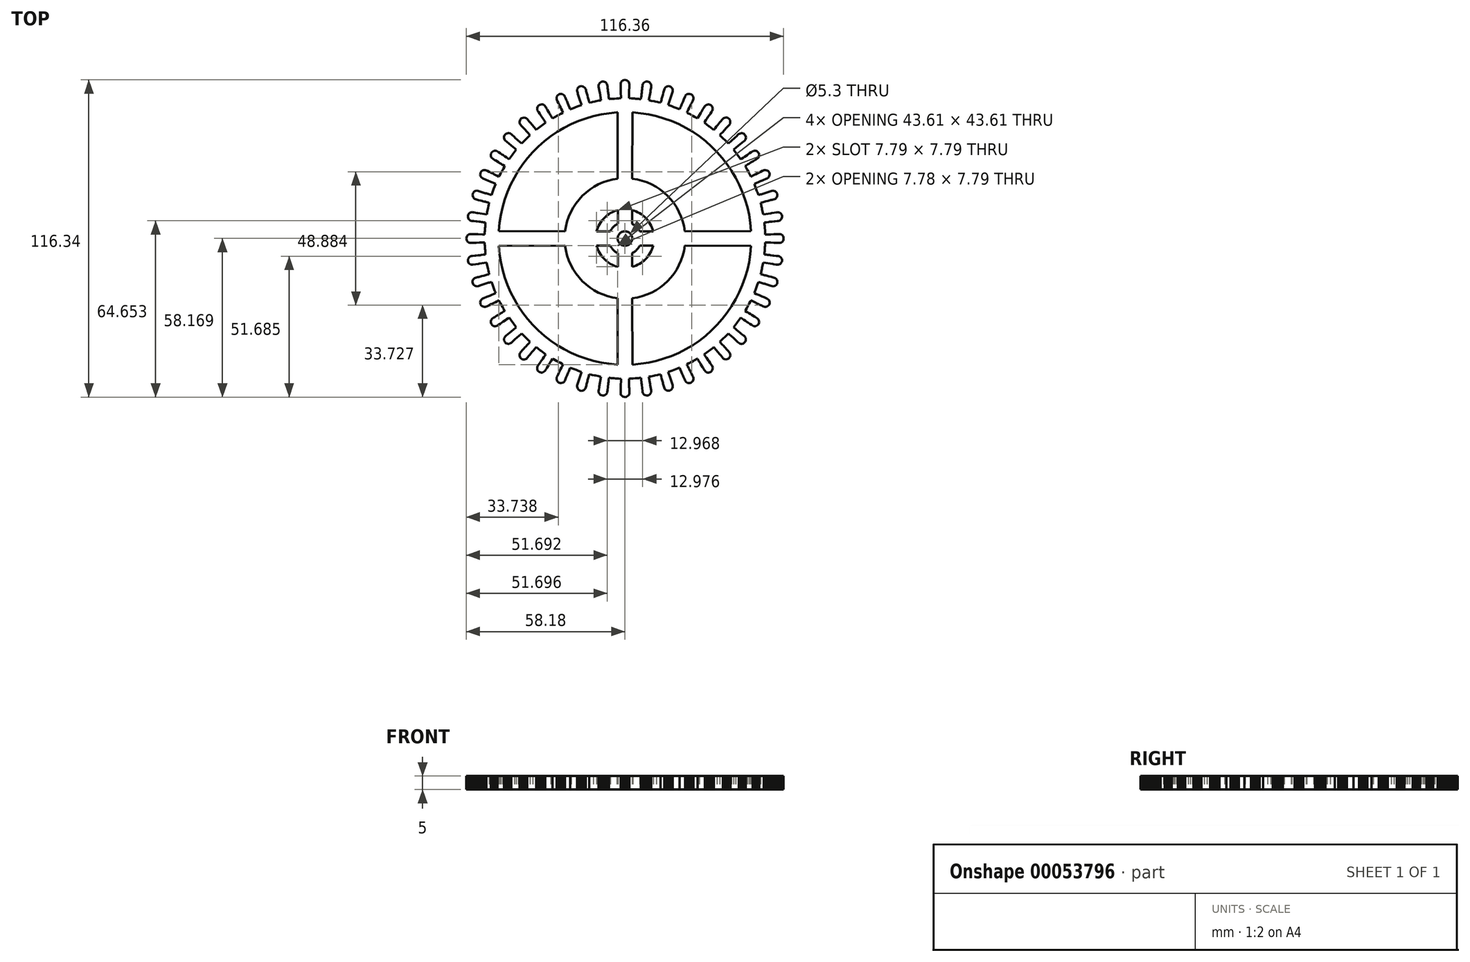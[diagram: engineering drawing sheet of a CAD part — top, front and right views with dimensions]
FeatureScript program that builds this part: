
annotation { "Feature Type Name" : "Feature", "Feature Type Description" : "" }
export const myFeature = defineFeature(function(context is Context, id is Id, definition is map)
    precondition{}
    {
        {
            var Q0;
            Q0=qCreatedBy(makeId("Top.planeOp"),FACE);
            var sketch = newSketch(context, id + "F0", { "sketchPlane" : qUnion([Q0])});
            skLineSegment(sketch, "E0", {"start": v(49.47, -1.46) * mm, "end": v(49.81, -1.47) * mm});
            skLineSegment(sketch, "E1", {"start": v(49.81, -1.47) * mm, "end": v(50.2, -1.49) * mm});
            skLineSegment(sketch, "E2", {"start": v(50.2, -1.49) * mm, "end": v(50.6, -1.5) * mm});
            skLineSegment(sketch, "E3", {"start": v(50.6, -1.5) * mm, "end": v(51, -1.5) * mm});
            skLineSegment(sketch, "E4", {"start": v(51, -1.5) * mm, "end": v(51.4, -1.52) * mm});
            skLineSegment(sketch, "E5", {"start": v(51.4, -1.52) * mm, "end": v(51.78, -1.53) * mm});
            skLineSegment(sketch, "E6", {"start": v(51.78, -1.53) * mm, "end": v(52.18, -1.54) * mm});
            skLineSegment(sketch, "E7", {"start": v(52.18, -1.54) * mm, "end": v(52.58, -1.55) * mm});
            skLineSegment(sketch, "E8", {"start": v(52.58, -1.55) * mm, "end": v(52.97, -1.56) * mm});
            skLineSegment(sketch, "E9", {"start": v(52.97, -1.56) * mm, "end": v(53.37, -1.58) * mm});
            skLineSegment(sketch, "E10", {"start": v(53.37, -1.58) * mm, "end": v(53.76, -1.59) * mm});
            skLineSegment(sketch, "E11", {"start": v(53.76, -1.59) * mm, "end": v(54.16, -1.6) * mm});
            skLineSegment(sketch, "E12", {"start": v(54.16, -1.6) * mm, "end": v(54.56, -1.6) * mm});
            skLineSegment(sketch, "E13", {"start": v(54.56, -1.6) * mm, "end": v(54.98, -1.56) * mm});
            skLineSegment(sketch, "E14", {"start": v(54.98, -1.56) * mm, "end": v(55.37, -1.4) * mm});
            skLineSegment(sketch, "E15", {"start": v(55.37, -1.4) * mm, "end": v(55.7, -1.15) * mm});
            skLineSegment(sketch, "E16", {"start": v(55.7, -1.15) * mm, "end": v(55.97, -0.81) * mm});
            skLineSegment(sketch, "E17", {"start": v(55.97, -0.81) * mm, "end": v(56.13, -0.42) * mm});
            skLineSegment(sketch, "E18", {"start": v(56.13, -0.42) * mm, "end": v(56.19, 0) * mm});
            skLineSegment(sketch, "E19", {"start": v(56.19, 0) * mm, "end": v(56.13, 0.42) * mm});
            skLineSegment(sketch, "E20", {"start": v(56.13, 0.42) * mm, "end": v(55.97, 0.8) * mm});
            skLineSegment(sketch, "E21", {"start": v(55.97, 0.8) * mm, "end": v(55.7, 1.14) * mm});
            skLineSegment(sketch, "E22", {"start": v(55.7, 1.14) * mm, "end": v(55.37, 1.4) * mm});
            skLineSegment(sketch, "E23", {"start": v(55.37, 1.4) * mm, "end": v(54.98, 1.56) * mm});
            skLineSegment(sketch, "E24", {"start": v(54.98, 1.56) * mm, "end": v(54.56, 1.6) * mm});
            skLineSegment(sketch, "E25", {"start": v(54.56, 1.6) * mm, "end": v(54.16, 1.6) * mm});
            skLineSegment(sketch, "E26", {"start": v(54.16, 1.6) * mm, "end": v(53.77, 1.58) * mm});
            skLineSegment(sketch, "E27", {"start": v(53.77, 1.58) * mm, "end": v(53.37, 1.57) * mm});
            skLineSegment(sketch, "E28", {"start": v(53.37, 1.57) * mm, "end": v(52.98, 1.56) * mm});
            skLineSegment(sketch, "E29", {"start": v(52.98, 1.56) * mm, "end": v(52.58, 1.55) * mm});
            skLineSegment(sketch, "E30", {"start": v(52.58, 1.55) * mm, "end": v(52.18, 1.54) * mm});
            skLineSegment(sketch, "E31", {"start": v(52.18, 1.54) * mm, "end": v(51.79, 1.53) * mm});
            skLineSegment(sketch, "E32", {"start": v(51.79, 1.53) * mm, "end": v(51.4, 1.52) * mm});
            skLineSegment(sketch, "E33", {"start": v(51.4, 1.52) * mm, "end": v(51, 1.5) * mm});
            skLineSegment(sketch, "E34", {"start": v(51, 1.5) * mm, "end": v(50.6, 1.5) * mm});
            skLineSegment(sketch, "E35", {"start": v(50.6, 1.5) * mm, "end": v(50.2, 1.48) * mm});
            skLineSegment(sketch, "E36", {"start": v(50.2, 1.48) * mm, "end": v(49.81, 1.47) * mm});
            skLineSegment(sketch, "E37", {"start": v(49.81, 1.47) * mm, "end": v(49.47, 1.46) * mm});
            skLineSegment(sketch, "E38", {"start": v(49.47, 1.46) * mm, "end": v(49.44, 1.85) * mm});
            skLineSegment(sketch, "E39", {"start": v(49.44, 1.85) * mm, "end": v(49.42, 2.25) * mm});
            skLineSegment(sketch, "E40", {"start": v(49.42, 2.25) * mm, "end": v(49.39, 2.64) * mm});
            skLineSegment(sketch, "E41", {"start": v(49.39, 2.64) * mm, "end": v(49.36, 3.03) * mm});
            skLineSegment(sketch, "E42", {"start": v(49.36, 3.03) * mm, "end": v(49.33, 3.43) * mm});
            skLineSegment(sketch, "E43", {"start": v(49.33, 3.43) * mm, "end": v(49.3, 3.82) * mm});
            skLineSegment(sketch, "E44", {"start": v(49.3, 3.82) * mm, "end": v(49.28, 4.21) * mm});
            skLineSegment(sketch, "E45", {"start": v(49.28, 4.21) * mm, "end": v(49.25, 4.6) * mm});
            skLineSegment(sketch, "E46", {"start": v(49.25, 4.6) * mm, "end": v(49.22, 5) * mm});
            skLineSegment(sketch, "E47", {"start": v(49.22, 5) * mm, "end": v(49.2, 5.4) * mm});
            skLineSegment(sketch, "E48", {"start": v(49.2, 5.4) * mm, "end": v(49.16, 5.78) * mm});
            skLineSegment(sketch, "E49", {"start": v(49.16, 5.78) * mm, "end": v(49.16, 5.87) * mm});
            skLineSegment(sketch, "E50", {"start": v(49.16, 5.87) * mm, "end": v(49.55, 5.92) * mm});
            skLineSegment(sketch, "E51", {"start": v(49.55, 5.92) * mm, "end": v(49.94, 5.96) * mm});
            skLineSegment(sketch, "E52", {"start": v(49.94, 5.96) * mm, "end": v(50.34, 6) * mm});
            skLineSegment(sketch, "E53", {"start": v(50.34, 6) * mm, "end": v(50.73, 6.05) * mm});
            skLineSegment(sketch, "E54", {"start": v(50.73, 6.05) * mm, "end": v(51.12, 6.1) * mm});
            skLineSegment(sketch, "E55", {"start": v(51.12, 6.1) * mm, "end": v(51.51, 6.15) * mm});
            skLineSegment(sketch, "E56", {"start": v(51.51, 6.15) * mm, "end": v(51.9, 6.2) * mm});
            skLineSegment(sketch, "E57", {"start": v(51.9, 6.2) * mm, "end": v(52.3, 6.24) * mm});
            skLineSegment(sketch, "E58", {"start": v(52.3, 6.24) * mm, "end": v(52.7, 6.28) * mm});
            skLineSegment(sketch, "E59", {"start": v(52.7, 6.28) * mm, "end": v(53.08, 6.33) * mm});
            skLineSegment(sketch, "E60", {"start": v(53.08, 6.33) * mm, "end": v(53.48, 6.37) * mm});
            skLineSegment(sketch, "E61", {"start": v(53.48, 6.37) * mm, "end": v(53.87, 6.42) * mm});
            skLineSegment(sketch, "E62", {"start": v(53.87, 6.42) * mm, "end": v(54.3, 6.47) * mm});
            skLineSegment(sketch, "E63", {"start": v(54.3, 6.47) * mm, "end": v(54.7, 6.6) * mm});
            skLineSegment(sketch, "E64", {"start": v(54.7, 6.6) * mm, "end": v(55.05, 6.83) * mm});
            skLineSegment(sketch, "E65", {"start": v(55.05, 6.83) * mm, "end": v(55.33, 7.15) * mm});
            skLineSegment(sketch, "E66", {"start": v(55.33, 7.15) * mm, "end": v(55.52, 7.52) * mm});
            skLineSegment(sketch, "E67", {"start": v(55.52, 7.52) * mm, "end": v(55.6, 7.94) * mm});
            skLineSegment(sketch, "E68", {"start": v(55.6, 7.94) * mm, "end": v(55.6, 8.28) * mm});
            skLineSegment(sketch, "E69", {"start": v(55.6, 8.28) * mm, "end": v(55.48, 8.69) * mm});
            skLineSegment(sketch, "E70", {"start": v(55.48, 8.69) * mm, "end": v(55.26, 9.05) * mm});
            skLineSegment(sketch, "E71", {"start": v(55.26, 9.05) * mm, "end": v(54.96, 9.34) * mm});
            skLineSegment(sketch, "E72", {"start": v(54.96, 9.34) * mm, "end": v(54.59, 9.55) * mm});
            skLineSegment(sketch, "E73", {"start": v(54.59, 9.55) * mm, "end": v(54.17, 9.65) * mm});
            skLineSegment(sketch, "E74", {"start": v(54.17, 9.65) * mm, "end": v(54, 9.66) * mm});
            skLineSegment(sketch, "E75", {"start": v(54, 9.66) * mm, "end": v(53.75, 9.64) * mm});
            skLineSegment(sketch, "E76", {"start": v(53.75, 9.64) * mm, "end": v(53.36, 9.57) * mm});
            skLineSegment(sketch, "E77", {"start": v(53.36, 9.57) * mm, "end": v(52.98, 9.5) * mm});
            skLineSegment(sketch, "E78", {"start": v(52.98, 9.5) * mm, "end": v(52.58, 9.44) * mm});
            skLineSegment(sketch, "E79", {"start": v(52.58, 9.44) * mm, "end": v(52.2, 9.37) * mm});
            skLineSegment(sketch, "E80", {"start": v(52.2, 9.37) * mm, "end": v(51.8, 9.3) * mm});
            skLineSegment(sketch, "E81", {"start": v(51.8, 9.3) * mm, "end": v(51.41, 9.23) * mm});
            skLineSegment(sketch, "E82", {"start": v(51.41, 9.23) * mm, "end": v(51.02, 9.17) * mm});
            skLineSegment(sketch, "E83", {"start": v(51.02, 9.17) * mm, "end": v(50.64, 9.1) * mm});
            skLineSegment(sketch, "E84", {"start": v(50.64, 9.1) * mm, "end": v(50.24, 9.03) * mm});
            skLineSegment(sketch, "E85", {"start": v(50.24, 9.03) * mm, "end": v(49.86, 8.96) * mm});
            skLineSegment(sketch, "E86", {"start": v(49.86, 8.96) * mm, "end": v(49.47, 8.9) * mm});
            skLineSegment(sketch, "E87", {"start": v(49.47, 8.9) * mm, "end": v(49.07, 8.83) * mm});
            skLineSegment(sketch, "E88", {"start": v(49.07, 8.83) * mm, "end": v(48.74, 8.77) * mm});
            skLineSegment(sketch, "E89", {"start": v(48.74, 8.77) * mm, "end": v(48.66, 9.16) * mm});
            skLineSegment(sketch, "E90", {"start": v(48.66, 9.16) * mm, "end": v(48.57, 9.54) * mm});
            skLineSegment(sketch, "E91", {"start": v(48.57, 9.54) * mm, "end": v(48.49, 9.93) * mm});
            skLineSegment(sketch, "E92", {"start": v(48.49, 9.93) * mm, "end": v(48.4, 10.31) * mm});
            skLineSegment(sketch, "E93", {"start": v(48.4, 10.31) * mm, "end": v(48.32, 10.7) * mm});
            skLineSegment(sketch, "E94", {"start": v(48.32, 10.7) * mm, "end": v(48.24, 11.08) * mm});
            skLineSegment(sketch, "E95", {"start": v(48.24, 11.08) * mm, "end": v(48.15, 11.46) * mm});
            skLineSegment(sketch, "E96", {"start": v(48.15, 11.46) * mm, "end": v(48.07, 11.85) * mm});
            skLineSegment(sketch, "E97", {"start": v(48.07, 11.85) * mm, "end": v(47.99, 12.23) * mm});
            skLineSegment(sketch, "E98", {"start": v(47.99, 12.23) * mm, "end": v(47.9, 12.62) * mm});
            skLineSegment(sketch, "E99", {"start": v(47.9, 12.62) * mm, "end": v(47.82, 13) * mm});
            skLineSegment(sketch, "E100", {"start": v(47.82, 13) * mm, "end": v(47.8, 13.1) * mm});
            skLineSegment(sketch, "E101", {"start": v(47.8, 13.1) * mm, "end": v(48.18, 13.2) * mm});
            skLineSegment(sketch, "E102", {"start": v(48.18, 13.2) * mm, "end": v(48.56, 13.3) * mm});
            skLineSegment(sketch, "E103", {"start": v(48.56, 13.3) * mm, "end": v(48.95, 13.4) * mm});
            skLineSegment(sketch, "E104", {"start": v(48.95, 13.4) * mm, "end": v(49.33, 13.5) * mm});
            skLineSegment(sketch, "E105", {"start": v(49.33, 13.5) * mm, "end": v(49.7, 13.6) * mm});
            skLineSegment(sketch, "E106", {"start": v(49.7, 13.6) * mm, "end": v(50.1, 13.7) * mm});
            skLineSegment(sketch, "E107", {"start": v(50.1, 13.7) * mm, "end": v(50.48, 13.8) * mm});
            skLineSegment(sketch, "E108", {"start": v(50.48, 13.8) * mm, "end": v(50.86, 13.9) * mm});
            skLineSegment(sketch, "E109", {"start": v(50.86, 13.9) * mm, "end": v(51.24, 14) * mm});
            skLineSegment(sketch, "E110", {"start": v(51.24, 14) * mm, "end": v(51.62, 14.1) * mm});
            skLineSegment(sketch, "E111", {"start": v(51.62, 14.1) * mm, "end": v(52, 14.2) * mm});
            skLineSegment(sketch, "E112", {"start": v(52, 14.2) * mm, "end": v(52.4, 14.3) * mm});
            skLineSegment(sketch, "E113", {"start": v(52.4, 14.3) * mm, "end": v(52.8, 14.41) * mm});
            skLineSegment(sketch, "E114", {"start": v(52.8, 14.41) * mm, "end": v(53.18, 14.6) * mm});
            skLineSegment(sketch, "E115", {"start": v(53.18, 14.6) * mm, "end": v(53.5, 14.88) * mm});
            skLineSegment(sketch, "E116", {"start": v(53.5, 14.88) * mm, "end": v(53.73, 15.23) * mm});
            skLineSegment(sketch, "E117", {"start": v(53.73, 15.23) * mm, "end": v(53.87, 15.63) * mm});
            skLineSegment(sketch, "E118", {"start": v(53.87, 15.63) * mm, "end": v(53.89, 16.06) * mm});
            skLineSegment(sketch, "E119", {"start": v(53.89, 16.06) * mm, "end": v(53.83, 16.39) * mm});
            skLineSegment(sketch, "E120", {"start": v(53.83, 16.39) * mm, "end": v(53.66, 16.78) * mm});
            skLineSegment(sketch, "E121", {"start": v(53.66, 16.78) * mm, "end": v(53.4, 17.1) * mm});
            skLineSegment(sketch, "E122", {"start": v(53.4, 17.1) * mm, "end": v(53.05, 17.35) * mm});
            skLineSegment(sketch, "E123", {"start": v(53.05, 17.35) * mm, "end": v(52.65, 17.5) * mm});
            skLineSegment(sketch, "E124", {"start": v(52.65, 17.5) * mm, "end": v(52.31, 17.54) * mm});
            skLineSegment(sketch, "E125", {"start": v(52.31, 17.54) * mm, "end": v(51.9, 17.5) * mm});
            skLineSegment(sketch, "E126", {"start": v(51.9, 17.5) * mm, "end": v(51.81, 17.47) * mm});
            skLineSegment(sketch, "E127", {"start": v(51.81, 17.47) * mm, "end": v(51.44, 17.35) * mm});
            skLineSegment(sketch, "E128", {"start": v(51.44, 17.35) * mm, "end": v(51.06, 17.23) * mm});
            skLineSegment(sketch, "E129", {"start": v(51.06, 17.23) * mm, "end": v(50.68, 17.1) * mm});
            skLineSegment(sketch, "E130", {"start": v(50.68, 17.1) * mm, "end": v(50.3, 16.98) * mm});
            skLineSegment(sketch, "E131", {"start": v(50.3, 16.98) * mm, "end": v(49.93, 16.86) * mm});
            skLineSegment(sketch, "E132", {"start": v(49.93, 16.86) * mm, "end": v(49.55, 16.74) * mm});
            skLineSegment(sketch, "E133", {"start": v(49.55, 16.74) * mm, "end": v(49.18, 16.62) * mm});
            skLineSegment(sketch, "E134", {"start": v(49.18, 16.62) * mm, "end": v(48.8, 16.5) * mm});
            skLineSegment(sketch, "E135", {"start": v(48.8, 16.5) * mm, "end": v(48.43, 16.37) * mm});
            skLineSegment(sketch, "E136", {"start": v(48.43, 16.37) * mm, "end": v(48.05, 16.25) * mm});
            skLineSegment(sketch, "E137", {"start": v(48.05, 16.25) * mm, "end": v(47.68, 16.13) * mm});
            skLineSegment(sketch, "E138", {"start": v(47.68, 16.13) * mm, "end": v(47.3, 16) * mm});
            skLineSegment(sketch, "E139", {"start": v(47.3, 16) * mm, "end": v(46.98, 15.9) * mm});
            skLineSegment(sketch, "E140", {"start": v(46.98, 15.9) * mm, "end": v(46.84, 16.27) * mm});
            skLineSegment(sketch, "E141", {"start": v(46.84, 16.27) * mm, "end": v(46.7, 16.64) * mm});
            skLineSegment(sketch, "E142", {"start": v(46.7, 16.64) * mm, "end": v(46.56, 17) * mm});
            skLineSegment(sketch, "E143", {"start": v(46.56, 17) * mm, "end": v(46.42, 17.38) * mm});
            skLineSegment(sketch, "E144", {"start": v(46.42, 17.38) * mm, "end": v(46.29, 17.75) * mm});
            skLineSegment(sketch, "E145", {"start": v(46.29, 17.75) * mm, "end": v(46.15, 18.12) * mm});
            skLineSegment(sketch, "E146", {"start": v(46.15, 18.12) * mm, "end": v(46.01, 18.48) * mm});
            skLineSegment(sketch, "E147", {"start": v(46.01, 18.48) * mm, "end": v(45.87, 18.85) * mm});
            skLineSegment(sketch, "E148", {"start": v(45.87, 18.85) * mm, "end": v(45.74, 19.22) * mm});
            skLineSegment(sketch, "E149", {"start": v(45.74, 19.22) * mm, "end": v(45.6, 19.6) * mm});
            skLineSegment(sketch, "E150", {"start": v(45.6, 19.6) * mm, "end": v(45.46, 19.96) * mm});
            skLineSegment(sketch, "E151", {"start": v(45.46, 19.96) * mm, "end": v(45.43, 20.05) * mm});
            skLineSegment(sketch, "E152", {"start": v(45.43, 20.05) * mm, "end": v(45.8, 20.2) * mm});
            skLineSegment(sketch, "E153", {"start": v(45.8, 20.2) * mm, "end": v(46.15, 20.35) * mm});
            skLineSegment(sketch, "E154", {"start": v(46.15, 20.35) * mm, "end": v(46.52, 20.5) * mm});
            skLineSegment(sketch, "E155", {"start": v(46.52, 20.5) * mm, "end": v(46.88, 20.66) * mm});
            skLineSegment(sketch, "E156", {"start": v(46.88, 20.66) * mm, "end": v(47.25, 20.81) * mm});
            skLineSegment(sketch, "E157", {"start": v(47.25, 20.81) * mm, "end": v(47.62, 20.97) * mm});
            skLineSegment(sketch, "E158", {"start": v(47.62, 20.97) * mm, "end": v(47.98, 21.12) * mm});
            skLineSegment(sketch, "E159", {"start": v(47.98, 21.12) * mm, "end": v(48.34, 21.28) * mm});
            skLineSegment(sketch, "E160", {"start": v(48.34, 21.28) * mm, "end": v(48.7, 21.43) * mm});
            skLineSegment(sketch, "E161", {"start": v(48.7, 21.43) * mm, "end": v(49.07, 21.59) * mm});
            skLineSegment(sketch, "E162", {"start": v(49.07, 21.59) * mm, "end": v(49.43, 21.74) * mm});
            skLineSegment(sketch, "E163", {"start": v(49.43, 21.74) * mm, "end": v(49.8, 21.9) * mm});
            skLineSegment(sketch, "E164", {"start": v(49.8, 21.9) * mm, "end": v(50.2, 22.06) * mm});
            skLineSegment(sketch, "E165", {"start": v(50.2, 22.06) * mm, "end": v(50.54, 22.3) * mm});
            skLineSegment(sketch, "E166", {"start": v(50.54, 22.3) * mm, "end": v(50.82, 22.62) * mm});
            skLineSegment(sketch, "E167", {"start": v(50.82, 22.62) * mm, "end": v(51, 23) * mm});
            skLineSegment(sketch, "E168", {"start": v(51, 23) * mm, "end": v(51.07, 23.42) * mm});
            skLineSegment(sketch, "E169", {"start": v(51.07, 23.42) * mm, "end": v(51.04, 23.84) * mm});
            skLineSegment(sketch, "E170", {"start": v(51.04, 23.84) * mm, "end": v(50.93, 24.17) * mm});
            skLineSegment(sketch, "E171", {"start": v(50.93, 24.17) * mm, "end": v(50.7, 24.52) * mm});
            skLineSegment(sketch, "E172", {"start": v(50.7, 24.52) * mm, "end": v(50.4, 24.81) * mm});
            skLineSegment(sketch, "E173", {"start": v(50.4, 24.81) * mm, "end": v(50.02, 25) * mm});
            skLineSegment(sketch, "E174", {"start": v(50.02, 25) * mm, "end": v(49.6, 25.1) * mm});
            skLineSegment(sketch, "E175", {"start": v(49.6, 25.1) * mm, "end": v(49.43, 25.1) * mm});
            skLineSegment(sketch, "E176", {"start": v(49.43, 25.1) * mm, "end": v(49.02, 25.04) * mm});
            skLineSegment(sketch, "E177", {"start": v(49.02, 25.04) * mm, "end": v(48.78, 24.95) * mm});
            skLineSegment(sketch, "E178", {"start": v(48.78, 24.95) * mm, "end": v(48.42, 24.78) * mm});
            skLineSegment(sketch, "E179", {"start": v(48.42, 24.78) * mm, "end": v(48.07, 24.6) * mm});
            skLineSegment(sketch, "E180", {"start": v(48.07, 24.6) * mm, "end": v(47.71, 24.43) * mm});
            skLineSegment(sketch, "E181", {"start": v(47.71, 24.43) * mm, "end": v(47.36, 24.25) * mm});
            skLineSegment(sketch, "E182", {"start": v(47.36, 24.25) * mm, "end": v(47, 24.08) * mm});
            skLineSegment(sketch, "E183", {"start": v(47, 24.08) * mm, "end": v(46.65, 23.9) * mm});
            skLineSegment(sketch, "E184", {"start": v(46.65, 23.9) * mm, "end": v(46.3, 23.73) * mm});
            skLineSegment(sketch, "E185", {"start": v(46.3, 23.73) * mm, "end": v(45.94, 23.56) * mm});
            skLineSegment(sketch, "E186", {"start": v(45.94, 23.56) * mm, "end": v(45.58, 23.38) * mm});
            skLineSegment(sketch, "E187", {"start": v(45.58, 23.38) * mm, "end": v(45.23, 23.2) * mm});
            skLineSegment(sketch, "E188", {"start": v(45.23, 23.2) * mm, "end": v(44.88, 23.03) * mm});
            skLineSegment(sketch, "E189", {"start": v(44.88, 23.03) * mm, "end": v(44.52, 22.86) * mm});
            skLineSegment(sketch, "E190", {"start": v(44.52, 22.86) * mm, "end": v(44.21, 22.7) * mm});
            skLineSegment(sketch, "E191", {"start": v(44.21, 22.7) * mm, "end": v(44.02, 23.05) * mm});
            skLineSegment(sketch, "E192", {"start": v(44.02, 23.05) * mm, "end": v(43.84, 23.4) * mm});
            skLineSegment(sketch, "E193", {"start": v(43.84, 23.4) * mm, "end": v(43.65, 23.74) * mm});
            skLineSegment(sketch, "E194", {"start": v(43.65, 23.74) * mm, "end": v(43.46, 24.1) * mm});
            skLineSegment(sketch, "E195", {"start": v(43.46, 24.1) * mm, "end": v(43.27, 24.44) * mm});
            skLineSegment(sketch, "E196", {"start": v(43.27, 24.44) * mm, "end": v(43.08, 24.78) * mm});
            skLineSegment(sketch, "E197", {"start": v(43.08, 24.78) * mm, "end": v(42.9, 25.13) * mm});
            skLineSegment(sketch, "E198", {"start": v(42.9, 25.13) * mm, "end": v(42.7, 25.47) * mm});
            skLineSegment(sketch, "E199", {"start": v(42.7, 25.47) * mm, "end": v(42.52, 25.82) * mm});
            skLineSegment(sketch, "E200", {"start": v(42.52, 25.82) * mm, "end": v(42.33, 26.16) * mm});
            skLineSegment(sketch, "E201", {"start": v(42.33, 26.16) * mm, "end": v(42.14, 26.5) * mm});
            skLineSegment(sketch, "E202", {"start": v(42.14, 26.5) * mm, "end": v(42.1, 26.6) * mm});
            skLineSegment(sketch, "E203", {"start": v(42.1, 26.6) * mm, "end": v(42.43, 26.8) * mm});
            skLineSegment(sketch, "E204", {"start": v(42.43, 26.8) * mm, "end": v(42.77, 27) * mm});
            skLineSegment(sketch, "E205", {"start": v(42.77, 27) * mm, "end": v(43.1, 27.2) * mm});
            skLineSegment(sketch, "E206", {"start": v(43.1, 27.2) * mm, "end": v(43.45, 27.4) * mm});
            skLineSegment(sketch, "E207", {"start": v(43.45, 27.4) * mm, "end": v(43.78, 27.61) * mm});
            skLineSegment(sketch, "E208", {"start": v(43.78, 27.61) * mm, "end": v(44.13, 27.82) * mm});
            skLineSegment(sketch, "E209", {"start": v(44.13, 27.82) * mm, "end": v(44.46, 28.02) * mm});
            skLineSegment(sketch, "E210", {"start": v(44.46, 28.02) * mm, "end": v(44.8, 28.22) * mm});
            skLineSegment(sketch, "E211", {"start": v(44.8, 28.22) * mm, "end": v(45.14, 28.43) * mm});
            skLineSegment(sketch, "E212", {"start": v(45.14, 28.43) * mm, "end": v(45.48, 28.63) * mm});
            skLineSegment(sketch, "E213", {"start": v(45.48, 28.63) * mm, "end": v(45.82, 28.84) * mm});
            skLineSegment(sketch, "E214", {"start": v(45.82, 28.84) * mm, "end": v(46.16, 29.04) * mm});
            skLineSegment(sketch, "E215", {"start": v(46.16, 29.04) * mm, "end": v(46.52, 29.26) * mm});
            skLineSegment(sketch, "E216", {"start": v(46.52, 29.26) * mm, "end": v(46.83, 29.55) * mm});
            skLineSegment(sketch, "E217", {"start": v(46.83, 29.55) * mm, "end": v(47.06, 29.9) * mm});
            skLineSegment(sketch, "E218", {"start": v(47.06, 29.9) * mm, "end": v(47.18, 30.31) * mm});
            skLineSegment(sketch, "E219", {"start": v(47.18, 30.31) * mm, "end": v(47.2, 30.74) * mm});
            skLineSegment(sketch, "E220", {"start": v(47.2, 30.74) * mm, "end": v(47.1, 31.15) * mm});
            skLineSegment(sketch, "E221", {"start": v(47.1, 31.15) * mm, "end": v(46.95, 31.45) * mm});
            skLineSegment(sketch, "E222", {"start": v(46.95, 31.45) * mm, "end": v(46.68, 31.77) * mm});
            skLineSegment(sketch, "E223", {"start": v(46.68, 31.77) * mm, "end": v(46.33, 32.01) * mm});
            skLineSegment(sketch, "E224", {"start": v(46.33, 32.01) * mm, "end": v(45.93, 32.16) * mm});
            skLineSegment(sketch, "E225", {"start": v(45.93, 32.16) * mm, "end": v(45.6, 32.19) * mm});
            skLineSegment(sketch, "E226", {"start": v(45.6, 32.19) * mm, "end": v(45.17, 32.13) * mm});
            skLineSegment(sketch, "E227", {"start": v(45.17, 32.13) * mm, "end": v(44.78, 31.97) * mm});
            skLineSegment(sketch, "E228", {"start": v(44.78, 31.97) * mm, "end": v(44.7, 31.92) * mm});
            skLineSegment(sketch, "E229", {"start": v(44.7, 31.92) * mm, "end": v(44.38, 31.7) * mm});
            skLineSegment(sketch, "E230", {"start": v(44.38, 31.7) * mm, "end": v(44.06, 31.48) * mm});
            skLineSegment(sketch, "E231", {"start": v(44.06, 31.48) * mm, "end": v(43.73, 31.25) * mm});
            skLineSegment(sketch, "E232", {"start": v(43.73, 31.25) * mm, "end": v(43.4, 31.03) * mm});
            skLineSegment(sketch, "E233", {"start": v(43.4, 31.03) * mm, "end": v(43.08, 30.8) * mm});
            skLineSegment(sketch, "E234", {"start": v(43.08, 30.8) * mm, "end": v(42.75, 30.58) * mm});
            skLineSegment(sketch, "E235", {"start": v(42.75, 30.58) * mm, "end": v(42.43, 30.36) * mm});
            skLineSegment(sketch, "E236", {"start": v(42.43, 30.36) * mm, "end": v(42.1, 30.14) * mm});
            skLineSegment(sketch, "E237", {"start": v(42.1, 30.14) * mm, "end": v(41.77, 29.91) * mm});
            skLineSegment(sketch, "E238", {"start": v(41.77, 29.91) * mm, "end": v(41.45, 29.7) * mm});
            skLineSegment(sketch, "E239", {"start": v(41.45, 29.7) * mm, "end": v(41.12, 29.47) * mm});
            skLineSegment(sketch, "E240", {"start": v(41.12, 29.47) * mm, "end": v(40.8, 29.24) * mm});
            skLineSegment(sketch, "E241", {"start": v(40.8, 29.24) * mm, "end": v(40.51, 29.05) * mm});
            skLineSegment(sketch, "E242", {"start": v(40.51, 29.05) * mm, "end": v(40.28, 29.37) * mm});
            skLineSegment(sketch, "E243", {"start": v(40.28, 29.37) * mm, "end": v(40.04, 29.68) * mm});
            skLineSegment(sketch, "E244", {"start": v(40.04, 29.68) * mm, "end": v(39.8, 30) * mm});
            skLineSegment(sketch, "E245", {"start": v(39.8, 30) * mm, "end": v(39.57, 30.31) * mm});
            skLineSegment(sketch, "E246", {"start": v(39.57, 30.31) * mm, "end": v(39.33, 30.63) * mm});
            skLineSegment(sketch, "E247", {"start": v(39.33, 30.63) * mm, "end": v(39.1, 30.94) * mm});
            skLineSegment(sketch, "E248", {"start": v(39.1, 30.94) * mm, "end": v(38.86, 31.26) * mm});
            skLineSegment(sketch, "E249", {"start": v(38.86, 31.26) * mm, "end": v(38.62, 31.57) * mm});
            skLineSegment(sketch, "E250", {"start": v(38.62, 31.57) * mm, "end": v(38.39, 31.89) * mm});
            skLineSegment(sketch, "E251", {"start": v(38.39, 31.89) * mm, "end": v(38.15, 32.2) * mm});
            skLineSegment(sketch, "E252", {"start": v(38.15, 32.2) * mm, "end": v(37.92, 32.52) * mm});
            skLineSegment(sketch, "E253", {"start": v(37.92, 32.52) * mm, "end": v(37.86, 32.6) * mm});
            skLineSegment(sketch, "E254", {"start": v(37.86, 32.6) * mm, "end": v(38.17, 32.84) * mm});
            skLineSegment(sketch, "E255", {"start": v(38.17, 32.84) * mm, "end": v(38.47, 33.1) * mm});
            skLineSegment(sketch, "E256", {"start": v(38.47, 33.1) * mm, "end": v(38.78, 33.35) * mm});
            skLineSegment(sketch, "E257", {"start": v(38.78, 33.35) * mm, "end": v(39.08, 33.6) * mm});
            skLineSegment(sketch, "E258", {"start": v(39.08, 33.6) * mm, "end": v(39.39, 33.84) * mm});
            skLineSegment(sketch, "E259", {"start": v(39.39, 33.84) * mm, "end": v(39.7, 34.1) * mm});
            skLineSegment(sketch, "E260", {"start": v(39.7, 34.1) * mm, "end": v(40, 34.35) * mm});
            skLineSegment(sketch, "E261", {"start": v(40, 34.35) * mm, "end": v(40.3, 34.6) * mm});
            skLineSegment(sketch, "E262", {"start": v(40.3, 34.6) * mm, "end": v(40.62, 34.85) * mm});
            skLineSegment(sketch, "E263", {"start": v(40.62, 34.85) * mm, "end": v(40.92, 35.1) * mm});
            skLineSegment(sketch, "E264", {"start": v(40.92, 35.1) * mm, "end": v(41.23, 35.35) * mm});
            skLineSegment(sketch, "E265", {"start": v(41.23, 35.35) * mm, "end": v(41.53, 35.6) * mm});
            skLineSegment(sketch, "E266", {"start": v(41.53, 35.6) * mm, "end": v(41.86, 35.87) * mm});
            skLineSegment(sketch, "E267", {"start": v(41.86, 35.87) * mm, "end": v(42.13, 36.2) * mm});
            skLineSegment(sketch, "E268", {"start": v(42.13, 36.2) * mm, "end": v(42.3, 36.58) * mm});
            skLineSegment(sketch, "E269", {"start": v(42.3, 36.58) * mm, "end": v(42.37, 37) * mm});
            skLineSegment(sketch, "E270", {"start": v(42.37, 37) * mm, "end": v(42.32, 37.42) * mm});
            skLineSegment(sketch, "E271", {"start": v(42.32, 37.42) * mm, "end": v(42.17, 37.82) * mm});
            skLineSegment(sketch, "E272", {"start": v(42.17, 37.82) * mm, "end": v(41.98, 38.1) * mm});
            skLineSegment(sketch, "E273", {"start": v(41.98, 38.1) * mm, "end": v(41.66, 38.38) * mm});
            skLineSegment(sketch, "E274", {"start": v(41.66, 38.38) * mm, "end": v(41.28, 38.56) * mm});
            skLineSegment(sketch, "E275", {"start": v(41.28, 38.56) * mm, "end": v(40.86, 38.65) * mm});
            skLineSegment(sketch, "E276", {"start": v(40.86, 38.65) * mm, "end": v(40.78, 38.65) * mm});
            skLineSegment(sketch, "E277", {"start": v(40.78, 38.65) * mm, "end": v(40.36, 38.6) * mm});
            skLineSegment(sketch, "E278", {"start": v(40.36, 38.6) * mm, "end": v(39.97, 38.44) * mm});
            skLineSegment(sketch, "E279", {"start": v(39.97, 38.44) * mm, "end": v(39.7, 38.24) * mm});
            skLineSegment(sketch, "E280", {"start": v(39.7, 38.24) * mm, "end": v(39.4, 37.98) * mm});
            skLineSegment(sketch, "E281", {"start": v(39.4, 37.98) * mm, "end": v(39.11, 37.71) * mm});
            skLineSegment(sketch, "E282", {"start": v(39.11, 37.71) * mm, "end": v(38.82, 37.44) * mm});
            skLineSegment(sketch, "E283", {"start": v(38.82, 37.44) * mm, "end": v(38.53, 37.17) * mm});
            skLineSegment(sketch, "E284", {"start": v(38.53, 37.17) * mm, "end": v(38.24, 36.9) * mm});
            skLineSegment(sketch, "E285", {"start": v(38.24, 36.9) * mm, "end": v(37.94, 36.64) * mm});
            skLineSegment(sketch, "E286", {"start": v(37.94, 36.64) * mm, "end": v(37.65, 36.37) * mm});
            skLineSegment(sketch, "E287", {"start": v(37.65, 36.37) * mm, "end": v(37.36, 36.1) * mm});
            skLineSegment(sketch, "E288", {"start": v(37.36, 36.1) * mm, "end": v(37.07, 35.84) * mm});
            skLineSegment(sketch, "E289", {"start": v(37.07, 35.84) * mm, "end": v(36.78, 35.57) * mm});
            skLineSegment(sketch, "E290", {"start": v(36.78, 35.57) * mm, "end": v(36.49, 35.3) * mm});
            skLineSegment(sketch, "E291", {"start": v(36.49, 35.3) * mm, "end": v(36.2, 35.03) * mm});
            skLineSegment(sketch, "E292", {"start": v(36.2, 35.03) * mm, "end": v(35.94, 34.8) * mm});
            skLineSegment(sketch, "E293", {"start": v(35.94, 34.8) * mm, "end": v(35.67, 35.08) * mm});
            skLineSegment(sketch, "E294", {"start": v(35.67, 35.08) * mm, "end": v(35.39, 35.36) * mm});
            skLineSegment(sketch, "E295", {"start": v(35.39, 35.36) * mm, "end": v(35.1, 35.64) * mm});
            skLineSegment(sketch, "E296", {"start": v(35.1, 35.64) * mm, "end": v(34.83, 35.92) * mm});
            skLineSegment(sketch, "E297", {"start": v(34.83, 35.92) * mm, "end": v(34.55, 36.2) * mm});
            skLineSegment(sketch, "E298", {"start": v(34.55, 36.2) * mm, "end": v(34.27, 36.48) * mm});
            skLineSegment(sketch, "E299", {"start": v(34.27, 36.48) * mm, "end": v(34, 36.75) * mm});
            skLineSegment(sketch, "E300", {"start": v(34, 36.75) * mm, "end": v(33.72, 37.03) * mm});
            skLineSegment(sketch, "E301", {"start": v(33.72, 37.03) * mm, "end": v(33.44, 37.31) * mm});
            skLineSegment(sketch, "E302", {"start": v(33.44, 37.31) * mm, "end": v(33.16, 37.59) * mm});
            skLineSegment(sketch, "E303", {"start": v(33.16, 37.59) * mm, "end": v(32.88, 37.87) * mm});
            skLineSegment(sketch, "E304", {"start": v(32.88, 37.87) * mm, "end": v(32.82, 37.93) * mm});
            skLineSegment(sketch, "E305", {"start": v(32.82, 37.93) * mm, "end": v(33.08, 38.22) * mm});
            skLineSegment(sketch, "E306", {"start": v(33.08, 38.22) * mm, "end": v(33.35, 38.51) * mm});
            skLineSegment(sketch, "E307", {"start": v(33.35, 38.51) * mm, "end": v(33.62, 38.8) * mm});
            skLineSegment(sketch, "E308", {"start": v(33.62, 38.8) * mm, "end": v(33.88, 39.1) * mm});
            skLineSegment(sketch, "E309", {"start": v(33.88, 39.1) * mm, "end": v(34.15, 39.39) * mm});
            skLineSegment(sketch, "E310", {"start": v(34.15, 39.39) * mm, "end": v(34.42, 39.68) * mm});
            skLineSegment(sketch, "E311", {"start": v(34.42, 39.68) * mm, "end": v(34.69, 39.97) * mm});
            skLineSegment(sketch, "E312", {"start": v(34.69, 39.97) * mm, "end": v(34.95, 40.26) * mm});
            skLineSegment(sketch, "E313", {"start": v(34.95, 40.26) * mm, "end": v(35.22, 40.56) * mm});
            skLineSegment(sketch, "E314", {"start": v(35.22, 40.56) * mm, "end": v(35.49, 40.85) * mm});
            skLineSegment(sketch, "E315", {"start": v(35.49, 40.85) * mm, "end": v(35.76, 41.14) * mm});
            skLineSegment(sketch, "E316", {"start": v(35.76, 41.14) * mm, "end": v(36.03, 41.43) * mm});
            skLineSegment(sketch, "E317", {"start": v(36.03, 41.43) * mm, "end": v(36.3, 41.75) * mm});
            skLineSegment(sketch, "E318", {"start": v(36.3, 41.75) * mm, "end": v(36.53, 42.1) * mm});
            skLineSegment(sketch, "E319", {"start": v(36.53, 42.1) * mm, "end": v(36.64, 42.51) * mm});
            skLineSegment(sketch, "E320", {"start": v(36.64, 42.51) * mm, "end": v(36.65, 42.94) * mm});
            skLineSegment(sketch, "E321", {"start": v(36.65, 42.94) * mm, "end": v(36.55, 43.35) * mm});
            skLineSegment(sketch, "E322", {"start": v(36.55, 43.35) * mm, "end": v(36.34, 43.72) * mm});
            skLineSegment(sketch, "E323", {"start": v(36.34, 43.72) * mm, "end": v(36.1, 43.97) * mm});
            skLineSegment(sketch, "E324", {"start": v(36.1, 43.97) * mm, "end": v(35.75, 44.2) * mm});
            skLineSegment(sketch, "E325", {"start": v(35.75, 44.2) * mm, "end": v(35.35, 44.33) * mm});
            skLineSegment(sketch, "E326", {"start": v(35.35, 44.33) * mm, "end": v(35.01, 44.36) * mm});
            skLineSegment(sketch, "E327", {"start": v(35.01, 44.36) * mm, "end": v(34.6, 44.3) * mm});
            skLineSegment(sketch, "E328", {"start": v(34.6, 44.3) * mm, "end": v(34.2, 44.12) * mm});
            skLineSegment(sketch, "E329", {"start": v(34.2, 44.12) * mm, "end": v(33.88, 43.85) * mm});
            skLineSegment(sketch, "E330", {"start": v(33.88, 43.85) * mm, "end": v(33.82, 43.79) * mm});
            skLineSegment(sketch, "E331", {"start": v(33.82, 43.79) * mm, "end": v(33.58, 43.48) * mm});
            skLineSegment(sketch, "E332", {"start": v(33.58, 43.48) * mm, "end": v(33.33, 43.18) * mm});
            skLineSegment(sketch, "E333", {"start": v(33.33, 43.18) * mm, "end": v(33.07, 42.87) * mm});
            skLineSegment(sketch, "E334", {"start": v(33.07, 42.87) * mm, "end": v(32.82, 42.56) * mm});
            skLineSegment(sketch, "E335", {"start": v(32.82, 42.56) * mm, "end": v(32.57, 42.26) * mm});
            skLineSegment(sketch, "E336", {"start": v(32.57, 42.26) * mm, "end": v(32.32, 41.95) * mm});
            skLineSegment(sketch, "E337", {"start": v(32.32, 41.95) * mm, "end": v(32.07, 41.64) * mm});
            skLineSegment(sketch, "E338", {"start": v(32.07, 41.64) * mm, "end": v(31.82, 41.34) * mm});
            skLineSegment(sketch, "E339", {"start": v(31.82, 41.34) * mm, "end": v(31.57, 41.03) * mm});
            skLineSegment(sketch, "E340", {"start": v(31.57, 41.03) * mm, "end": v(31.32, 40.73) * mm});
            skLineSegment(sketch, "E341", {"start": v(31.32, 40.73) * mm, "end": v(31.07, 40.42) * mm});
            skLineSegment(sketch, "E342", {"start": v(31.07, 40.42) * mm, "end": v(30.82, 40.11) * mm});
            skLineSegment(sketch, "E343", {"start": v(30.82, 40.11) * mm, "end": v(30.6, 39.85) * mm});
            skLineSegment(sketch, "E344", {"start": v(30.6, 39.85) * mm, "end": v(30.29, 40.09) * mm});
            skLineSegment(sketch, "E345", {"start": v(30.29, 40.09) * mm, "end": v(29.97, 40.32) * mm});
            skLineSegment(sketch, "E346", {"start": v(29.97, 40.32) * mm, "end": v(29.66, 40.56) * mm});
            skLineSegment(sketch, "E347", {"start": v(29.66, 40.56) * mm, "end": v(29.34, 40.8) * mm});
            skLineSegment(sketch, "E348", {"start": v(29.34, 40.8) * mm, "end": v(29.03, 41.03) * mm});
            skLineSegment(sketch, "E349", {"start": v(29.03, 41.03) * mm, "end": v(28.71, 41.27) * mm});
            skLineSegment(sketch, "E350", {"start": v(28.71, 41.27) * mm, "end": v(28.4, 41.5) * mm});
            skLineSegment(sketch, "E351", {"start": v(28.4, 41.5) * mm, "end": v(28.08, 41.74) * mm});
            skLineSegment(sketch, "E352", {"start": v(28.08, 41.74) * mm, "end": v(27.77, 41.97) * mm});
            skLineSegment(sketch, "E353", {"start": v(27.77, 41.97) * mm, "end": v(27.45, 42.2) * mm});
            skLineSegment(sketch, "E354", {"start": v(27.45, 42.2) * mm, "end": v(27.14, 42.45) * mm});
            skLineSegment(sketch, "E355", {"start": v(27.14, 42.45) * mm, "end": v(27.06, 42.5) * mm});
            skLineSegment(sketch, "E356", {"start": v(27.06, 42.5) * mm, "end": v(27.29, 42.83) * mm});
            skLineSegment(sketch, "E357", {"start": v(27.29, 42.83) * mm, "end": v(27.5, 43.15) * mm});
            skLineSegment(sketch, "E358", {"start": v(27.5, 43.15) * mm, "end": v(27.73, 43.48) * mm});
            skLineSegment(sketch, "E359", {"start": v(27.73, 43.48) * mm, "end": v(27.96, 43.8) * mm});
            skLineSegment(sketch, "E360", {"start": v(27.96, 43.8) * mm, "end": v(28.18, 44.13) * mm});
            skLineSegment(sketch, "E361", {"start": v(28.18, 44.13) * mm, "end": v(28.4, 44.46) * mm});
            skLineSegment(sketch, "E362", {"start": v(28.4, 44.46) * mm, "end": v(28.62, 44.78) * mm});
            skLineSegment(sketch, "E363", {"start": v(28.62, 44.78) * mm, "end": v(28.85, 45.11) * mm});
            skLineSegment(sketch, "E364", {"start": v(28.85, 45.11) * mm, "end": v(29.07, 45.44) * mm});
            skLineSegment(sketch, "E365", {"start": v(29.07, 45.44) * mm, "end": v(29.3, 45.76) * mm});
            skLineSegment(sketch, "E366", {"start": v(29.3, 45.76) * mm, "end": v(29.52, 46.09) * mm});
            skLineSegment(sketch, "E367", {"start": v(29.52, 46.09) * mm, "end": v(29.74, 46.42) * mm});
            skLineSegment(sketch, "E368", {"start": v(29.74, 46.42) * mm, "end": v(29.98, 46.77) * mm});
            skLineSegment(sketch, "E369", {"start": v(29.98, 46.77) * mm, "end": v(30.14, 47.16) * mm});
            skLineSegment(sketch, "E370", {"start": v(30.14, 47.16) * mm, "end": v(30.2, 47.58) * mm});
            skLineSegment(sketch, "E371", {"start": v(30.2, 47.58) * mm, "end": v(30.15, 48) * mm});
            skLineSegment(sketch, "E372", {"start": v(30.15, 48) * mm, "end": v(29.98, 48.4) * mm});
            skLineSegment(sketch, "E373", {"start": v(29.98, 48.4) * mm, "end": v(29.73, 48.73) * mm});
            skLineSegment(sketch, "E374", {"start": v(29.73, 48.73) * mm, "end": v(29.46, 48.94) * mm});
            skLineSegment(sketch, "E375", {"start": v(29.46, 48.94) * mm, "end": v(29.08, 49.12) * mm});
            skLineSegment(sketch, "E376", {"start": v(29.08, 49.12) * mm, "end": v(28.66, 49.2) * mm});
            skLineSegment(sketch, "E377", {"start": v(28.66, 49.2) * mm, "end": v(28.58, 49.2) * mm});
            skLineSegment(sketch, "E378", {"start": v(28.58, 49.2) * mm, "end": v(28.16, 49.13) * mm});
            skLineSegment(sketch, "E379", {"start": v(28.16, 49.13) * mm, "end": v(27.77, 48.97) * mm});
            skLineSegment(sketch, "E380", {"start": v(27.77, 48.97) * mm, "end": v(27.44, 48.7) * mm});
            skLineSegment(sketch, "E381", {"start": v(27.44, 48.7) * mm, "end": v(27.23, 48.44) * mm});
            skLineSegment(sketch, "E382", {"start": v(27.23, 48.44) * mm, "end": v(27.02, 48.1) * mm});
            skLineSegment(sketch, "E383", {"start": v(27.02, 48.1) * mm, "end": v(26.82, 47.76) * mm});
            skLineSegment(sketch, "E384", {"start": v(26.82, 47.76) * mm, "end": v(26.62, 47.42) * mm});
            skLineSegment(sketch, "E385", {"start": v(26.62, 47.42) * mm, "end": v(26.41, 47.08) * mm});
            skLineSegment(sketch, "E386", {"start": v(26.41, 47.08) * mm, "end": v(26.2, 46.75) * mm});
            skLineSegment(sketch, "E387", {"start": v(26.2, 46.75) * mm, "end": v(26, 46.4) * mm});
            skLineSegment(sketch, "E388", {"start": v(26, 46.4) * mm, "end": v(25.8, 46.07) * mm});
            skLineSegment(sketch, "E389", {"start": v(25.8, 46.07) * mm, "end": v(25.6, 45.73) * mm});
            skLineSegment(sketch, "E390", {"start": v(25.6, 45.73) * mm, "end": v(25.39, 45.39) * mm});
            skLineSegment(sketch, "E391", {"start": v(25.39, 45.39) * mm, "end": v(25.19, 45.05) * mm});
            skLineSegment(sketch, "E392", {"start": v(25.19, 45.05) * mm, "end": v(24.98, 44.71) * mm});
            skLineSegment(sketch, "E393", {"start": v(24.98, 44.71) * mm, "end": v(24.78, 44.37) * mm});
            skLineSegment(sketch, "E394", {"start": v(24.78, 44.37) * mm, "end": v(24.6, 44.08) * mm});
            skLineSegment(sketch, "E395", {"start": v(24.6, 44.08) * mm, "end": v(24.26, 44.27) * mm});
            skLineSegment(sketch, "E396", {"start": v(24.26, 44.27) * mm, "end": v(23.91, 44.46) * mm});
            skLineSegment(sketch, "E397", {"start": v(23.91, 44.46) * mm, "end": v(23.56, 44.65) * mm});
            skLineSegment(sketch, "E398", {"start": v(23.56, 44.65) * mm, "end": v(23.22, 44.84) * mm});
            skLineSegment(sketch, "E399", {"start": v(23.22, 44.84) * mm, "end": v(22.87, 45.03) * mm});
            skLineSegment(sketch, "E400", {"start": v(22.87, 45.03) * mm, "end": v(22.53, 45.22) * mm});
            skLineSegment(sketch, "E401", {"start": v(22.53, 45.22) * mm, "end": v(22.18, 45.4) * mm});
            skLineSegment(sketch, "E402", {"start": v(22.18, 45.4) * mm, "end": v(21.84, 45.6) * mm});
            skLineSegment(sketch, "E403", {"start": v(21.84, 45.6) * mm, "end": v(21.5, 45.78) * mm});
            skLineSegment(sketch, "E404", {"start": v(21.5, 45.78) * mm, "end": v(21.15, 45.97) * mm});
            skLineSegment(sketch, "E405", {"start": v(21.15, 45.97) * mm, "end": v(20.8, 46.16) * mm});
            skLineSegment(sketch, "E406", {"start": v(20.8, 46.16) * mm, "end": v(20.72, 46.2) * mm});
            skLineSegment(sketch, "E407", {"start": v(20.72, 46.2) * mm, "end": v(20.9, 46.56) * mm});
            skLineSegment(sketch, "E408", {"start": v(20.9, 46.56) * mm, "end": v(21.07, 46.9) * mm});
            skLineSegment(sketch, "E409", {"start": v(21.07, 46.9) * mm, "end": v(21.24, 47.27) * mm});
            skLineSegment(sketch, "E410", {"start": v(21.24, 47.27) * mm, "end": v(21.42, 47.62) * mm});
            skLineSegment(sketch, "E411", {"start": v(21.42, 47.62) * mm, "end": v(21.59, 47.97) * mm});
            skLineSegment(sketch, "E412", {"start": v(21.59, 47.97) * mm, "end": v(21.77, 48.33) * mm});
            skLineSegment(sketch, "E413", {"start": v(21.77, 48.33) * mm, "end": v(21.94, 48.69) * mm});
            skLineSegment(sketch, "E414", {"start": v(21.94, 48.69) * mm, "end": v(22.11, 49.04) * mm});
            skLineSegment(sketch, "E415", {"start": v(22.11, 49.04) * mm, "end": v(22.29, 49.4) * mm});
            skLineSegment(sketch, "E416", {"start": v(22.29, 49.4) * mm, "end": v(22.46, 49.75) * mm});
            skLineSegment(sketch, "E417", {"start": v(22.46, 49.75) * mm, "end": v(22.64, 50.1) * mm});
            skLineSegment(sketch, "E418", {"start": v(22.64, 50.1) * mm, "end": v(22.81, 50.46) * mm});
            skLineSegment(sketch, "E419", {"start": v(22.81, 50.46) * mm, "end": v(23, 50.84) * mm});
            skLineSegment(sketch, "E420", {"start": v(23, 50.84) * mm, "end": v(23.1, 51.25) * mm});
            skLineSegment(sketch, "E421", {"start": v(23.1, 51.25) * mm, "end": v(23.1, 51.68) * mm});
            skLineSegment(sketch, "E422", {"start": v(23.1, 51.68) * mm, "end": v(22.99, 52.09) * mm});
            skLineSegment(sketch, "E423", {"start": v(22.99, 52.09) * mm, "end": v(22.77, 52.45) * mm});
            skLineSegment(sketch, "E424", {"start": v(22.77, 52.45) * mm, "end": v(22.47, 52.74) * mm});
            skLineSegment(sketch, "E425", {"start": v(22.47, 52.74) * mm, "end": v(22.18, 52.92) * mm});
            skLineSegment(sketch, "E426", {"start": v(22.18, 52.92) * mm, "end": v(21.77, 53.04) * mm});
            skLineSegment(sketch, "E427", {"start": v(21.77, 53.04) * mm, "end": v(21.52, 53.06) * mm});
            skLineSegment(sketch, "E428", {"start": v(21.52, 53.06) * mm, "end": v(21.1, 53) * mm});
            skLineSegment(sketch, "E429", {"start": v(21.1, 53) * mm, "end": v(20.7, 52.85) * mm});
            skLineSegment(sketch, "E430", {"start": v(20.7, 52.85) * mm, "end": v(20.37, 52.6) * mm});
            skLineSegment(sketch, "E431", {"start": v(20.37, 52.6) * mm, "end": v(20.11, 52.25) * mm});
            skLineSegment(sketch, "E432", {"start": v(20.11, 52.25) * mm, "end": v(20.04, 52.1) * mm});
            skLineSegment(sketch, "E433", {"start": v(20.04, 52.1) * mm, "end": v(19.88, 51.74) * mm});
            skLineSegment(sketch, "E434", {"start": v(19.88, 51.74) * mm, "end": v(19.73, 51.38) * mm});
            skLineSegment(sketch, "E435", {"start": v(19.73, 51.38) * mm, "end": v(19.58, 51) * mm});
            skLineSegment(sketch, "E436", {"start": v(19.58, 51) * mm, "end": v(19.42, 50.65) * mm});
            skLineSegment(sketch, "E437", {"start": v(19.42, 50.65) * mm, "end": v(19.27, 50.28) * mm});
            skLineSegment(sketch, "E438", {"start": v(19.27, 50.28) * mm, "end": v(19.11, 49.92) * mm});
            skLineSegment(sketch, "E439", {"start": v(19.11, 49.92) * mm, "end": v(18.96, 49.55) * mm});
            skLineSegment(sketch, "E440", {"start": v(18.96, 49.55) * mm, "end": v(18.8, 49.2) * mm});
            skLineSegment(sketch, "E441", {"start": v(18.8, 49.2) * mm, "end": v(18.65, 48.82) * mm});
            skLineSegment(sketch, "E442", {"start": v(18.65, 48.82) * mm, "end": v(18.5, 48.46) * mm});
            skLineSegment(sketch, "E443", {"start": v(18.5, 48.46) * mm, "end": v(18.34, 48.1) * mm});
            skLineSegment(sketch, "E444", {"start": v(18.34, 48.1) * mm, "end": v(18.19, 47.73) * mm});
            skLineSegment(sketch, "E445", {"start": v(18.19, 47.73) * mm, "end": v(18.06, 47.42) * mm});
            skLineSegment(sketch, "E446", {"start": v(18.06, 47.42) * mm, "end": v(17.69, 47.56) * mm});
            skLineSegment(sketch, "E447", {"start": v(17.69, 47.56) * mm, "end": v(17.32, 47.7) * mm});
            skLineSegment(sketch, "E448", {"start": v(17.32, 47.7) * mm, "end": v(16.95, 47.83) * mm});
            skLineSegment(sketch, "E449", {"start": v(16.95, 47.83) * mm, "end": v(16.58, 47.97) * mm});
            skLineSegment(sketch, "E450", {"start": v(16.58, 47.97) * mm, "end": v(16.21, 48.1) * mm});
            skLineSegment(sketch, "E451", {"start": v(16.21, 48.1) * mm, "end": v(15.84, 48.24) * mm});
            skLineSegment(sketch, "E452", {"start": v(15.84, 48.24) * mm, "end": v(15.47, 48.38) * mm});
            skLineSegment(sketch, "E453", {"start": v(15.47, 48.38) * mm, "end": v(15.1, 48.52) * mm});
            skLineSegment(sketch, "E454", {"start": v(15.1, 48.52) * mm, "end": v(14.74, 48.66) * mm});
            skLineSegment(sketch, "E455", {"start": v(14.74, 48.66) * mm, "end": v(14.37, 48.8) * mm});
            skLineSegment(sketch, "E456", {"start": v(14.37, 48.8) * mm, "end": v(14, 48.93) * mm});
            skLineSegment(sketch, "E457", {"start": v(14, 48.93) * mm, "end": v(13.91, 48.96) * mm});
            skLineSegment(sketch, "E458", {"start": v(13.91, 48.96) * mm, "end": v(14.03, 49.34) * mm});
            skLineSegment(sketch, "E459", {"start": v(14.03, 49.34) * mm, "end": v(14.16, 49.71) * mm});
            skLineSegment(sketch, "E460", {"start": v(14.16, 49.71) * mm, "end": v(14.28, 50.1) * mm});
            skLineSegment(sketch, "E461", {"start": v(14.28, 50.1) * mm, "end": v(14.4, 50.47) * mm});
            skLineSegment(sketch, "E462", {"start": v(14.4, 50.47) * mm, "end": v(14.52, 50.84) * mm});
            skLineSegment(sketch, "E463", {"start": v(14.52, 50.84) * mm, "end": v(14.65, 51.22) * mm});
            skLineSegment(sketch, "E464", {"start": v(14.65, 51.22) * mm, "end": v(14.77, 51.6) * mm});
            skLineSegment(sketch, "E465", {"start": v(14.77, 51.6) * mm, "end": v(14.89, 51.97) * mm});
            skLineSegment(sketch, "E466", {"start": v(14.89, 51.97) * mm, "end": v(15.01, 52.35) * mm});
            skLineSegment(sketch, "E467", {"start": v(15.01, 52.35) * mm, "end": v(15.13, 52.72) * mm});
            skLineSegment(sketch, "E468", {"start": v(15.13, 52.72) * mm, "end": v(15.26, 53.1) * mm});
            skLineSegment(sketch, "E469", {"start": v(15.26, 53.1) * mm, "end": v(15.38, 53.48) * mm});
            skLineSegment(sketch, "E470", {"start": v(15.38, 53.48) * mm, "end": v(15.5, 53.88) * mm});
            skLineSegment(sketch, "E471", {"start": v(15.5, 53.88) * mm, "end": v(15.55, 54.3) * mm});
            skLineSegment(sketch, "E472", {"start": v(15.55, 54.3) * mm, "end": v(15.5, 54.72) * mm});
            skLineSegment(sketch, "E473", {"start": v(15.5, 54.72) * mm, "end": v(15.32, 55.1) * mm});
            skLineSegment(sketch, "E474", {"start": v(15.32, 55.1) * mm, "end": v(15.06, 55.44) * mm});
            skLineSegment(sketch, "E475", {"start": v(15.06, 55.44) * mm, "end": v(14.71, 55.69) * mm});
            skLineSegment(sketch, "E476", {"start": v(14.71, 55.69) * mm, "end": v(14.4, 55.82) * mm});
            skLineSegment(sketch, "E477", {"start": v(14.4, 55.82) * mm, "end": v(13.98, 55.88) * mm});
            skLineSegment(sketch, "E478", {"start": v(13.98, 55.88) * mm, "end": v(13.56, 55.84) * mm});
            skLineSegment(sketch, "E479", {"start": v(13.56, 55.84) * mm, "end": v(13.17, 55.68) * mm});
            skLineSegment(sketch, "E480", {"start": v(13.17, 55.68) * mm, "end": v(12.83, 55.43) * mm});
            skLineSegment(sketch, "E481", {"start": v(12.83, 55.43) * mm, "end": v(12.56, 55.1) * mm});
            skLineSegment(sketch, "E482", {"start": v(12.56, 55.1) * mm, "end": v(12.4, 54.7) * mm});
            skLineSegment(sketch, "E483", {"start": v(12.4, 54.7) * mm, "end": v(12.3, 54.33) * mm});
            skLineSegment(sketch, "E484", {"start": v(12.3, 54.33) * mm, "end": v(12.2, 53.95) * mm});
            skLineSegment(sketch, "E485", {"start": v(12.2, 53.95) * mm, "end": v(12.1, 53.56) * mm});
            skLineSegment(sketch, "E486", {"start": v(12.1, 53.56) * mm, "end": v(12, 53.18) * mm});
            skLineSegment(sketch, "E487", {"start": v(12, 53.18) * mm, "end": v(11.9, 52.8) * mm});
            skLineSegment(sketch, "E488", {"start": v(11.9, 52.8) * mm, "end": v(11.8, 52.41) * mm});
            skLineSegment(sketch, "E489", {"start": v(11.8, 52.41) * mm, "end": v(11.7, 52.03) * mm});
            skLineSegment(sketch, "E490", {"start": v(11.7, 52.03) * mm, "end": v(11.6, 51.65) * mm});
            skLineSegment(sketch, "E491", {"start": v(11.6, 51.65) * mm, "end": v(11.5, 51.26) * mm});
            skLineSegment(sketch, "E492", {"start": v(11.5, 51.26) * mm, "end": v(11.4, 50.88) * mm});
            skLineSegment(sketch, "E493", {"start": v(11.4, 50.88) * mm, "end": v(11.3, 50.5) * mm});
            skLineSegment(sketch, "E494", {"start": v(11.3, 50.5) * mm, "end": v(11.2, 50.12) * mm});
            skLineSegment(sketch, "E495", {"start": v(11.2, 50.12) * mm, "end": v(11.1, 49.79) * mm});
            skLineSegment(sketch, "E496", {"start": v(11.1, 49.79) * mm, "end": v(10.72, 49.87) * mm});
            skLineSegment(sketch, "E497", {"start": v(10.72, 49.87) * mm, "end": v(10.33, 49.96) * mm});
            skLineSegment(sketch, "E498", {"start": v(10.33, 49.96) * mm, "end": v(9.95, 50.04) * mm});
            skLineSegment(sketch, "E499", {"start": v(9.95, 50.04) * mm, "end": v(9.57, 50.12) * mm});
            skLineSegment(sketch, "E500", {"start": v(9.57, 50.12) * mm, "end": v(9.18, 50.2) * mm});
            skLineSegment(sketch, "E501", {"start": v(9.18, 50.2) * mm, "end": v(8.8, 50.3) * mm});
            skLineSegment(sketch, "E502", {"start": v(8.8, 50.3) * mm, "end": v(8.41, 50.37) * mm});
            skLineSegment(sketch, "E503", {"start": v(8.41, 50.37) * mm, "end": v(8.03, 50.46) * mm});
            skLineSegment(sketch, "E504", {"start": v(8.03, 50.46) * mm, "end": v(7.64, 50.54) * mm});
            skLineSegment(sketch, "E505", {"start": v(7.64, 50.54) * mm, "end": v(7.26, 50.63) * mm});
            skLineSegment(sketch, "E506", {"start": v(7.26, 50.63) * mm, "end": v(6.87, 50.7) * mm});
            skLineSegment(sketch, "E507", {"start": v(6.87, 50.7) * mm, "end": v(6.78, 50.73) * mm});
            skLineSegment(sketch, "E508", {"start": v(6.78, 50.73) * mm, "end": v(6.85, 51.12) * mm});
            skLineSegment(sketch, "E509", {"start": v(6.85, 51.12) * mm, "end": v(6.92, 51.5) * mm});
            skLineSegment(sketch, "E510", {"start": v(6.92, 51.5) * mm, "end": v(6.98, 51.9) * mm});
            skLineSegment(sketch, "E511", {"start": v(6.98, 51.9) * mm, "end": v(7.05, 52.29) * mm});
            skLineSegment(sketch, "E512", {"start": v(7.05, 52.29) * mm, "end": v(7.12, 52.67) * mm});
            skLineSegment(sketch, "E513", {"start": v(7.12, 52.67) * mm, "end": v(7.19, 53.07) * mm});
            skLineSegment(sketch, "E514", {"start": v(7.19, 53.07) * mm, "end": v(7.25, 53.46) * mm});
            skLineSegment(sketch, "E515", {"start": v(7.25, 53.46) * mm, "end": v(7.32, 53.84) * mm});
            skLineSegment(sketch, "E516", {"start": v(7.32, 53.84) * mm, "end": v(7.39, 54.24) * mm});
            skLineSegment(sketch, "E517", {"start": v(7.39, 54.24) * mm, "end": v(7.46, 54.62) * mm});
            skLineSegment(sketch, "E518", {"start": v(7.46, 54.62) * mm, "end": v(7.52, 55.01) * mm});
            skLineSegment(sketch, "E519", {"start": v(7.52, 55.01) * mm, "end": v(7.6, 55.4) * mm});
            skLineSegment(sketch, "E520", {"start": v(7.6, 55.4) * mm, "end": v(7.66, 55.82) * mm});
            skLineSegment(sketch, "E521", {"start": v(7.66, 55.82) * mm, "end": v(7.65, 56.25) * mm});
            skLineSegment(sketch, "E522", {"start": v(7.65, 56.25) * mm, "end": v(7.53, 56.65) * mm});
            skLineSegment(sketch, "E523", {"start": v(7.53, 56.65) * mm, "end": v(7.3, 57.01) * mm});
            skLineSegment(sketch, "E524", {"start": v(7.3, 57.01) * mm, "end": v(7, 57.3) * mm});
            skLineSegment(sketch, "E525", {"start": v(7, 57.3) * mm, "end": v(6.62, 57.5) * mm});
            skLineSegment(sketch, "E526", {"start": v(6.62, 57.5) * mm, "end": v(6.29, 57.58) * mm});
            skLineSegment(sketch, "E527", {"start": v(6.29, 57.58) * mm, "end": v(6.04, 57.6) * mm});
            skLineSegment(sketch, "E528", {"start": v(6.04, 57.6) * mm, "end": v(5.62, 57.54) * mm});
            skLineSegment(sketch, "E529", {"start": v(5.62, 57.54) * mm, "end": v(5.23, 57.37) * mm});
            skLineSegment(sketch, "E530", {"start": v(5.23, 57.37) * mm, "end": v(4.9, 57.1) * mm});
            skLineSegment(sketch, "E531", {"start": v(4.9, 57.1) * mm, "end": v(4.65, 56.76) * mm});
            skLineSegment(sketch, "E532", {"start": v(4.65, 56.76) * mm, "end": v(4.5, 56.36) * mm});
            skLineSegment(sketch, "E533", {"start": v(4.5, 56.36) * mm, "end": v(4.47, 56.2) * mm});
            skLineSegment(sketch, "E534", {"start": v(4.47, 56.2) * mm, "end": v(4.42, 55.8) * mm});
            skLineSegment(sketch, "E535", {"start": v(4.42, 55.8) * mm, "end": v(4.38, 55.42) * mm});
            skLineSegment(sketch, "E536", {"start": v(4.38, 55.42) * mm, "end": v(4.33, 55.02) * mm});
            skLineSegment(sketch, "E537", {"start": v(4.33, 55.02) * mm, "end": v(4.29, 54.63) * mm});
            skLineSegment(sketch, "E538", {"start": v(4.29, 54.63) * mm, "end": v(4.24, 54.24) * mm});
            skLineSegment(sketch, "E539", {"start": v(4.24, 54.24) * mm, "end": v(4.2, 53.84) * mm});
            skLineSegment(sketch, "E540", {"start": v(4.2, 53.84) * mm, "end": v(4.15, 53.45) * mm});
            skLineSegment(sketch, "E541", {"start": v(4.15, 53.45) * mm, "end": v(4.1, 53.06) * mm});
            skLineSegment(sketch, "E542", {"start": v(4.1, 53.06) * mm, "end": v(4.06, 52.66) * mm});
            skLineSegment(sketch, "E543", {"start": v(4.06, 52.66) * mm, "end": v(4.01, 52.27) * mm});
            skLineSegment(sketch, "E544", {"start": v(4.01, 52.27) * mm, "end": v(3.97, 51.88) * mm});
            skLineSegment(sketch, "E545", {"start": v(3.97, 51.88) * mm, "end": v(3.92, 51.48) * mm});
            skLineSegment(sketch, "E546", {"start": v(3.92, 51.48) * mm, "end": v(3.89, 51.15) * mm});
            skLineSegment(sketch, "E547", {"start": v(3.89, 51.15) * mm, "end": v(3.5, 51.17) * mm});
            skLineSegment(sketch, "E548", {"start": v(3.5, 51.17) * mm, "end": v(3.1, 51.2) * mm});
            skLineSegment(sketch, "E549", {"start": v(3.1, 51.2) * mm, "end": v(2.7, 51.23) * mm});
            skLineSegment(sketch, "E550", {"start": v(2.7, 51.23) * mm, "end": v(2.31, 51.26) * mm});
            skLineSegment(sketch, "E551", {"start": v(2.31, 51.26) * mm, "end": v(1.92, 51.29) * mm});
            skLineSegment(sketch, "E552", {"start": v(1.92, 51.29) * mm, "end": v(1.53, 51.31) * mm});
            skLineSegment(sketch, "E553", {"start": v(1.53, 51.31) * mm, "end": v(1.14, 51.34) * mm});
            skLineSegment(sketch, "E554", {"start": v(1.14, 51.34) * mm, "end": v(0.74, 51.37) * mm});
            skLineSegment(sketch, "E555", {"start": v(0.74, 51.37) * mm, "end": v(0.35, 51.4) * mm});
            skLineSegment(sketch, "E556", {"start": v(0.35, 51.4) * mm, "end": v(-0.04, 51.43) * mm});
            skLineSegment(sketch, "E557", {"start": v(-0.04, 51.43) * mm, "end": v(-0.44, 51.45) * mm});
            skLineSegment(sketch, "E558", {"start": v(-0.44, 51.45) * mm, "end": v(-0.53, 51.46) * mm});
            skLineSegment(sketch, "E559", {"start": v(-0.53, 51.46) * mm, "end": v(-0.52, 51.85) * mm});
            skLineSegment(sketch, "E560", {"start": v(-0.52, 51.85) * mm, "end": v(-0.5, 52.25) * mm});
            skLineSegment(sketch, "E561", {"start": v(-0.5, 52.25) * mm, "end": v(-0.5, 52.65) * mm});
            skLineSegment(sketch, "E562", {"start": v(-0.5, 52.65) * mm, "end": v(-0.48, 53.04) * mm});
            skLineSegment(sketch, "E563", {"start": v(-0.48, 53.04) * mm, "end": v(-0.47, 53.43) * mm});
            skLineSegment(sketch, "E564", {"start": v(-0.47, 53.43) * mm, "end": v(-0.46, 53.83) * mm});
            skLineSegment(sketch, "E565", {"start": v(-0.46, 53.83) * mm, "end": v(-0.45, 54.23) * mm});
            skLineSegment(sketch, "E566", {"start": v(-0.45, 54.23) * mm, "end": v(-0.44, 54.62) * mm});
            skLineSegment(sketch, "E567", {"start": v(-0.44, 54.62) * mm, "end": v(-0.43, 55.02) * mm});
            skLineSegment(sketch, "E568", {"start": v(-0.43, 55.02) * mm, "end": v(-0.41, 55.41) * mm});
            skLineSegment(sketch, "E569", {"start": v(-0.41, 55.41) * mm, "end": v(-0.4, 55.8) * mm});
            skLineSegment(sketch, "E570", {"start": v(-0.4, 55.8) * mm, "end": v(-0.4, 56.2) * mm});
            skLineSegment(sketch, "E571", {"start": v(-0.4, 56.2) * mm, "end": v(-0.38, 56.63) * mm});
            skLineSegment(sketch, "E572", {"start": v(-0.38, 56.63) * mm, "end": v(-0.46, 57.05) * mm});
            skLineSegment(sketch, "E573", {"start": v(-0.46, 57.05) * mm, "end": v(-0.63, 57.43) * mm});
            skLineSegment(sketch, "E574", {"start": v(-0.63, 57.43) * mm, "end": v(-0.9, 57.75) * mm});
            skLineSegment(sketch, "E575", {"start": v(-0.9, 57.75) * mm, "end": v(-1.25, 58) * mm});
            skLineSegment(sketch, "E576", {"start": v(-1.25, 58) * mm, "end": v(-1.65, 58.14) * mm});
            skLineSegment(sketch, "E577", {"start": v(-1.65, 58.14) * mm, "end": v(-2, 58.17) * mm});
            skLineSegment(sketch, "E578", {"start": v(-2, 58.17) * mm, "end": v(-2.4, 58.12) * mm});
            skLineSegment(sketch, "E579", {"start": v(-2.4, 58.12) * mm, "end": v(-2.8, 57.96) * mm});
            skLineSegment(sketch, "E580", {"start": v(-2.8, 57.96) * mm, "end": v(-3.14, 57.7) * mm});
            skLineSegment(sketch, "E581", {"start": v(-3.14, 57.7) * mm, "end": v(-3.4, 57.36) * mm});
            skLineSegment(sketch, "E582", {"start": v(-3.4, 57.36) * mm, "end": v(-3.55, 56.97) * mm});
            skLineSegment(sketch, "E583", {"start": v(-3.55, 56.97) * mm, "end": v(-3.6, 56.54) * mm});
            skLineSegment(sketch, "E584", {"start": v(-3.6, 56.54) * mm, "end": v(-3.59, 56.15) * mm});
            skLineSegment(sketch, "E585", {"start": v(-3.59, 56.15) * mm, "end": v(-3.58, 55.76) * mm});
            skLineSegment(sketch, "E586", {"start": v(-3.58, 55.76) * mm, "end": v(-3.56, 55.36) * mm});
            skLineSegment(sketch, "E587", {"start": v(-3.56, 55.36) * mm, "end": v(-3.55, 54.96) * mm});
            skLineSegment(sketch, "E588", {"start": v(-3.55, 54.96) * mm, "end": v(-3.54, 54.57) * mm});
            skLineSegment(sketch, "E589", {"start": v(-3.54, 54.57) * mm, "end": v(-3.53, 54.17) * mm});
            skLineSegment(sketch, "E590", {"start": v(-3.53, 54.17) * mm, "end": v(-3.52, 53.78) * mm});
            skLineSegment(sketch, "E591", {"start": v(-3.52, 53.78) * mm, "end": v(-3.5, 53.39) * mm});
            skLineSegment(sketch, "E592", {"start": v(-3.5, 53.39) * mm, "end": v(-3.5, 52.99) * mm});
            skLineSegment(sketch, "E593", {"start": v(-3.5, 52.99) * mm, "end": v(-3.49, 52.6) * mm});
            skLineSegment(sketch, "E594", {"start": v(-3.49, 52.6) * mm, "end": v(-3.47, 52.2) * mm});
            skLineSegment(sketch, "E595", {"start": v(-3.47, 52.2) * mm, "end": v(-3.46, 51.8) * mm});
            skLineSegment(sketch, "E596", {"start": v(-3.46, 51.8) * mm, "end": v(-3.45, 51.46) * mm});
            skLineSegment(sketch, "E597", {"start": v(-3.45, 51.46) * mm, "end": v(-3.85, 51.43) * mm});
            skLineSegment(sketch, "E598", {"start": v(-3.85, 51.43) * mm, "end": v(-4.24, 51.4) * mm});
            skLineSegment(sketch, "E599", {"start": v(-4.24, 51.4) * mm, "end": v(-4.63, 51.38) * mm});
            skLineSegment(sketch, "E600", {"start": v(-4.63, 51.38) * mm, "end": v(-5.02, 51.35) * mm});
            skLineSegment(sketch, "E601", {"start": v(-5.02, 51.35) * mm, "end": v(-5.42, 51.32) * mm});
            skLineSegment(sketch, "E602", {"start": v(-5.42, 51.32) * mm, "end": v(-5.81, 51.3) * mm});
            skLineSegment(sketch, "E603", {"start": v(-5.81, 51.3) * mm, "end": v(-6.2, 51.26) * mm});
            skLineSegment(sketch, "E604", {"start": v(-6.2, 51.26) * mm, "end": v(-6.6, 51.24) * mm});
            skLineSegment(sketch, "E605", {"start": v(-6.6, 51.24) * mm, "end": v(-6.99, 51.2) * mm});
            skLineSegment(sketch, "E606", {"start": v(-6.99, 51.2) * mm, "end": v(-7.38, 51.18) * mm});
            skLineSegment(sketch, "E607", {"start": v(-7.38, 51.18) * mm, "end": v(-7.77, 51.15) * mm});
            skLineSegment(sketch, "E608", {"start": v(-7.77, 51.15) * mm, "end": v(-7.87, 51.15) * mm});
            skLineSegment(sketch, "E609", {"start": v(-7.87, 51.15) * mm, "end": v(-7.91, 51.54) * mm});
            skLineSegment(sketch, "E610", {"start": v(-7.91, 51.54) * mm, "end": v(-7.96, 51.93) * mm});
            skLineSegment(sketch, "E611", {"start": v(-7.96, 51.93) * mm, "end": v(-8, 52.32) * mm});
            skLineSegment(sketch, "E612", {"start": v(-8, 52.32) * mm, "end": v(-8.05, 52.72) * mm});
            skLineSegment(sketch, "E613", {"start": v(-8.05, 52.72) * mm, "end": v(-8.1, 53.1) * mm});
            skLineSegment(sketch, "E614", {"start": v(-8.1, 53.1) * mm, "end": v(-8.14, 53.5) * mm});
            skLineSegment(sketch, "E615", {"start": v(-8.14, 53.5) * mm, "end": v(-8.18, 53.9) * mm});
            skLineSegment(sketch, "E616", {"start": v(-8.18, 53.9) * mm, "end": v(-8.23, 54.29) * mm});
            skLineSegment(sketch, "E617", {"start": v(-8.23, 54.29) * mm, "end": v(-8.27, 54.68) * mm});
            skLineSegment(sketch, "E618", {"start": v(-8.27, 54.68) * mm, "end": v(-8.32, 55.07) * mm});
            skLineSegment(sketch, "E619", {"start": v(-8.32, 55.07) * mm, "end": v(-8.36, 55.46) * mm});
            skLineSegment(sketch, "E620", {"start": v(-8.36, 55.46) * mm, "end": v(-8.4, 55.86) * mm});
            skLineSegment(sketch, "E621", {"start": v(-8.4, 55.86) * mm, "end": v(-8.46, 56.28) * mm});
            skLineSegment(sketch, "E622", {"start": v(-8.46, 56.28) * mm, "end": v(-8.59, 56.68) * mm});
            skLineSegment(sketch, "E623", {"start": v(-8.59, 56.68) * mm, "end": v(-8.82, 57.04) * mm});
            skLineSegment(sketch, "E624", {"start": v(-8.82, 57.04) * mm, "end": v(-9.14, 57.32) * mm});
            skLineSegment(sketch, "E625", {"start": v(-9.14, 57.32) * mm, "end": v(-9.52, 57.51) * mm});
            skLineSegment(sketch, "E626", {"start": v(-9.52, 57.51) * mm, "end": v(-9.93, 57.6) * mm});
            skLineSegment(sketch, "E627", {"start": v(-9.93, 57.6) * mm, "end": v(-10.02, 57.6) * mm});
            skLineSegment(sketch, "E628", {"start": v(-10.02, 57.6) * mm, "end": v(-10.27, 57.58) * mm});
            skLineSegment(sketch, "E629", {"start": v(-10.27, 57.58) * mm, "end": v(-10.68, 57.47) * mm});
            skLineSegment(sketch, "E630", {"start": v(-10.68, 57.47) * mm, "end": v(-11.04, 57.25) * mm});
            skLineSegment(sketch, "E631", {"start": v(-11.04, 57.25) * mm, "end": v(-11.33, 56.95) * mm});
            skLineSegment(sketch, "E632", {"start": v(-11.33, 56.95) * mm, "end": v(-11.54, 56.57) * mm});
            skLineSegment(sketch, "E633", {"start": v(-11.54, 56.57) * mm, "end": v(-11.64, 56.16) * mm});
            skLineSegment(sketch, "E634", {"start": v(-11.64, 56.16) * mm, "end": v(-11.63, 55.74) * mm});
            skLineSegment(sketch, "E635", {"start": v(-11.63, 55.74) * mm, "end": v(-11.56, 55.35) * mm});
            skLineSegment(sketch, "E636", {"start": v(-11.56, 55.35) * mm, "end": v(-11.5, 54.96) * mm});
            skLineSegment(sketch, "E637", {"start": v(-11.5, 54.96) * mm, "end": v(-11.43, 54.57) * mm});
            skLineSegment(sketch, "E638", {"start": v(-11.43, 54.57) * mm, "end": v(-11.36, 54.18) * mm});
            skLineSegment(sketch, "E639", {"start": v(-11.36, 54.18) * mm, "end": v(-11.3, 53.8) * mm});
            skLineSegment(sketch, "E640", {"start": v(-11.3, 53.8) * mm, "end": v(-11.22, 53.4) * mm});
            skLineSegment(sketch, "E641", {"start": v(-11.22, 53.4) * mm, "end": v(-11.16, 53.01) * mm});
            skLineSegment(sketch, "E642", {"start": v(-11.16, 53.01) * mm, "end": v(-11.1, 52.63) * mm});
            skLineSegment(sketch, "E643", {"start": v(-11.1, 52.63) * mm, "end": v(-11.02, 52.23) * mm});
            skLineSegment(sketch, "E644", {"start": v(-11.02, 52.23) * mm, "end": v(-10.96, 51.84) * mm});
            skLineSegment(sketch, "E645", {"start": v(-10.96, 51.84) * mm, "end": v(-10.89, 51.46) * mm});
            skLineSegment(sketch, "E646", {"start": v(-10.89, 51.46) * mm, "end": v(-10.82, 51.06) * mm});
            skLineSegment(sketch, "E647", {"start": v(-10.82, 51.06) * mm, "end": v(-10.76, 50.73) * mm});
            skLineSegment(sketch, "E648", {"start": v(-10.76, 50.73) * mm, "end": v(-11.15, 50.65) * mm});
            skLineSegment(sketch, "E649", {"start": v(-11.15, 50.65) * mm, "end": v(-11.53, 50.56) * mm});
            skLineSegment(sketch, "E650", {"start": v(-11.53, 50.56) * mm, "end": v(-11.92, 50.48) * mm});
            skLineSegment(sketch, "E651", {"start": v(-11.92, 50.48) * mm, "end": v(-12.3, 50.4) * mm});
            skLineSegment(sketch, "E652", {"start": v(-12.3, 50.4) * mm, "end": v(-12.69, 50.31) * mm});
            skLineSegment(sketch, "E653", {"start": v(-12.69, 50.31) * mm, "end": v(-13.07, 50.23) * mm});
            skLineSegment(sketch, "E654", {"start": v(-13.07, 50.23) * mm, "end": v(-13.46, 50.14) * mm});
            skLineSegment(sketch, "E655", {"start": v(-13.46, 50.14) * mm, "end": v(-13.84, 50.06) * mm});
            skLineSegment(sketch, "E656", {"start": v(-13.84, 50.06) * mm, "end": v(-14.23, 49.98) * mm});
            skLineSegment(sketch, "E657", {"start": v(-14.23, 49.98) * mm, "end": v(-14.61, 49.9) * mm});
            skLineSegment(sketch, "E658", {"start": v(-14.61, 49.9) * mm, "end": v(-15, 49.8) * mm});
            skLineSegment(sketch, "E659", {"start": v(-15, 49.8) * mm, "end": v(-15.08, 49.79) * mm});
            skLineSegment(sketch, "E660", {"start": v(-15.08, 49.79) * mm, "end": v(-15.19, 50.17) * mm});
            skLineSegment(sketch, "E661", {"start": v(-15.19, 50.17) * mm, "end": v(-15.29, 50.55) * mm});
            skLineSegment(sketch, "E662", {"start": v(-15.29, 50.55) * mm, "end": v(-15.39, 50.94) * mm});
            skLineSegment(sketch, "E663", {"start": v(-15.39, 50.94) * mm, "end": v(-15.49, 51.32) * mm});
            skLineSegment(sketch, "E664", {"start": v(-15.49, 51.32) * mm, "end": v(-15.59, 51.7) * mm});
            skLineSegment(sketch, "E665", {"start": v(-15.59, 51.7) * mm, "end": v(-15.69, 52.08) * mm});
            skLineSegment(sketch, "E666", {"start": v(-15.69, 52.08) * mm, "end": v(-15.79, 52.46) * mm});
            skLineSegment(sketch, "E667", {"start": v(-15.79, 52.46) * mm, "end": v(-15.89, 52.85) * mm});
            skLineSegment(sketch, "E668", {"start": v(-15.89, 52.85) * mm, "end": v(-16, 53.23) * mm});
            skLineSegment(sketch, "E669", {"start": v(-16, 53.23) * mm, "end": v(-16.1, 53.61) * mm});
            skLineSegment(sketch, "E670", {"start": v(-16.1, 53.61) * mm, "end": v(-16.2, 54) * mm});
            skLineSegment(sketch, "E671", {"start": v(-16.2, 54) * mm, "end": v(-16.3, 54.38) * mm});
            skLineSegment(sketch, "E672", {"start": v(-16.3, 54.38) * mm, "end": v(-16.4, 54.79) * mm});
            skLineSegment(sketch, "E673", {"start": v(-16.4, 54.79) * mm, "end": v(-16.59, 55.17) * mm});
            skLineSegment(sketch, "E674", {"start": v(-16.59, 55.17) * mm, "end": v(-16.87, 55.49) * mm});
            skLineSegment(sketch, "E675", {"start": v(-16.87, 55.49) * mm, "end": v(-17.22, 55.72) * mm});
            skLineSegment(sketch, "E676", {"start": v(-17.22, 55.72) * mm, "end": v(-17.62, 55.85) * mm});
            skLineSegment(sketch, "E677", {"start": v(-17.62, 55.85) * mm, "end": v(-17.96, 55.88) * mm});
            skLineSegment(sketch, "E678", {"start": v(-17.96, 55.88) * mm, "end": v(-18.38, 55.82) * mm});
            skLineSegment(sketch, "E679", {"start": v(-18.38, 55.82) * mm, "end": v(-18.77, 55.65) * mm});
            skLineSegment(sketch, "E680", {"start": v(-18.77, 55.65) * mm, "end": v(-19.1, 55.38) * mm});
            skLineSegment(sketch, "E681", {"start": v(-19.1, 55.38) * mm, "end": v(-19.34, 55.04) * mm});
            skLineSegment(sketch, "E682", {"start": v(-19.34, 55.04) * mm, "end": v(-19.5, 54.64) * mm});
            skLineSegment(sketch, "E683", {"start": v(-19.5, 54.64) * mm, "end": v(-19.53, 54.22) * mm});
            skLineSegment(sketch, "E684", {"start": v(-19.53, 54.22) * mm, "end": v(-19.46, 53.8) * mm});
            skLineSegment(sketch, "E685", {"start": v(-19.46, 53.8) * mm, "end": v(-19.34, 53.43) * mm});
            skLineSegment(sketch, "E686", {"start": v(-19.34, 53.43) * mm, "end": v(-19.22, 53.05) * mm});
            skLineSegment(sketch, "E687", {"start": v(-19.22, 53.05) * mm, "end": v(-19.1, 52.67) * mm});
            skLineSegment(sketch, "E688", {"start": v(-19.1, 52.67) * mm, "end": v(-18.98, 52.3) * mm});
            skLineSegment(sketch, "E689", {"start": v(-18.98, 52.3) * mm, "end": v(-18.85, 51.92) * mm});
            skLineSegment(sketch, "E690", {"start": v(-18.85, 51.92) * mm, "end": v(-18.73, 51.54) * mm});
            skLineSegment(sketch, "E691", {"start": v(-18.73, 51.54) * mm, "end": v(-18.6, 51.17) * mm});
            skLineSegment(sketch, "E692", {"start": v(-18.6, 51.17) * mm, "end": v(-18.49, 50.8) * mm});
            skLineSegment(sketch, "E693", {"start": v(-18.49, 50.8) * mm, "end": v(-18.36, 50.42) * mm});
            skLineSegment(sketch, "E694", {"start": v(-18.36, 50.42) * mm, "end": v(-18.24, 50.04) * mm});
            skLineSegment(sketch, "E695", {"start": v(-18.24, 50.04) * mm, "end": v(-18.12, 49.67) * mm});
            skLineSegment(sketch, "E696", {"start": v(-18.12, 49.67) * mm, "end": v(-18, 49.29) * mm});
            skLineSegment(sketch, "E697", {"start": v(-18, 49.29) * mm, "end": v(-17.9, 48.96) * mm});
            skLineSegment(sketch, "E698", {"start": v(-17.9, 48.96) * mm, "end": v(-18.26, 48.83) * mm});
            skLineSegment(sketch, "E699", {"start": v(-18.26, 48.83) * mm, "end": v(-18.63, 48.69) * mm});
            skLineSegment(sketch, "E700", {"start": v(-18.63, 48.69) * mm, "end": v(-19, 48.55) * mm});
            skLineSegment(sketch, "E701", {"start": v(-19, 48.55) * mm, "end": v(-19.37, 48.41) * mm});
            skLineSegment(sketch, "E702", {"start": v(-19.37, 48.41) * mm, "end": v(-19.74, 48.28) * mm});
            skLineSegment(sketch, "E703", {"start": v(-19.74, 48.28) * mm, "end": v(-20.1, 48.14) * mm});
            skLineSegment(sketch, "E704", {"start": v(-20.1, 48.14) * mm, "end": v(-20.48, 48) * mm});
            skLineSegment(sketch, "E705", {"start": v(-20.48, 48) * mm, "end": v(-20.84, 47.86) * mm});
            skLineSegment(sketch, "E706", {"start": v(-20.84, 47.86) * mm, "end": v(-21.21, 47.73) * mm});
            skLineSegment(sketch, "E707", {"start": v(-21.21, 47.73) * mm, "end": v(-21.58, 47.59) * mm});
            skLineSegment(sketch, "E708", {"start": v(-21.58, 47.59) * mm, "end": v(-21.95, 47.45) * mm});
            skLineSegment(sketch, "E709", {"start": v(-21.95, 47.45) * mm, "end": v(-22.04, 47.42) * mm});
            skLineSegment(sketch, "E710", {"start": v(-22.04, 47.42) * mm, "end": v(-22.2, 47.78) * mm});
            skLineSegment(sketch, "E711", {"start": v(-22.2, 47.78) * mm, "end": v(-22.34, 48.14) * mm});
            skLineSegment(sketch, "E712", {"start": v(-22.34, 48.14) * mm, "end": v(-22.5, 48.51) * mm});
            skLineSegment(sketch, "E713", {"start": v(-22.5, 48.51) * mm, "end": v(-22.65, 48.87) * mm});
            skLineSegment(sketch, "E714", {"start": v(-22.65, 48.87) * mm, "end": v(-22.8, 49.24) * mm});
            skLineSegment(sketch, "E715", {"start": v(-22.8, 49.24) * mm, "end": v(-22.96, 49.6) * mm});
            skLineSegment(sketch, "E716", {"start": v(-22.96, 49.6) * mm, "end": v(-23.11, 49.97) * mm});
            skLineSegment(sketch, "E717", {"start": v(-23.11, 49.97) * mm, "end": v(-23.27, 50.33) * mm});
            skLineSegment(sketch, "E718", {"start": v(-23.27, 50.33) * mm, "end": v(-23.42, 50.7) * mm});
            skLineSegment(sketch, "E719", {"start": v(-23.42, 50.7) * mm, "end": v(-23.58, 51.06) * mm});
            skLineSegment(sketch, "E720", {"start": v(-23.58, 51.06) * mm, "end": v(-23.73, 51.42) * mm});
            skLineSegment(sketch, "E721", {"start": v(-23.73, 51.42) * mm, "end": v(-23.89, 51.8) * mm});
            skLineSegment(sketch, "E722", {"start": v(-23.89, 51.8) * mm, "end": v(-24.05, 52.18) * mm});
            skLineSegment(sketch, "E723", {"start": v(-24.05, 52.18) * mm, "end": v(-24.3, 52.53) * mm});
            skLineSegment(sketch, "E724", {"start": v(-24.3, 52.53) * mm, "end": v(-24.61, 52.8) * mm});
            skLineSegment(sketch, "E725", {"start": v(-24.61, 52.8) * mm, "end": v(-25, 52.99) * mm});
            skLineSegment(sketch, "E726", {"start": v(-25, 52.99) * mm, "end": v(-25.41, 53.06) * mm});
            skLineSegment(sketch, "E727", {"start": v(-25.41, 53.06) * mm, "end": v(-25.5, 53.06) * mm});
            skLineSegment(sketch, "E728", {"start": v(-25.5, 53.06) * mm, "end": v(-25.92, 53) * mm});
            skLineSegment(sketch, "E729", {"start": v(-25.92, 53) * mm, "end": v(-26.16, 52.92) * mm});
            skLineSegment(sketch, "E730", {"start": v(-26.16, 52.92) * mm, "end": v(-26.52, 52.7) * mm});
            skLineSegment(sketch, "E731", {"start": v(-26.52, 52.7) * mm, "end": v(-26.8, 52.38) * mm});
            skLineSegment(sketch, "E732", {"start": v(-26.8, 52.38) * mm, "end": v(-27, 52) * mm});
            skLineSegment(sketch, "E733", {"start": v(-27, 52) * mm, "end": v(-27.1, 51.6) * mm});
            skLineSegment(sketch, "E734", {"start": v(-27.1, 51.6) * mm, "end": v(-27.07, 51.17) * mm});
            skLineSegment(sketch, "E735", {"start": v(-27.07, 51.17) * mm, "end": v(-26.94, 50.77) * mm});
            skLineSegment(sketch, "E736", {"start": v(-26.94, 50.77) * mm, "end": v(-26.77, 50.41) * mm});
            skLineSegment(sketch, "E737", {"start": v(-26.77, 50.41) * mm, "end": v(-26.6, 50.06) * mm});
            skLineSegment(sketch, "E738", {"start": v(-26.6, 50.06) * mm, "end": v(-26.42, 49.7) * mm});
            skLineSegment(sketch, "E739", {"start": v(-26.42, 49.7) * mm, "end": v(-26.25, 49.35) * mm});
            skLineSegment(sketch, "E740", {"start": v(-26.25, 49.35) * mm, "end": v(-26.07, 49) * mm});
            skLineSegment(sketch, "E741", {"start": v(-26.07, 49) * mm, "end": v(-25.9, 48.64) * mm});
            skLineSegment(sketch, "E742", {"start": v(-25.9, 48.64) * mm, "end": v(-25.72, 48.28) * mm});
            skLineSegment(sketch, "E743", {"start": v(-25.72, 48.28) * mm, "end": v(-25.55, 47.93) * mm});
            skLineSegment(sketch, "E744", {"start": v(-25.55, 47.93) * mm, "end": v(-25.37, 47.57) * mm});
            skLineSegment(sketch, "E745", {"start": v(-25.37, 47.57) * mm, "end": v(-25.2, 47.22) * mm});
            skLineSegment(sketch, "E746", {"start": v(-25.2, 47.22) * mm, "end": v(-25.02, 46.87) * mm});
            skLineSegment(sketch, "E747", {"start": v(-25.02, 46.87) * mm, "end": v(-24.85, 46.5) * mm});
            skLineSegment(sketch, "E748", {"start": v(-24.85, 46.5) * mm, "end": v(-24.7, 46.2) * mm});
            skLineSegment(sketch, "E749", {"start": v(-24.7, 46.2) * mm, "end": v(-25.04, 46.01) * mm});
            skLineSegment(sketch, "E750", {"start": v(-25.04, 46.01) * mm, "end": v(-25.4, 45.83) * mm});
            skLineSegment(sketch, "E751", {"start": v(-25.4, 45.83) * mm, "end": v(-25.74, 45.64) * mm});
            skLineSegment(sketch, "E752", {"start": v(-25.74, 45.64) * mm, "end": v(-26.08, 45.45) * mm});
            skLineSegment(sketch, "E753", {"start": v(-26.08, 45.45) * mm, "end": v(-26.43, 45.26) * mm});
            skLineSegment(sketch, "E754", {"start": v(-26.43, 45.26) * mm, "end": v(-26.77, 45.07) * mm});
            skLineSegment(sketch, "E755", {"start": v(-26.77, 45.07) * mm, "end": v(-27.12, 44.88) * mm});
            skLineSegment(sketch, "E756", {"start": v(-27.12, 44.88) * mm, "end": v(-27.46, 44.7) * mm});
            skLineSegment(sketch, "E757", {"start": v(-27.46, 44.7) * mm, "end": v(-27.81, 44.5) * mm});
            skLineSegment(sketch, "E758", {"start": v(-27.81, 44.5) * mm, "end": v(-28.16, 44.32) * mm});
            skLineSegment(sketch, "E759", {"start": v(-28.16, 44.32) * mm, "end": v(-28.5, 44.13) * mm});
            skLineSegment(sketch, "E760", {"start": v(-28.5, 44.13) * mm, "end": v(-28.58, 44.08) * mm});
            skLineSegment(sketch, "E761", {"start": v(-28.58, 44.08) * mm, "end": v(-28.79, 44.42) * mm});
            skLineSegment(sketch, "E762", {"start": v(-28.79, 44.42) * mm, "end": v(-28.99, 44.76) * mm});
            skLineSegment(sketch, "E763", {"start": v(-28.99, 44.76) * mm, "end": v(-29.2, 45.1) * mm});
            skLineSegment(sketch, "E764", {"start": v(-29.2, 45.1) * mm, "end": v(-29.4, 45.44) * mm});
            skLineSegment(sketch, "E765", {"start": v(-29.4, 45.44) * mm, "end": v(-29.6, 45.77) * mm});
            skLineSegment(sketch, "E766", {"start": v(-29.6, 45.77) * mm, "end": v(-29.8, 46.11) * mm});
            skLineSegment(sketch, "E767", {"start": v(-29.8, 46.11) * mm, "end": v(-30.01, 46.45) * mm});
            skLineSegment(sketch, "E768", {"start": v(-30.01, 46.45) * mm, "end": v(-30.21, 46.79) * mm});
            skLineSegment(sketch, "E769", {"start": v(-30.21, 46.79) * mm, "end": v(-30.42, 47.13) * mm});
            skLineSegment(sketch, "E770", {"start": v(-30.42, 47.13) * mm, "end": v(-30.62, 47.47) * mm});
            skLineSegment(sketch, "E771", {"start": v(-30.62, 47.47) * mm, "end": v(-30.83, 47.8) * mm});
            skLineSegment(sketch, "E772", {"start": v(-30.83, 47.8) * mm, "end": v(-31.03, 48.15) * mm});
            skLineSegment(sketch, "E773", {"start": v(-31.03, 48.15) * mm, "end": v(-31.26, 48.5) * mm});
            skLineSegment(sketch, "E774", {"start": v(-31.26, 48.5) * mm, "end": v(-31.54, 48.82) * mm});
            skLineSegment(sketch, "E775", {"start": v(-31.54, 48.82) * mm, "end": v(-31.9, 49.05) * mm});
            skLineSegment(sketch, "E776", {"start": v(-31.9, 49.05) * mm, "end": v(-32.3, 49.17) * mm});
            skLineSegment(sketch, "E777", {"start": v(-32.3, 49.17) * mm, "end": v(-32.56, 49.2) * mm});
            skLineSegment(sketch, "E778", {"start": v(-32.56, 49.2) * mm, "end": v(-32.98, 49.14) * mm});
            skLineSegment(sketch, "E779", {"start": v(-32.98, 49.14) * mm, "end": v(-33.37, 48.98) * mm});
            skLineSegment(sketch, "E780", {"start": v(-33.37, 48.98) * mm, "end": v(-33.44, 48.94) * mm});
            skLineSegment(sketch, "E781", {"start": v(-33.44, 48.94) * mm, "end": v(-33.77, 48.67) * mm});
            skLineSegment(sketch, "E782", {"start": v(-33.77, 48.67) * mm, "end": v(-34, 48.32) * mm});
            skLineSegment(sketch, "E783", {"start": v(-34, 48.32) * mm, "end": v(-34.15, 47.92) * mm});
            skLineSegment(sketch, "E784", {"start": v(-34.15, 47.92) * mm, "end": v(-34.18, 47.5) * mm});
            skLineSegment(sketch, "E785", {"start": v(-34.18, 47.5) * mm, "end": v(-34.1, 47.08) * mm});
            skLineSegment(sketch, "E786", {"start": v(-34.1, 47.08) * mm, "end": v(-33.91, 46.7) * mm});
            skLineSegment(sketch, "E787", {"start": v(-33.91, 46.7) * mm, "end": v(-33.7, 46.37) * mm});
            skLineSegment(sketch, "E788", {"start": v(-33.7, 46.37) * mm, "end": v(-33.47, 46.05) * mm});
            skLineSegment(sketch, "E789", {"start": v(-33.47, 46.05) * mm, "end": v(-33.24, 45.72) * mm});
            skLineSegment(sketch, "E790", {"start": v(-33.24, 45.72) * mm, "end": v(-33.02, 45.4) * mm});
            skLineSegment(sketch, "E791", {"start": v(-33.02, 45.4) * mm, "end": v(-32.8, 45.07) * mm});
            skLineSegment(sketch, "E792", {"start": v(-32.8, 45.07) * mm, "end": v(-32.57, 44.74) * mm});
            skLineSegment(sketch, "E793", {"start": v(-32.57, 44.74) * mm, "end": v(-32.35, 44.41) * mm});
            skLineSegment(sketch, "E794", {"start": v(-32.35, 44.41) * mm, "end": v(-32.13, 44.09) * mm});
            skLineSegment(sketch, "E795", {"start": v(-32.13, 44.09) * mm, "end": v(-31.9, 43.76) * mm});
            skLineSegment(sketch, "E796", {"start": v(-31.9, 43.76) * mm, "end": v(-31.68, 43.44) * mm});
            skLineSegment(sketch, "E797", {"start": v(-31.68, 43.44) * mm, "end": v(-31.46, 43.1) * mm});
            skLineSegment(sketch, "E798", {"start": v(-31.46, 43.1) * mm, "end": v(-31.23, 42.78) * mm});
            skLineSegment(sketch, "E799", {"start": v(-31.23, 42.78) * mm, "end": v(-31.04, 42.5) * mm});
            skLineSegment(sketch, "E800", {"start": v(-31.04, 42.5) * mm, "end": v(-31.36, 42.26) * mm});
            skLineSegment(sketch, "E801", {"start": v(-31.36, 42.26) * mm, "end": v(-31.67, 42.03) * mm});
            skLineSegment(sketch, "E802", {"start": v(-31.67, 42.03) * mm, "end": v(-31.99, 41.8) * mm});
            skLineSegment(sketch, "E803", {"start": v(-31.99, 41.8) * mm, "end": v(-32.3, 41.56) * mm});
            skLineSegment(sketch, "E804", {"start": v(-32.3, 41.56) * mm, "end": v(-32.62, 41.32) * mm});
            skLineSegment(sketch, "E805", {"start": v(-32.62, 41.32) * mm, "end": v(-32.94, 41.08) * mm});
            skLineSegment(sketch, "E806", {"start": v(-32.94, 41.08) * mm, "end": v(-33.25, 40.85) * mm});
            skLineSegment(sketch, "E807", {"start": v(-33.25, 40.85) * mm, "end": v(-33.57, 40.61) * mm});
            skLineSegment(sketch, "E808", {"start": v(-33.57, 40.61) * mm, "end": v(-33.88, 40.38) * mm});
            skLineSegment(sketch, "E809", {"start": v(-33.88, 40.38) * mm, "end": v(-34.2, 40.14) * mm});
            skLineSegment(sketch, "E810", {"start": v(-34.2, 40.14) * mm, "end": v(-34.51, 39.9) * mm});
            skLineSegment(sketch, "E811", {"start": v(-34.51, 39.9) * mm, "end": v(-34.59, 39.85) * mm});
            skLineSegment(sketch, "E812", {"start": v(-34.59, 39.85) * mm, "end": v(-34.83, 40.15) * mm});
            skLineSegment(sketch, "E813", {"start": v(-34.83, 40.15) * mm, "end": v(-35.08, 40.46) * mm});
            skLineSegment(sketch, "E814", {"start": v(-35.08, 40.46) * mm, "end": v(-35.34, 40.77) * mm});
            skLineSegment(sketch, "E815", {"start": v(-35.34, 40.77) * mm, "end": v(-35.59, 41.07) * mm});
            skLineSegment(sketch, "E816", {"start": v(-35.59, 41.07) * mm, "end": v(-35.83, 41.38) * mm});
            skLineSegment(sketch, "E817", {"start": v(-35.83, 41.38) * mm, "end": v(-36.09, 41.69) * mm});
            skLineSegment(sketch, "E818", {"start": v(-36.09, 41.69) * mm, "end": v(-36.34, 42) * mm});
            skLineSegment(sketch, "E819", {"start": v(-36.34, 42) * mm, "end": v(-36.59, 42.3) * mm});
            skLineSegment(sketch, "E820", {"start": v(-36.59, 42.3) * mm, "end": v(-36.84, 42.6) * mm});
            skLineSegment(sketch, "E821", {"start": v(-36.84, 42.6) * mm, "end": v(-37.09, 42.9) * mm});
            skLineSegment(sketch, "E822", {"start": v(-37.09, 42.9) * mm, "end": v(-37.34, 43.21) * mm});
            skLineSegment(sketch, "E823", {"start": v(-37.34, 43.21) * mm, "end": v(-37.6, 43.52) * mm});
            skLineSegment(sketch, "E824", {"start": v(-37.6, 43.52) * mm, "end": v(-37.86, 43.85) * mm});
            skLineSegment(sketch, "E825", {"start": v(-37.86, 43.85) * mm, "end": v(-38.19, 44.12) * mm});
            skLineSegment(sketch, "E826", {"start": v(-38.19, 44.12) * mm, "end": v(-38.58, 44.3) * mm});
            skLineSegment(sketch, "E827", {"start": v(-38.58, 44.3) * mm, "end": v(-39, 44.36) * mm});
            skLineSegment(sketch, "E828", {"start": v(-39, 44.36) * mm, "end": v(-39.41, 44.31) * mm});
            skLineSegment(sketch, "E829", {"start": v(-39.41, 44.31) * mm, "end": v(-39.8, 44.16) * mm});
            skLineSegment(sketch, "E830", {"start": v(-39.8, 44.16) * mm, "end": v(-40.09, 43.97) * mm});
            skLineSegment(sketch, "E831", {"start": v(-40.09, 43.97) * mm, "end": v(-40.37, 43.65) * mm});
            skLineSegment(sketch, "E832", {"start": v(-40.37, 43.65) * mm, "end": v(-40.56, 43.27) * mm});
            skLineSegment(sketch, "E833", {"start": v(-40.56, 43.27) * mm, "end": v(-40.64, 42.85) * mm});
            skLineSegment(sketch, "E834", {"start": v(-40.64, 42.85) * mm, "end": v(-40.61, 42.43) * mm});
            skLineSegment(sketch, "E835", {"start": v(-40.61, 42.43) * mm, "end": v(-40.47, 42.03) * mm});
            skLineSegment(sketch, "E836", {"start": v(-40.47, 42.03) * mm, "end": v(-40.23, 41.68) * mm});
            skLineSegment(sketch, "E837", {"start": v(-40.23, 41.68) * mm, "end": v(-39.97, 41.4) * mm});
            skLineSegment(sketch, "E838", {"start": v(-39.97, 41.4) * mm, "end": v(-39.7, 41.1) * mm});
            skLineSegment(sketch, "E839", {"start": v(-39.7, 41.1) * mm, "end": v(-39.43, 40.8) * mm});
            skLineSegment(sketch, "E840", {"start": v(-39.43, 40.8) * mm, "end": v(-39.17, 40.52) * mm});
            skLineSegment(sketch, "E841", {"start": v(-39.17, 40.52) * mm, "end": v(-38.9, 40.23) * mm});
            skLineSegment(sketch, "E842", {"start": v(-38.9, 40.23) * mm, "end": v(-38.63, 39.93) * mm});
            skLineSegment(sketch, "E843", {"start": v(-38.63, 39.93) * mm, "end": v(-38.36, 39.64) * mm});
            skLineSegment(sketch, "E844", {"start": v(-38.36, 39.64) * mm, "end": v(-38.1, 39.35) * mm});
            skLineSegment(sketch, "E845", {"start": v(-38.1, 39.35) * mm, "end": v(-37.83, 39.06) * mm});
            skLineSegment(sketch, "E846", {"start": v(-37.83, 39.06) * mm, "end": v(-37.56, 38.77) * mm});
            skLineSegment(sketch, "E847", {"start": v(-37.56, 38.77) * mm, "end": v(-37.3, 38.48) * mm});
            skLineSegment(sketch, "E848", {"start": v(-37.3, 38.48) * mm, "end": v(-37.03, 38.18) * mm});
            skLineSegment(sketch, "E849", {"start": v(-37.03, 38.18) * mm, "end": v(-36.8, 37.93) * mm});
            skLineSegment(sketch, "E850", {"start": v(-36.8, 37.93) * mm, "end": v(-37.08, 37.65) * mm});
            skLineSegment(sketch, "E851", {"start": v(-37.08, 37.65) * mm, "end": v(-37.35, 37.38) * mm});
            skLineSegment(sketch, "E852", {"start": v(-37.35, 37.38) * mm, "end": v(-37.63, 37.1) * mm});
            skLineSegment(sketch, "E853", {"start": v(-37.63, 37.1) * mm, "end": v(-37.91, 36.82) * mm});
            skLineSegment(sketch, "E854", {"start": v(-37.91, 36.82) * mm, "end": v(-38.19, 36.54) * mm});
            skLineSegment(sketch, "E855", {"start": v(-38.19, 36.54) * mm, "end": v(-38.47, 36.26) * mm});
            skLineSegment(sketch, "E856", {"start": v(-38.47, 36.26) * mm, "end": v(-38.75, 35.98) * mm});
            skLineSegment(sketch, "E857", {"start": v(-38.75, 35.98) * mm, "end": v(-39.02, 35.7) * mm});
            skLineSegment(sketch, "E858", {"start": v(-39.02, 35.7) * mm, "end": v(-39.3, 35.43) * mm});
            skLineSegment(sketch, "E859", {"start": v(-39.3, 35.43) * mm, "end": v(-39.58, 35.15) * mm});
            skLineSegment(sketch, "E860", {"start": v(-39.58, 35.15) * mm, "end": v(-39.86, 34.87) * mm});
            skLineSegment(sketch, "E861", {"start": v(-39.86, 34.87) * mm, "end": v(-39.92, 34.8) * mm});
            skLineSegment(sketch, "E862", {"start": v(-39.92, 34.8) * mm, "end": v(-40.21, 35.07) * mm});
            skLineSegment(sketch, "E863", {"start": v(-40.21, 35.07) * mm, "end": v(-40.5, 35.34) * mm});
            skLineSegment(sketch, "E864", {"start": v(-40.5, 35.34) * mm, "end": v(-40.8, 35.6) * mm});
            skLineSegment(sketch, "E865", {"start": v(-40.8, 35.6) * mm, "end": v(-41.09, 35.87) * mm});
            skLineSegment(sketch, "E866", {"start": v(-41.09, 35.87) * mm, "end": v(-41.38, 36.14) * mm});
            skLineSegment(sketch, "E867", {"start": v(-41.38, 36.14) * mm, "end": v(-41.67, 36.4) * mm});
            skLineSegment(sketch, "E868", {"start": v(-41.67, 36.4) * mm, "end": v(-41.96, 36.68) * mm});
            skLineSegment(sketch, "E869", {"start": v(-41.96, 36.68) * mm, "end": v(-42.25, 36.94) * mm});
            skLineSegment(sketch, "E870", {"start": v(-42.25, 36.94) * mm, "end": v(-42.55, 37.21) * mm});
            skLineSegment(sketch, "E871", {"start": v(-42.55, 37.21) * mm, "end": v(-42.84, 37.48) * mm});
            skLineSegment(sketch, "E872", {"start": v(-42.84, 37.48) * mm, "end": v(-43.13, 37.74) * mm});
            skLineSegment(sketch, "E873", {"start": v(-43.13, 37.74) * mm, "end": v(-43.42, 38.01) * mm});
            skLineSegment(sketch, "E874", {"start": v(-43.42, 38.01) * mm, "end": v(-43.74, 38.3) * mm});
            skLineSegment(sketch, "E875", {"start": v(-43.74, 38.3) * mm, "end": v(-44.1, 38.52) * mm});
            skLineSegment(sketch, "E876", {"start": v(-44.1, 38.52) * mm, "end": v(-44.5, 38.63) * mm});
            skLineSegment(sketch, "E877", {"start": v(-44.5, 38.63) * mm, "end": v(-44.76, 38.65) * mm});
            skLineSegment(sketch, "E878", {"start": v(-44.76, 38.65) * mm, "end": v(-45.18, 38.6) * mm});
            skLineSegment(sketch, "E879", {"start": v(-45.18, 38.6) * mm, "end": v(-45.57, 38.42) * mm});
            skLineSegment(sketch, "E880", {"start": v(-45.57, 38.42) * mm, "end": v(-45.9, 38.16) * mm});
            skLineSegment(sketch, "E881", {"start": v(-45.9, 38.16) * mm, "end": v(-45.96, 38.1) * mm});
            skLineSegment(sketch, "E882", {"start": v(-45.96, 38.1) * mm, "end": v(-46.19, 37.74) * mm});
            skLineSegment(sketch, "E883", {"start": v(-46.19, 37.74) * mm, "end": v(-46.32, 37.34) * mm});
            skLineSegment(sketch, "E884", {"start": v(-46.32, 37.34) * mm, "end": v(-46.34, 36.92) * mm});
            skLineSegment(sketch, "E885", {"start": v(-46.34, 36.92) * mm, "end": v(-46.26, 36.5) * mm});
            skLineSegment(sketch, "E886", {"start": v(-46.26, 36.5) * mm, "end": v(-46.06, 36.13) * mm});
            skLineSegment(sketch, "E887", {"start": v(-46.06, 36.13) * mm, "end": v(-45.78, 35.81) * mm});
            skLineSegment(sketch, "E888", {"start": v(-45.78, 35.81) * mm, "end": v(-45.47, 35.56) * mm});
            skLineSegment(sketch, "E889", {"start": v(-45.47, 35.56) * mm, "end": v(-45.17, 35.31) * mm});
            skLineSegment(sketch, "E890", {"start": v(-45.17, 35.31) * mm, "end": v(-44.86, 35.06) * mm});
            skLineSegment(sketch, "E891", {"start": v(-44.86, 35.06) * mm, "end": v(-44.55, 34.81) * mm});
            skLineSegment(sketch, "E892", {"start": v(-44.55, 34.81) * mm, "end": v(-44.25, 34.56) * mm});
            skLineSegment(sketch, "E893", {"start": v(-44.25, 34.56) * mm, "end": v(-43.94, 34.31) * mm});
            skLineSegment(sketch, "E894", {"start": v(-43.94, 34.31) * mm, "end": v(-43.64, 34.06) * mm});
            skLineSegment(sketch, "E895", {"start": v(-43.64, 34.06) * mm, "end": v(-43.33, 33.81) * mm});
            skLineSegment(sketch, "E896", {"start": v(-43.33, 33.81) * mm, "end": v(-43.02, 33.56) * mm});
            skLineSegment(sketch, "E897", {"start": v(-43.02, 33.56) * mm, "end": v(-42.72, 33.31) * mm});
            skLineSegment(sketch, "E898", {"start": v(-42.72, 33.31) * mm, "end": v(-42.41, 33.06) * mm});
            skLineSegment(sketch, "E899", {"start": v(-42.41, 33.06) * mm, "end": v(-42.1, 32.8) * mm});
            skLineSegment(sketch, "E900", {"start": v(-42.1, 32.8) * mm, "end": v(-41.84, 32.6) * mm});
            skLineSegment(sketch, "E901", {"start": v(-41.84, 32.6) * mm, "end": v(-42.08, 32.28) * mm});
            skLineSegment(sketch, "E902", {"start": v(-42.08, 32.28) * mm, "end": v(-42.31, 31.96) * mm});
            skLineSegment(sketch, "E903", {"start": v(-42.31, 31.96) * mm, "end": v(-42.55, 31.65) * mm});
            skLineSegment(sketch, "E904", {"start": v(-42.55, 31.65) * mm, "end": v(-42.78, 31.33) * mm});
            skLineSegment(sketch, "E905", {"start": v(-42.78, 31.33) * mm, "end": v(-43.02, 31.02) * mm});
            skLineSegment(sketch, "E906", {"start": v(-43.02, 31.02) * mm, "end": v(-43.26, 30.7) * mm});
            skLineSegment(sketch, "E907", {"start": v(-43.26, 30.7) * mm, "end": v(-43.5, 30.39) * mm});
            skLineSegment(sketch, "E908", {"start": v(-43.5, 30.39) * mm, "end": v(-43.73, 30.07) * mm});
            skLineSegment(sketch, "E909", {"start": v(-43.73, 30.07) * mm, "end": v(-43.96, 29.76) * mm});
            skLineSegment(sketch, "E910", {"start": v(-43.96, 29.76) * mm, "end": v(-44.2, 29.44) * mm});
            skLineSegment(sketch, "E911", {"start": v(-44.2, 29.44) * mm, "end": v(-44.44, 29.13) * mm});
            skLineSegment(sketch, "E912", {"start": v(-44.44, 29.13) * mm, "end": v(-44.5, 29.05) * mm});
            skLineSegment(sketch, "E913", {"start": v(-44.5, 29.05) * mm, "end": v(-44.82, 29.27) * mm});
            skLineSegment(sketch, "E914", {"start": v(-44.82, 29.27) * mm, "end": v(-45.14, 29.5) * mm});
            skLineSegment(sketch, "E915", {"start": v(-45.14, 29.5) * mm, "end": v(-45.47, 29.72) * mm});
            skLineSegment(sketch, "E916", {"start": v(-45.47, 29.72) * mm, "end": v(-45.8, 29.94) * mm});
            skLineSegment(sketch, "E917", {"start": v(-45.8, 29.94) * mm, "end": v(-46.12, 30.17) * mm});
            skLineSegment(sketch, "E918", {"start": v(-46.12, 30.17) * mm, "end": v(-46.45, 30.4) * mm});
            skLineSegment(sketch, "E919", {"start": v(-46.45, 30.4) * mm, "end": v(-46.78, 30.61) * mm});
            skLineSegment(sketch, "E920", {"start": v(-46.78, 30.61) * mm, "end": v(-47.1, 30.84) * mm});
            skLineSegment(sketch, "E921", {"start": v(-47.1, 30.84) * mm, "end": v(-47.43, 31.06) * mm});
            skLineSegment(sketch, "E922", {"start": v(-47.43, 31.06) * mm, "end": v(-47.76, 31.28) * mm});
            skLineSegment(sketch, "E923", {"start": v(-47.76, 31.28) * mm, "end": v(-48.08, 31.5) * mm});
            skLineSegment(sketch, "E924", {"start": v(-48.08, 31.5) * mm, "end": v(-48.41, 31.73) * mm});
            skLineSegment(sketch, "E925", {"start": v(-48.41, 31.73) * mm, "end": v(-48.76, 31.97) * mm});
            skLineSegment(sketch, "E926", {"start": v(-48.76, 31.97) * mm, "end": v(-49.15, 32.13) * mm});
            skLineSegment(sketch, "E927", {"start": v(-49.15, 32.13) * mm, "end": v(-49.57, 32.19) * mm});
            skLineSegment(sketch, "E928", {"start": v(-49.57, 32.19) * mm, "end": v(-50, 32.14) * mm});
            skLineSegment(sketch, "E929", {"start": v(-50, 32.14) * mm, "end": v(-50.38, 31.97) * mm});
            skLineSegment(sketch, "E930", {"start": v(-50.38, 31.97) * mm, "end": v(-50.72, 31.72) * mm});
            skLineSegment(sketch, "E931", {"start": v(-50.72, 31.72) * mm, "end": v(-50.93, 31.45) * mm});
            skLineSegment(sketch, "E932", {"start": v(-50.93, 31.45) * mm, "end": v(-51.11, 31.07) * mm});
            skLineSegment(sketch, "E933", {"start": v(-51.11, 31.07) * mm, "end": v(-51.18, 30.65) * mm});
            skLineSegment(sketch, "E934", {"start": v(-51.18, 30.65) * mm, "end": v(-51.15, 30.23) * mm});
            skLineSegment(sketch, "E935", {"start": v(-51.15, 30.23) * mm, "end": v(-51, 29.83) * mm});
            skLineSegment(sketch, "E936", {"start": v(-51, 29.83) * mm, "end": v(-50.76, 29.49) * mm});
            skLineSegment(sketch, "E937", {"start": v(-50.76, 29.49) * mm, "end": v(-50.43, 29.22) * mm});
            skLineSegment(sketch, "E938", {"start": v(-50.43, 29.22) * mm, "end": v(-50.1, 29.01) * mm});
            skLineSegment(sketch, "E939", {"start": v(-50.1, 29.01) * mm, "end": v(-49.75, 28.81) * mm});
            skLineSegment(sketch, "E940", {"start": v(-49.75, 28.81) * mm, "end": v(-49.41, 28.6) * mm});
            skLineSegment(sketch, "E941", {"start": v(-49.41, 28.6) * mm, "end": v(-49.08, 28.4) * mm});
            skLineSegment(sketch, "E942", {"start": v(-49.08, 28.4) * mm, "end": v(-48.74, 28.2) * mm});
            skLineSegment(sketch, "E943", {"start": v(-48.74, 28.2) * mm, "end": v(-48.4, 28) * mm});
            skLineSegment(sketch, "E944", {"start": v(-48.4, 28) * mm, "end": v(-48.06, 27.79) * mm});
            skLineSegment(sketch, "E945", {"start": v(-48.06, 27.79) * mm, "end": v(-47.72, 27.58) * mm});
            skLineSegment(sketch, "E946", {"start": v(-47.72, 27.58) * mm, "end": v(-47.38, 27.38) * mm});
            skLineSegment(sketch, "E947", {"start": v(-47.38, 27.38) * mm, "end": v(-47.04, 27.18) * mm});
            skLineSegment(sketch, "E948", {"start": v(-47.04, 27.18) * mm, "end": v(-46.7, 26.97) * mm});
            skLineSegment(sketch, "E949", {"start": v(-46.7, 26.97) * mm, "end": v(-46.36, 26.77) * mm});
            skLineSegment(sketch, "E950", {"start": v(-46.36, 26.77) * mm, "end": v(-46.07, 26.6) * mm});
            skLineSegment(sketch, "E951", {"start": v(-46.07, 26.6) * mm, "end": v(-46.26, 26.24) * mm});
            skLineSegment(sketch, "E952", {"start": v(-46.26, 26.24) * mm, "end": v(-46.45, 25.9) * mm});
            skLineSegment(sketch, "E953", {"start": v(-46.45, 25.9) * mm, "end": v(-46.64, 25.55) * mm});
            skLineSegment(sketch, "E954", {"start": v(-46.64, 25.55) * mm, "end": v(-46.83, 25.2) * mm});
            skLineSegment(sketch, "E955", {"start": v(-46.83, 25.2) * mm, "end": v(-47.02, 24.86) * mm});
            skLineSegment(sketch, "E956", {"start": v(-47.02, 24.86) * mm, "end": v(-47.2, 24.52) * mm});
            skLineSegment(sketch, "E957", {"start": v(-47.2, 24.52) * mm, "end": v(-47.4, 24.17) * mm});
            skLineSegment(sketch, "E958", {"start": v(-47.4, 24.17) * mm, "end": v(-47.58, 23.83) * mm});
            skLineSegment(sketch, "E959", {"start": v(-47.58, 23.83) * mm, "end": v(-47.77, 23.48) * mm});
            skLineSegment(sketch, "E960", {"start": v(-47.77, 23.48) * mm, "end": v(-47.96, 23.13) * mm});
            skLineSegment(sketch, "E961", {"start": v(-47.96, 23.13) * mm, "end": v(-48.15, 22.79) * mm});
            skLineSegment(sketch, "E962", {"start": v(-48.15, 22.79) * mm, "end": v(-48.2, 22.7) * mm});
            skLineSegment(sketch, "E963", {"start": v(-48.2, 22.7) * mm, "end": v(-48.55, 22.88) * mm});
            skLineSegment(sketch, "E964", {"start": v(-48.55, 22.88) * mm, "end": v(-48.9, 23.06) * mm});
            skLineSegment(sketch, "E965", {"start": v(-48.9, 23.06) * mm, "end": v(-49.26, 23.23) * mm});
            skLineSegment(sketch, "E966", {"start": v(-49.26, 23.23) * mm, "end": v(-49.61, 23.4) * mm});
            skLineSegment(sketch, "E967", {"start": v(-49.61, 23.4) * mm, "end": v(-49.97, 23.58) * mm});
            skLineSegment(sketch, "E968", {"start": v(-49.97, 23.58) * mm, "end": v(-50.32, 23.75) * mm});
            skLineSegment(sketch, "E969", {"start": v(-50.32, 23.75) * mm, "end": v(-50.68, 23.93) * mm});
            skLineSegment(sketch, "E970", {"start": v(-50.68, 23.93) * mm, "end": v(-51.03, 24.1) * mm});
            skLineSegment(sketch, "E971", {"start": v(-51.03, 24.1) * mm, "end": v(-51.39, 24.28) * mm});
            skLineSegment(sketch, "E972", {"start": v(-51.39, 24.28) * mm, "end": v(-51.74, 24.45) * mm});
            skLineSegment(sketch, "E973", {"start": v(-51.74, 24.45) * mm, "end": v(-52.1, 24.63) * mm});
            skLineSegment(sketch, "E974", {"start": v(-52.1, 24.63) * mm, "end": v(-52.45, 24.8) * mm});
            skLineSegment(sketch, "E975", {"start": v(-52.45, 24.8) * mm, "end": v(-52.84, 24.99) * mm});
            skLineSegment(sketch, "E976", {"start": v(-52.84, 24.99) * mm, "end": v(-53.25, 25.1) * mm});
            skLineSegment(sketch, "E977", {"start": v(-53.25, 25.1) * mm, "end": v(-53.41, 25.1) * mm});
            skLineSegment(sketch, "E978", {"start": v(-53.41, 25.1) * mm, "end": v(-53.84, 25.06) * mm});
            skLineSegment(sketch, "E979", {"start": v(-53.84, 25.06) * mm, "end": v(-54.23, 24.9) * mm});
            skLineSegment(sketch, "E980", {"start": v(-54.23, 24.9) * mm, "end": v(-54.57, 24.65) * mm});
            skLineSegment(sketch, "E981", {"start": v(-54.57, 24.65) * mm, "end": v(-54.83, 24.32) * mm});
            skLineSegment(sketch, "E982", {"start": v(-54.83, 24.32) * mm, "end": v(-54.9, 24.17) * mm});
            skLineSegment(sketch, "E983", {"start": v(-54.9, 24.17) * mm, "end": v(-55.03, 23.76) * mm});
            skLineSegment(sketch, "E984", {"start": v(-55.03, 23.76) * mm, "end": v(-55.05, 23.34) * mm});
            skLineSegment(sketch, "E985", {"start": v(-55.05, 23.34) * mm, "end": v(-54.95, 22.93) * mm});
            skLineSegment(sketch, "E986", {"start": v(-54.95, 22.93) * mm, "end": v(-54.75, 22.55) * mm});
            skLineSegment(sketch, "E987", {"start": v(-54.75, 22.55) * mm, "end": v(-54.46, 22.25) * mm});
            skLineSegment(sketch, "E988", {"start": v(-54.46, 22.25) * mm, "end": v(-54.1, 22.03) * mm});
            skLineSegment(sketch, "E989", {"start": v(-54.1, 22.03) * mm, "end": v(-53.73, 21.87) * mm});
            skLineSegment(sketch, "E990", {"start": v(-53.73, 21.87) * mm, "end": v(-53.37, 21.72) * mm});
            skLineSegment(sketch, "E991", {"start": v(-53.37, 21.72) * mm, "end": v(-53, 21.56) * mm});
            skLineSegment(sketch, "E992", {"start": v(-53, 21.56) * mm, "end": v(-52.64, 21.41) * mm});
            skLineSegment(sketch, "E993", {"start": v(-52.64, 21.41) * mm, "end": v(-52.28, 21.26) * mm});
            skLineSegment(sketch, "E994", {"start": v(-52.28, 21.26) * mm, "end": v(-51.9, 21.1) * mm});
            skLineSegment(sketch, "E995", {"start": v(-51.9, 21.1) * mm, "end": v(-51.55, 20.95) * mm});
            skLineSegment(sketch, "E996", {"start": v(-51.55, 20.95) * mm, "end": v(-51.18, 20.8) * mm});
            skLineSegment(sketch, "E997", {"start": v(-51.18, 20.8) * mm, "end": v(-50.81, 20.64) * mm});
            skLineSegment(sketch, "E998", {"start": v(-50.81, 20.64) * mm, "end": v(-50.45, 20.49) * mm});
            skLineSegment(sketch, "E999", {"start": v(-50.45, 20.49) * mm, "end": v(-50.09, 20.33) * mm});
            skLineSegment(sketch, "E1000", {"start": v(-50.09, 20.33) * mm, "end": v(-49.72, 20.18) * mm});
            skLineSegment(sketch, "E1001", {"start": v(-49.72, 20.18) * mm, "end": v(-49.4, 20.05) * mm});
            skLineSegment(sketch, "E1002", {"start": v(-49.4, 20.05) * mm, "end": v(-49.55, 19.68) * mm});
            skLineSegment(sketch, "E1003", {"start": v(-49.55, 19.68) * mm, "end": v(-49.68, 19.3) * mm});
            skLineSegment(sketch, "E1004", {"start": v(-49.68, 19.3) * mm, "end": v(-49.82, 18.94) * mm});
            skLineSegment(sketch, "E1005", {"start": v(-49.82, 18.94) * mm, "end": v(-49.96, 18.57) * mm});
            skLineSegment(sketch, "E1006", {"start": v(-49.96, 18.57) * mm, "end": v(-50.1, 18.2) * mm});
            skLineSegment(sketch, "E1007", {"start": v(-50.1, 18.2) * mm, "end": v(-50.24, 17.83) * mm});
            skLineSegment(sketch, "E1008", {"start": v(-50.24, 17.83) * mm, "end": v(-50.37, 17.46) * mm});
            skLineSegment(sketch, "E1009", {"start": v(-50.37, 17.46) * mm, "end": v(-50.51, 17.1) * mm});
            skLineSegment(sketch, "E1010", {"start": v(-50.51, 17.1) * mm, "end": v(-50.65, 16.73) * mm});
            skLineSegment(sketch, "E1011", {"start": v(-50.65, 16.73) * mm, "end": v(-50.79, 16.36) * mm});
            skLineSegment(sketch, "E1012", {"start": v(-50.79, 16.36) * mm, "end": v(-50.92, 15.99) * mm});
            skLineSegment(sketch, "E1013", {"start": v(-50.92, 15.99) * mm, "end": v(-50.96, 15.9) * mm});
            skLineSegment(sketch, "E1014", {"start": v(-50.96, 15.9) * mm, "end": v(-51.33, 16.02) * mm});
            skLineSegment(sketch, "E1015", {"start": v(-51.33, 16.02) * mm, "end": v(-51.7, 16.14) * mm});
            skLineSegment(sketch, "E1016", {"start": v(-51.7, 16.14) * mm, "end": v(-52.08, 16.27) * mm});
            skLineSegment(sketch, "E1017", {"start": v(-52.08, 16.27) * mm, "end": v(-52.46, 16.39) * mm});
            skLineSegment(sketch, "E1018", {"start": v(-52.46, 16.39) * mm, "end": v(-52.83, 16.51) * mm});
            skLineSegment(sketch, "E1019", {"start": v(-52.83, 16.51) * mm, "end": v(-53.21, 16.63) * mm});
            skLineSegment(sketch, "E1020", {"start": v(-53.21, 16.63) * mm, "end": v(-53.59, 16.76) * mm});
            skLineSegment(sketch, "E1021", {"start": v(-53.59, 16.76) * mm, "end": v(-53.96, 16.88) * mm});
            skLineSegment(sketch, "E1022", {"start": v(-53.96, 16.88) * mm, "end": v(-54.34, 17) * mm});
            skLineSegment(sketch, "E1023", {"start": v(-54.34, 17) * mm, "end": v(-54.72, 17.12) * mm});
            skLineSegment(sketch, "E1024", {"start": v(-54.72, 17.12) * mm, "end": v(-55.1, 17.24) * mm});
            skLineSegment(sketch, "E1025", {"start": v(-55.1, 17.24) * mm, "end": v(-55.47, 17.37) * mm});
            skLineSegment(sketch, "E1026", {"start": v(-55.47, 17.37) * mm, "end": v(-55.87, 17.5) * mm});
            skLineSegment(sketch, "E1027", {"start": v(-55.87, 17.5) * mm, "end": v(-56.3, 17.54) * mm});
            skLineSegment(sketch, "E1028", {"start": v(-56.3, 17.54) * mm, "end": v(-56.71, 17.48) * mm});
            skLineSegment(sketch, "E1029", {"start": v(-56.71, 17.48) * mm, "end": v(-57.1, 17.31) * mm});
            skLineSegment(sketch, "E1030", {"start": v(-57.1, 17.31) * mm, "end": v(-57.43, 17.04) * mm});
            skLineSegment(sketch, "E1031", {"start": v(-57.43, 17.04) * mm, "end": v(-57.68, 16.7) * mm});
            skLineSegment(sketch, "E1032", {"start": v(-57.68, 16.7) * mm, "end": v(-57.8, 16.39) * mm});
            skLineSegment(sketch, "E1033", {"start": v(-57.8, 16.39) * mm, "end": v(-57.87, 15.97) * mm});
            skLineSegment(sketch, "E1034", {"start": v(-57.87, 15.97) * mm, "end": v(-57.83, 15.55) * mm});
            skLineSegment(sketch, "E1035", {"start": v(-57.83, 15.55) * mm, "end": v(-57.67, 15.16) * mm});
            skLineSegment(sketch, "E1036", {"start": v(-57.67, 15.16) * mm, "end": v(-57.42, 14.82) * mm});
            skLineSegment(sketch, "E1037", {"start": v(-57.42, 14.82) * mm, "end": v(-57.09, 14.55) * mm});
            skLineSegment(sketch, "E1038", {"start": v(-57.09, 14.55) * mm, "end": v(-56.7, 14.39) * mm});
            skLineSegment(sketch, "E1039", {"start": v(-56.7, 14.39) * mm, "end": v(-56.32, 14.29) * mm});
            skLineSegment(sketch, "E1040", {"start": v(-56.32, 14.29) * mm, "end": v(-55.94, 14.19) * mm});
            skLineSegment(sketch, "E1041", {"start": v(-55.94, 14.19) * mm, "end": v(-55.55, 14.09) * mm});
            skLineSegment(sketch, "E1042", {"start": v(-55.55, 14.09) * mm, "end": v(-55.17, 13.99) * mm});
            skLineSegment(sketch, "E1043", {"start": v(-55.17, 13.99) * mm, "end": v(-54.79, 13.88) * mm});
            skLineSegment(sketch, "E1044", {"start": v(-54.79, 13.88) * mm, "end": v(-54.4, 13.78) * mm});
            skLineSegment(sketch, "E1045", {"start": v(-54.4, 13.78) * mm, "end": v(-54.02, 13.68) * mm});
            skLineSegment(sketch, "E1046", {"start": v(-54.02, 13.68) * mm, "end": v(-53.64, 13.58) * mm});
            skLineSegment(sketch, "E1047", {"start": v(-53.64, 13.58) * mm, "end": v(-53.26, 13.48) * mm});
            skLineSegment(sketch, "E1048", {"start": v(-53.26, 13.48) * mm, "end": v(-52.87, 13.38) * mm});
            skLineSegment(sketch, "E1049", {"start": v(-52.87, 13.38) * mm, "end": v(-52.5, 13.28) * mm});
            skLineSegment(sketch, "E1050", {"start": v(-52.5, 13.28) * mm, "end": v(-52.1, 13.18) * mm});
            skLineSegment(sketch, "E1051", {"start": v(-52.1, 13.18) * mm, "end": v(-51.78, 13.1) * mm});
            skLineSegment(sketch, "E1052", {"start": v(-51.78, 13.1) * mm, "end": v(-51.86, 12.7) * mm});
            skLineSegment(sketch, "E1053", {"start": v(-51.86, 12.7) * mm, "end": v(-51.95, 12.32) * mm});
            skLineSegment(sketch, "E1054", {"start": v(-51.95, 12.32) * mm, "end": v(-52.03, 11.94) * mm});
            skLineSegment(sketch, "E1055", {"start": v(-52.03, 11.94) * mm, "end": v(-52.11, 11.55) * mm});
            skLineSegment(sketch, "E1056", {"start": v(-52.11, 11.55) * mm, "end": v(-52.2, 11.17) * mm});
            skLineSegment(sketch, "E1057", {"start": v(-52.2, 11.17) * mm, "end": v(-52.28, 10.78) * mm});
            skLineSegment(sketch, "E1058", {"start": v(-52.28, 10.78) * mm, "end": v(-52.37, 10.4) * mm});
            skLineSegment(sketch, "E1059", {"start": v(-52.37, 10.4) * mm, "end": v(-52.45, 10.02) * mm});
            skLineSegment(sketch, "E1060", {"start": v(-52.45, 10.02) * mm, "end": v(-52.53, 9.63) * mm});
            skLineSegment(sketch, "E1061", {"start": v(-52.53, 9.63) * mm, "end": v(-52.62, 9.25) * mm});
            skLineSegment(sketch, "E1062", {"start": v(-52.62, 9.25) * mm, "end": v(-52.7, 8.86) * mm});
            skLineSegment(sketch, "E1063", {"start": v(-52.7, 8.86) * mm, "end": v(-52.72, 8.77) * mm});
            skLineSegment(sketch, "E1064", {"start": v(-52.72, 8.77) * mm, "end": v(-53.1, 8.84) * mm});
            skLineSegment(sketch, "E1065", {"start": v(-53.1, 8.84) * mm, "end": v(-53.5, 8.9) * mm});
            skLineSegment(sketch, "E1066", {"start": v(-53.5, 8.9) * mm, "end": v(-53.89, 8.97) * mm});
            skLineSegment(sketch, "E1067", {"start": v(-53.89, 8.97) * mm, "end": v(-54.28, 9.04) * mm});
            skLineSegment(sketch, "E1068", {"start": v(-54.28, 9.04) * mm, "end": v(-54.67, 9.1) * mm});
            skLineSegment(sketch, "E1069", {"start": v(-54.67, 9.1) * mm, "end": v(-55.06, 9.18) * mm});
            skLineSegment(sketch, "E1070", {"start": v(-55.06, 9.18) * mm, "end": v(-55.45, 9.24) * mm});
            skLineSegment(sketch, "E1071", {"start": v(-55.45, 9.24) * mm, "end": v(-55.84, 9.3) * mm});
            skLineSegment(sketch, "E1072", {"start": v(-55.84, 9.3) * mm, "end": v(-56.23, 9.38) * mm});
            skLineSegment(sketch, "E1073", {"start": v(-56.23, 9.38) * mm, "end": v(-56.62, 9.44) * mm});
            skLineSegment(sketch, "E1074", {"start": v(-56.62, 9.44) * mm, "end": v(-57, 9.51) * mm});
            skLineSegment(sketch, "E1075", {"start": v(-57, 9.51) * mm, "end": v(-57.4, 9.58) * mm});
            skLineSegment(sketch, "E1076", {"start": v(-57.4, 9.58) * mm, "end": v(-57.82, 9.65) * mm});
            skLineSegment(sketch, "E1077", {"start": v(-57.82, 9.65) * mm, "end": v(-57.99, 9.66) * mm});
            skLineSegment(sketch, "E1078", {"start": v(-57.99, 9.66) * mm, "end": v(-58.4, 9.6) * mm});
            skLineSegment(sketch, "E1079", {"start": v(-58.4, 9.6) * mm, "end": v(-58.8, 9.44) * mm});
            skLineSegment(sketch, "E1080", {"start": v(-58.8, 9.44) * mm, "end": v(-59.13, 9.18) * mm});
            skLineSegment(sketch, "E1081", {"start": v(-59.13, 9.18) * mm, "end": v(-59.38, 8.84) * mm});
            skLineSegment(sketch, "E1082", {"start": v(-59.38, 8.84) * mm, "end": v(-59.54, 8.44) * mm});
            skLineSegment(sketch, "E1083", {"start": v(-59.54, 8.44) * mm, "end": v(-59.57, 8.28) * mm});
            skLineSegment(sketch, "E1084", {"start": v(-59.57, 8.28) * mm, "end": v(-59.58, 7.85) * mm});
            skLineSegment(sketch, "E1085", {"start": v(-59.58, 7.85) * mm, "end": v(-59.47, 7.44) * mm});
            skLineSegment(sketch, "E1086", {"start": v(-59.47, 7.44) * mm, "end": v(-59.26, 7.08) * mm});
            skLineSegment(sketch, "E1087", {"start": v(-59.26, 7.08) * mm, "end": v(-58.96, 6.78) * mm});
            skLineSegment(sketch, "E1088", {"start": v(-58.96, 6.78) * mm, "end": v(-58.6, 6.56) * mm});
            skLineSegment(sketch, "E1089", {"start": v(-58.6, 6.56) * mm, "end": v(-58.19, 6.45) * mm});
            skLineSegment(sketch, "E1090", {"start": v(-58.19, 6.45) * mm, "end": v(-57.8, 6.4) * mm});
            skLineSegment(sketch, "E1091", {"start": v(-57.8, 6.4) * mm, "end": v(-57.4, 6.37) * mm});
            skLineSegment(sketch, "E1092", {"start": v(-57.4, 6.37) * mm, "end": v(-57.01, 6.32) * mm});
            skLineSegment(sketch, "E1093", {"start": v(-57.01, 6.32) * mm, "end": v(-56.62, 6.27) * mm});
            skLineSegment(sketch, "E1094", {"start": v(-56.62, 6.27) * mm, "end": v(-56.23, 6.23) * mm});
            skLineSegment(sketch, "E1095", {"start": v(-56.23, 6.23) * mm, "end": v(-55.83, 6.18) * mm});
            skLineSegment(sketch, "E1096", {"start": v(-55.83, 6.18) * mm, "end": v(-55.44, 6.14) * mm});
            skLineSegment(sketch, "E1097", {"start": v(-55.44, 6.14) * mm, "end": v(-55.05, 6.1) * mm});
            skLineSegment(sketch, "E1098", {"start": v(-55.05, 6.1) * mm, "end": v(-54.65, 6.05) * mm});
            skLineSegment(sketch, "E1099", {"start": v(-54.65, 6.05) * mm, "end": v(-54.26, 6) * mm});
            skLineSegment(sketch, "E1100", {"start": v(-54.26, 6) * mm, "end": v(-53.87, 5.96) * mm});
            skLineSegment(sketch, "E1101", {"start": v(-53.87, 5.96) * mm, "end": v(-53.47, 5.91) * mm});
            skLineSegment(sketch, "E1102", {"start": v(-53.47, 5.91) * mm, "end": v(-53.14, 5.87) * mm});
            skLineSegment(sketch, "E1103", {"start": v(-53.14, 5.87) * mm, "end": v(-53.16, 5.48) * mm});
            skLineSegment(sketch, "E1104", {"start": v(-53.16, 5.48) * mm, "end": v(-53.2, 5.09) * mm});
            skLineSegment(sketch, "E1105", {"start": v(-53.2, 5.09) * mm, "end": v(-53.22, 4.7) * mm});
            skLineSegment(sketch, "E1106", {"start": v(-53.22, 4.7) * mm, "end": v(-53.25, 4.3) * mm});
            skLineSegment(sketch, "E1107", {"start": v(-53.25, 4.3) * mm, "end": v(-53.28, 3.91) * mm});
            skLineSegment(sketch, "E1108", {"start": v(-53.28, 3.91) * mm, "end": v(-53.3, 3.52) * mm});
            skLineSegment(sketch, "E1109", {"start": v(-53.3, 3.52) * mm, "end": v(-53.33, 3.12) * mm});
            skLineSegment(sketch, "E1110", {"start": v(-53.33, 3.12) * mm, "end": v(-53.36, 2.73) * mm});
            skLineSegment(sketch, "E1111", {"start": v(-53.36, 2.73) * mm, "end": v(-53.39, 2.34) * mm});
            skLineSegment(sketch, "E1112", {"start": v(-53.39, 2.34) * mm, "end": v(-53.42, 1.95) * mm});
            skLineSegment(sketch, "E1113", {"start": v(-53.42, 1.95) * mm, "end": v(-53.45, 1.55) * mm});
            skLineSegment(sketch, "E1114", {"start": v(-53.45, 1.55) * mm, "end": v(-53.45, 1.46) * mm});
            skLineSegment(sketch, "E1115", {"start": v(-53.45, 1.46) * mm, "end": v(-53.85, 1.47) * mm});
            skLineSegment(sketch, "E1116", {"start": v(-53.85, 1.47) * mm, "end": v(-54.24, 1.48) * mm});
            skLineSegment(sketch, "E1117", {"start": v(-54.24, 1.48) * mm, "end": v(-54.64, 1.5) * mm});
            skLineSegment(sketch, "E1118", {"start": v(-54.64, 1.5) * mm, "end": v(-55.03, 1.5) * mm});
            skLineSegment(sketch, "E1119", {"start": v(-55.03, 1.5) * mm, "end": v(-55.43, 1.52) * mm});
            skLineSegment(sketch, "E1120", {"start": v(-55.43, 1.52) * mm, "end": v(-55.82, 1.53) * mm});
            skLineSegment(sketch, "E1121", {"start": v(-55.82, 1.53) * mm, "end": v(-56.22, 1.54) * mm});
            skLineSegment(sketch, "E1122", {"start": v(-56.22, 1.54) * mm, "end": v(-56.61, 1.55) * mm});
            skLineSegment(sketch, "E1123", {"start": v(-56.61, 1.55) * mm, "end": v(-57.01, 1.56) * mm});
            skLineSegment(sketch, "E1124", {"start": v(-57.01, 1.56) * mm, "end": v(-57.4, 1.57) * mm});
            skLineSegment(sketch, "E1125", {"start": v(-57.4, 1.57) * mm, "end": v(-57.8, 1.59) * mm});
            skLineSegment(sketch, "E1126", {"start": v(-57.8, 1.59) * mm, "end": v(-58.2, 1.6) * mm});
            skLineSegment(sketch, "E1127", {"start": v(-58.2, 1.6) * mm, "end": v(-58.54, 1.6) * mm});
            skLineSegment(sketch, "E1128", {"start": v(-58.54, 1.6) * mm, "end": v(-58.96, 1.56) * mm});
            skLineSegment(sketch, "E1129", {"start": v(-58.96, 1.56) * mm, "end": v(-59.35, 1.4) * mm});
            skLineSegment(sketch, "E1130", {"start": v(-59.35, 1.4) * mm, "end": v(-59.69, 1.14) * mm});
            skLineSegment(sketch, "E1131", {"start": v(-59.69, 1.14) * mm, "end": v(-59.95, 0.8) * mm});
            skLineSegment(sketch, "E1132", {"start": v(-59.95, 0.8) * mm, "end": v(-60.11, 0.42) * mm});
            skLineSegment(sketch, "E1133", {"start": v(-60.11, 0.42) * mm, "end": v(-60.17, 0) * mm});
            skLineSegment(sketch, "E1134", {"start": v(-60.17, 0) * mm, "end": v(-60.11, -0.42) * mm});
            skLineSegment(sketch, "E1135", {"start": v(-60.11, -0.42) * mm, "end": v(-59.95, -0.81) * mm});
            skLineSegment(sketch, "E1136", {"start": v(-59.95, -0.81) * mm, "end": v(-59.69, -1.15) * mm});
            skLineSegment(sketch, "E1137", {"start": v(-59.69, -1.15) * mm, "end": v(-59.35, -1.4) * mm});
            skLineSegment(sketch, "E1138", {"start": v(-59.35, -1.4) * mm, "end": v(-58.96, -1.56) * mm});
            skLineSegment(sketch, "E1139", {"start": v(-58.96, -1.56) * mm, "end": v(-58.54, -1.6) * mm});
            skLineSegment(sketch, "E1140", {"start": v(-58.54, -1.6) * mm, "end": v(-58.14, -1.6) * mm});
            skLineSegment(sketch, "E1141", {"start": v(-58.14, -1.6) * mm, "end": v(-57.75, -1.59) * mm});
            skLineSegment(sketch, "E1142", {"start": v(-57.75, -1.59) * mm, "end": v(-57.35, -1.58) * mm});
            skLineSegment(sketch, "E1143", {"start": v(-57.35, -1.58) * mm, "end": v(-56.96, -1.56) * mm});
            skLineSegment(sketch, "E1144", {"start": v(-56.96, -1.56) * mm, "end": v(-56.56, -1.55) * mm});
            skLineSegment(sketch, "E1145", {"start": v(-56.56, -1.55) * mm, "end": v(-56.16, -1.54) * mm});
            skLineSegment(sketch, "E1146", {"start": v(-56.16, -1.54) * mm, "end": v(-55.77, -1.53) * mm});
            skLineSegment(sketch, "E1147", {"start": v(-55.77, -1.53) * mm, "end": v(-55.38, -1.52) * mm});
            skLineSegment(sketch, "E1148", {"start": v(-55.38, -1.52) * mm, "end": v(-54.98, -1.5) * mm});
            skLineSegment(sketch, "E1149", {"start": v(-54.98, -1.5) * mm, "end": v(-54.58, -1.5) * mm});
            skLineSegment(sketch, "E1150", {"start": v(-54.58, -1.5) * mm, "end": v(-54.2, -1.49) * mm});
            skLineSegment(sketch, "E1151", {"start": v(-54.2, -1.49) * mm, "end": v(-53.8, -1.47) * mm});
            skLineSegment(sketch, "E1152", {"start": v(-53.8, -1.47) * mm, "end": v(-53.45, -1.46) * mm});
            skLineSegment(sketch, "E1153", {"start": v(-53.45, -1.46) * mm, "end": v(-53.42, -1.86) * mm});
            skLineSegment(sketch, "E1154", {"start": v(-53.42, -1.86) * mm, "end": v(-53.4, -2.25) * mm});
            skLineSegment(sketch, "E1155", {"start": v(-53.4, -2.25) * mm, "end": v(-53.37, -2.64) * mm});
            skLineSegment(sketch, "E1156", {"start": v(-53.37, -2.64) * mm, "end": v(-53.34, -3.04) * mm});
            skLineSegment(sketch, "E1157", {"start": v(-53.34, -3.04) * mm, "end": v(-53.31, -3.43) * mm});
            skLineSegment(sketch, "E1158", {"start": v(-53.31, -3.43) * mm, "end": v(-53.28, -3.82) * mm});
            skLineSegment(sketch, "E1159", {"start": v(-53.28, -3.82) * mm, "end": v(-53.26, -4.21) * mm});
            skLineSegment(sketch, "E1160", {"start": v(-53.26, -4.21) * mm, "end": v(-53.23, -4.6) * mm});
            skLineSegment(sketch, "E1161", {"start": v(-53.23, -4.6) * mm, "end": v(-53.2, -5) * mm});
            skLineSegment(sketch, "E1162", {"start": v(-53.2, -5) * mm, "end": v(-53.17, -5.4) * mm});
            skLineSegment(sketch, "E1163", {"start": v(-53.17, -5.4) * mm, "end": v(-53.14, -5.79) * mm});
            skLineSegment(sketch, "E1164", {"start": v(-53.14, -5.79) * mm, "end": v(-53.14, -5.88) * mm});
            skLineSegment(sketch, "E1165", {"start": v(-53.14, -5.88) * mm, "end": v(-53.53, -5.92) * mm});
            skLineSegment(sketch, "E1166", {"start": v(-53.53, -5.92) * mm, "end": v(-53.92, -5.97) * mm});
            skLineSegment(sketch, "E1167", {"start": v(-53.92, -5.97) * mm, "end": v(-54.32, -6.01) * mm});
            skLineSegment(sketch, "E1168", {"start": v(-54.32, -6.01) * mm, "end": v(-54.7, -6.06) * mm});
            skLineSegment(sketch, "E1169", {"start": v(-54.7, -6.06) * mm, "end": v(-55.1, -6.1) * mm});
            skLineSegment(sketch, "E1170", {"start": v(-55.1, -6.1) * mm, "end": v(-55.5, -6.15) * mm});
            skLineSegment(sketch, "E1171", {"start": v(-55.5, -6.15) * mm, "end": v(-55.89, -6.2) * mm});
            skLineSegment(sketch, "E1172", {"start": v(-55.89, -6.2) * mm, "end": v(-56.28, -6.24) * mm});
            skLineSegment(sketch, "E1173", {"start": v(-56.28, -6.24) * mm, "end": v(-56.67, -6.28) * mm});
            skLineSegment(sketch, "E1174", {"start": v(-56.67, -6.28) * mm, "end": v(-57.06, -6.33) * mm});
            skLineSegment(sketch, "E1175", {"start": v(-57.06, -6.33) * mm, "end": v(-57.46, -6.37) * mm});
            skLineSegment(sketch, "E1176", {"start": v(-57.46, -6.37) * mm, "end": v(-57.85, -6.42) * mm});
            skLineSegment(sketch, "E1177", {"start": v(-57.85, -6.42) * mm, "end": v(-58.27, -6.47) * mm});
            skLineSegment(sketch, "E1178", {"start": v(-58.27, -6.47) * mm, "end": v(-58.68, -6.6) * mm});
            skLineSegment(sketch, "E1179", {"start": v(-58.68, -6.6) * mm, "end": v(-59.03, -6.83) * mm});
            skLineSegment(sketch, "E1180", {"start": v(-59.03, -6.83) * mm, "end": v(-59.31, -7.15) * mm});
            skLineSegment(sketch, "E1181", {"start": v(-59.31, -7.15) * mm, "end": v(-59.5, -7.53) * mm});
            skLineSegment(sketch, "E1182", {"start": v(-59.5, -7.53) * mm, "end": v(-59.59, -7.94) * mm});
            skLineSegment(sketch, "E1183", {"start": v(-59.59, -7.94) * mm, "end": v(-59.57, -8.28) * mm});
            skLineSegment(sketch, "E1184", {"start": v(-59.57, -8.28) * mm, "end": v(-59.46, -8.69) * mm});
            skLineSegment(sketch, "E1185", {"start": v(-59.46, -8.69) * mm, "end": v(-59.24, -9.05) * mm});
            skLineSegment(sketch, "E1186", {"start": v(-59.24, -9.05) * mm, "end": v(-58.94, -9.35) * mm});
            skLineSegment(sketch, "E1187", {"start": v(-58.94, -9.35) * mm, "end": v(-58.57, -9.55) * mm});
            skLineSegment(sketch, "E1188", {"start": v(-58.57, -9.55) * mm, "end": v(-58.15, -9.65) * mm});
            skLineSegment(sketch, "E1189", {"start": v(-58.15, -9.65) * mm, "end": v(-57.73, -9.64) * mm});
            skLineSegment(sketch, "E1190", {"start": v(-57.73, -9.64) * mm, "end": v(-57.34, -9.57) * mm});
            skLineSegment(sketch, "E1191", {"start": v(-57.34, -9.57) * mm, "end": v(-56.96, -9.5) * mm});
            skLineSegment(sketch, "E1192", {"start": v(-56.96, -9.5) * mm, "end": v(-56.56, -9.44) * mm});
            skLineSegment(sketch, "E1193", {"start": v(-56.56, -9.44) * mm, "end": v(-56.17, -9.37) * mm});
            skLineSegment(sketch, "E1194", {"start": v(-56.17, -9.37) * mm, "end": v(-55.79, -9.3) * mm});
            skLineSegment(sketch, "E1195", {"start": v(-55.79, -9.3) * mm, "end": v(-55.4, -9.24) * mm});
            skLineSegment(sketch, "E1196", {"start": v(-55.4, -9.24) * mm, "end": v(-55, -9.17) * mm});
            skLineSegment(sketch, "E1197", {"start": v(-55, -9.17) * mm, "end": v(-54.62, -9.1) * mm});
            skLineSegment(sketch, "E1198", {"start": v(-54.62, -9.1) * mm, "end": v(-54.22, -9.03) * mm});
            skLineSegment(sketch, "E1199", {"start": v(-54.22, -9.03) * mm, "end": v(-53.84, -8.97) * mm});
            skLineSegment(sketch, "E1200", {"start": v(-53.84, -8.97) * mm, "end": v(-53.45, -8.9) * mm});
            skLineSegment(sketch, "E1201", {"start": v(-53.45, -8.9) * mm, "end": v(-53.05, -8.83) * mm});
            skLineSegment(sketch, "E1202", {"start": v(-53.05, -8.83) * mm, "end": v(-52.72, -8.77) * mm});
            skLineSegment(sketch, "E1203", {"start": v(-52.72, -8.77) * mm, "end": v(-52.64, -9.16) * mm});
            skLineSegment(sketch, "E1204", {"start": v(-52.64, -9.16) * mm, "end": v(-52.55, -9.54) * mm});
            skLineSegment(sketch, "E1205", {"start": v(-52.55, -9.54) * mm, "end": v(-52.47, -9.93) * mm});
            skLineSegment(sketch, "E1206", {"start": v(-52.47, -9.93) * mm, "end": v(-52.39, -10.31) * mm});
            skLineSegment(sketch, "E1207", {"start": v(-52.39, -10.31) * mm, "end": v(-52.3, -10.7) * mm});
            skLineSegment(sketch, "E1208", {"start": v(-52.3, -10.7) * mm, "end": v(-52.22, -11.08) * mm});
            skLineSegment(sketch, "E1209", {"start": v(-52.22, -11.08) * mm, "end": v(-52.13, -11.47) * mm});
            skLineSegment(sketch, "E1210", {"start": v(-52.13, -11.47) * mm, "end": v(-52.05, -11.85) * mm});
            skLineSegment(sketch, "E1211", {"start": v(-52.05, -11.85) * mm, "end": v(-51.97, -12.24) * mm});
            skLineSegment(sketch, "E1212", {"start": v(-51.97, -12.24) * mm, "end": v(-51.88, -12.62) * mm});
            skLineSegment(sketch, "E1213", {"start": v(-51.88, -12.62) * mm, "end": v(-51.8, -13) * mm});
            skLineSegment(sketch, "E1214", {"start": v(-51.8, -13) * mm, "end": v(-51.78, -13.1) * mm});
            skLineSegment(sketch, "E1215", {"start": v(-51.78, -13.1) * mm, "end": v(-52.16, -13.2) * mm});
            skLineSegment(sketch, "E1216", {"start": v(-52.16, -13.2) * mm, "end": v(-52.54, -13.3) * mm});
            skLineSegment(sketch, "E1217", {"start": v(-52.54, -13.3) * mm, "end": v(-52.93, -13.4) * mm});
            skLineSegment(sketch, "E1218", {"start": v(-52.93, -13.4) * mm, "end": v(-53.3, -13.5) * mm});
            skLineSegment(sketch, "E1219", {"start": v(-53.3, -13.5) * mm, "end": v(-53.69, -13.6) * mm});
            skLineSegment(sketch, "E1220", {"start": v(-53.69, -13.6) * mm, "end": v(-54.08, -13.7) * mm});
            skLineSegment(sketch, "E1221", {"start": v(-54.08, -13.7) * mm, "end": v(-54.46, -13.8) * mm});
            skLineSegment(sketch, "E1222", {"start": v(-54.46, -13.8) * mm, "end": v(-54.84, -13.9) * mm});
            skLineSegment(sketch, "E1223", {"start": v(-54.84, -13.9) * mm, "end": v(-55.22, -14) * mm});
            skLineSegment(sketch, "E1224", {"start": v(-55.22, -14) * mm, "end": v(-55.6, -14.1) * mm});
            skLineSegment(sketch, "E1225", {"start": v(-55.6, -14.1) * mm, "end": v(-55.98, -14.2) * mm});
            skLineSegment(sketch, "E1226", {"start": v(-55.98, -14.2) * mm, "end": v(-56.37, -14.3) * mm});
            skLineSegment(sketch, "E1227", {"start": v(-56.37, -14.3) * mm, "end": v(-56.78, -14.41) * mm});
            skLineSegment(sketch, "E1228", {"start": v(-56.78, -14.41) * mm, "end": v(-57.16, -14.6) * mm});
            skLineSegment(sketch, "E1229", {"start": v(-57.16, -14.6) * mm, "end": v(-57.48, -14.88) * mm});
            skLineSegment(sketch, "E1230", {"start": v(-57.48, -14.88) * mm, "end": v(-57.71, -15.23) * mm});
            skLineSegment(sketch, "E1231", {"start": v(-57.71, -15.23) * mm, "end": v(-57.85, -15.63) * mm});
            skLineSegment(sketch, "E1232", {"start": v(-57.85, -15.63) * mm, "end": v(-57.87, -16.06) * mm});
            skLineSegment(sketch, "E1233", {"start": v(-57.87, -16.06) * mm, "end": v(-57.8, -16.4) * mm});
            skLineSegment(sketch, "E1234", {"start": v(-57.8, -16.4) * mm, "end": v(-57.64, -16.78) * mm});
            skLineSegment(sketch, "E1235", {"start": v(-57.64, -16.78) * mm, "end": v(-57.37, -17.1) * mm});
            skLineSegment(sketch, "E1236", {"start": v(-57.37, -17.1) * mm, "end": v(-57.03, -17.35) * mm});
            skLineSegment(sketch, "E1237", {"start": v(-57.03, -17.35) * mm, "end": v(-56.63, -17.5) * mm});
            skLineSegment(sketch, "E1238", {"start": v(-56.63, -17.5) * mm, "end": v(-56.2, -17.55) * mm});
            skLineSegment(sketch, "E1239", {"start": v(-56.2, -17.55) * mm, "end": v(-55.8, -17.47) * mm});
            skLineSegment(sketch, "E1240", {"start": v(-55.8, -17.47) * mm, "end": v(-55.42, -17.35) * mm});
            skLineSegment(sketch, "E1241", {"start": v(-55.42, -17.35) * mm, "end": v(-55.04, -17.23) * mm});
            skLineSegment(sketch, "E1242", {"start": v(-55.04, -17.23) * mm, "end": v(-54.66, -17.1) * mm});
            skLineSegment(sketch, "E1243", {"start": v(-54.66, -17.1) * mm, "end": v(-54.29, -16.99) * mm});
            skLineSegment(sketch, "E1244", {"start": v(-54.29, -16.99) * mm, "end": v(-53.91, -16.86) * mm});
            skLineSegment(sketch, "E1245", {"start": v(-53.91, -16.86) * mm, "end": v(-53.54, -16.74) * mm});
            skLineSegment(sketch, "E1246", {"start": v(-53.54, -16.74) * mm, "end": v(-53.16, -16.62) * mm});
            skLineSegment(sketch, "E1247", {"start": v(-53.16, -16.62) * mm, "end": v(-52.79, -16.5) * mm});
            skLineSegment(sketch, "E1248", {"start": v(-52.79, -16.5) * mm, "end": v(-52.4, -16.37) * mm});
            skLineSegment(sketch, "E1249", {"start": v(-52.4, -16.37) * mm, "end": v(-52.03, -16.25) * mm});
            skLineSegment(sketch, "E1250", {"start": v(-52.03, -16.25) * mm, "end": v(-51.66, -16.13) * mm});
            skLineSegment(sketch, "E1251", {"start": v(-51.66, -16.13) * mm, "end": v(-51.28, -16) * mm});
            skLineSegment(sketch, "E1252", {"start": v(-51.28, -16) * mm, "end": v(-50.96, -15.9) * mm});
            skLineSegment(sketch, "E1253", {"start": v(-50.96, -15.9) * mm, "end": v(-50.82, -16.27) * mm});
            skLineSegment(sketch, "E1254", {"start": v(-50.82, -16.27) * mm, "end": v(-50.68, -16.64) * mm});
            skLineSegment(sketch, "E1255", {"start": v(-50.68, -16.64) * mm, "end": v(-50.54, -17.01) * mm});
            skLineSegment(sketch, "E1256", {"start": v(-50.54, -17.01) * mm, "end": v(-50.4, -17.38) * mm});
            skLineSegment(sketch, "E1257", {"start": v(-50.4, -17.38) * mm, "end": v(-50.27, -17.75) * mm});
            skLineSegment(sketch, "E1258", {"start": v(-50.27, -17.75) * mm, "end": v(-50.13, -18.12) * mm});
            skLineSegment(sketch, "E1259", {"start": v(-50.13, -18.12) * mm, "end": v(-50, -18.49) * mm});
            skLineSegment(sketch, "E1260", {"start": v(-50, -18.49) * mm, "end": v(-49.85, -18.86) * mm});
            skLineSegment(sketch, "E1261", {"start": v(-49.85, -18.86) * mm, "end": v(-49.72, -19.22) * mm});
            skLineSegment(sketch, "E1262", {"start": v(-49.72, -19.22) * mm, "end": v(-49.58, -19.6) * mm});
            skLineSegment(sketch, "E1263", {"start": v(-49.58, -19.6) * mm, "end": v(-49.44, -19.96) * mm});
            skLineSegment(sketch, "E1264", {"start": v(-49.44, -19.96) * mm, "end": v(-49.4, -20.05) * mm});
            skLineSegment(sketch, "E1265", {"start": v(-49.4, -20.05) * mm, "end": v(-49.77, -20.2) * mm});
            skLineSegment(sketch, "E1266", {"start": v(-49.77, -20.2) * mm, "end": v(-50.14, -20.36) * mm});
            skLineSegment(sketch, "E1267", {"start": v(-50.14, -20.36) * mm, "end": v(-50.5, -20.51) * mm});
            skLineSegment(sketch, "E1268", {"start": v(-50.5, -20.51) * mm, "end": v(-50.87, -20.66) * mm});
            skLineSegment(sketch, "E1269", {"start": v(-50.87, -20.66) * mm, "end": v(-51.23, -20.82) * mm});
            skLineSegment(sketch, "E1270", {"start": v(-51.23, -20.82) * mm, "end": v(-51.6, -20.97) * mm});
            skLineSegment(sketch, "E1271", {"start": v(-51.6, -20.97) * mm, "end": v(-51.96, -21.13) * mm});
            skLineSegment(sketch, "E1272", {"start": v(-51.96, -21.13) * mm, "end": v(-52.32, -21.28) * mm});
            skLineSegment(sketch, "E1273", {"start": v(-52.32, -21.28) * mm, "end": v(-52.69, -21.43) * mm});
            skLineSegment(sketch, "E1274", {"start": v(-52.69, -21.43) * mm, "end": v(-53.05, -21.59) * mm});
            skLineSegment(sketch, "E1275", {"start": v(-53.05, -21.59) * mm, "end": v(-53.41, -21.74) * mm});
            skLineSegment(sketch, "E1276", {"start": v(-53.41, -21.74) * mm, "end": v(-53.78, -21.9) * mm});
            skLineSegment(sketch, "E1277", {"start": v(-53.78, -21.9) * mm, "end": v(-54.17, -22.06) * mm});
            skLineSegment(sketch, "E1278", {"start": v(-54.17, -22.06) * mm, "end": v(-54.52, -22.3) * mm});
            skLineSegment(sketch, "E1279", {"start": v(-54.52, -22.3) * mm, "end": v(-54.8, -22.63) * mm});
            skLineSegment(sketch, "E1280", {"start": v(-54.8, -22.63) * mm, "end": v(-54.98, -23) * mm});
            skLineSegment(sketch, "E1281", {"start": v(-54.98, -23) * mm, "end": v(-55.05, -23.42) * mm});
            skLineSegment(sketch, "E1282", {"start": v(-55.05, -23.42) * mm, "end": v(-55.02, -23.85) * mm});
            skLineSegment(sketch, "E1283", {"start": v(-55.02, -23.85) * mm, "end": v(-54.9, -24.17) * mm});
            skLineSegment(sketch, "E1284", {"start": v(-54.9, -24.17) * mm, "end": v(-54.68, -24.53) * mm});
            skLineSegment(sketch, "E1285", {"start": v(-54.68, -24.53) * mm, "end": v(-54.37, -24.81) * mm});
            skLineSegment(sketch, "E1286", {"start": v(-54.37, -24.81) * mm, "end": v(-54, -25.01) * mm});
            skLineSegment(sketch, "E1287", {"start": v(-54, -25.01) * mm, "end": v(-53.58, -25.1) * mm});
            skLineSegment(sketch, "E1288", {"start": v(-53.58, -25.1) * mm, "end": v(-53.16, -25.08) * mm});
            skLineSegment(sketch, "E1289", {"start": v(-53.16, -25.08) * mm, "end": v(-52.76, -24.95) * mm});
            skLineSegment(sketch, "E1290", {"start": v(-52.76, -24.95) * mm, "end": v(-52.4, -24.78) * mm});
            skLineSegment(sketch, "E1291", {"start": v(-52.4, -24.78) * mm, "end": v(-52.05, -24.6) * mm});
            skLineSegment(sketch, "E1292", {"start": v(-52.05, -24.6) * mm, "end": v(-51.7, -24.43) * mm});
            skLineSegment(sketch, "E1293", {"start": v(-51.7, -24.43) * mm, "end": v(-51.34, -24.26) * mm});
            skLineSegment(sketch, "E1294", {"start": v(-51.34, -24.26) * mm, "end": v(-50.99, -24.08) * mm});
            skLineSegment(sketch, "E1295", {"start": v(-50.99, -24.08) * mm, "end": v(-50.63, -23.9) * mm});
            skLineSegment(sketch, "E1296", {"start": v(-50.63, -23.9) * mm, "end": v(-50.27, -23.73) * mm});
            skLineSegment(sketch, "E1297", {"start": v(-50.27, -23.73) * mm, "end": v(-49.92, -23.56) * mm});
            skLineSegment(sketch, "E1298", {"start": v(-49.92, -23.56) * mm, "end": v(-49.56, -23.38) * mm});
            skLineSegment(sketch, "E1299", {"start": v(-49.56, -23.38) * mm, "end": v(-49.2, -23.2) * mm});
            skLineSegment(sketch, "E1300", {"start": v(-49.2, -23.2) * mm, "end": v(-48.86, -23.04) * mm});
            skLineSegment(sketch, "E1301", {"start": v(-48.86, -23.04) * mm, "end": v(-48.5, -22.86) * mm});
            skLineSegment(sketch, "E1302", {"start": v(-48.5, -22.86) * mm, "end": v(-48.2, -22.71) * mm});
            skLineSegment(sketch, "E1303", {"start": v(-48.2, -22.71) * mm, "end": v(-48, -23.06) * mm});
            skLineSegment(sketch, "E1304", {"start": v(-48, -23.06) * mm, "end": v(-47.82, -23.4) * mm});
            skLineSegment(sketch, "E1305", {"start": v(-47.82, -23.4) * mm, "end": v(-47.63, -23.75) * mm});
            skLineSegment(sketch, "E1306", {"start": v(-47.63, -23.75) * mm, "end": v(-47.44, -24.1) * mm});
            skLineSegment(sketch, "E1307", {"start": v(-47.44, -24.1) * mm, "end": v(-47.25, -24.44) * mm});
            skLineSegment(sketch, "E1308", {"start": v(-47.25, -24.44) * mm, "end": v(-47.06, -24.78) * mm});
            skLineSegment(sketch, "E1309", {"start": v(-47.06, -24.78) * mm, "end": v(-46.87, -25.13) * mm});
            skLineSegment(sketch, "E1310", {"start": v(-46.87, -25.13) * mm, "end": v(-46.68, -25.48) * mm});
            skLineSegment(sketch, "E1311", {"start": v(-46.68, -25.48) * mm, "end": v(-46.5, -25.82) * mm});
            skLineSegment(sketch, "E1312", {"start": v(-46.5, -25.82) * mm, "end": v(-46.3, -26.17) * mm});
            skLineSegment(sketch, "E1313", {"start": v(-46.3, -26.17) * mm, "end": v(-46.12, -26.51) * mm});
            skLineSegment(sketch, "E1314", {"start": v(-46.12, -26.51) * mm, "end": v(-46.07, -26.6) * mm});
            skLineSegment(sketch, "E1315", {"start": v(-46.07, -26.6) * mm, "end": v(-46.41, -26.8) * mm});
            skLineSegment(sketch, "E1316", {"start": v(-46.41, -26.8) * mm, "end": v(-46.75, -27) * mm});
            skLineSegment(sketch, "E1317", {"start": v(-46.75, -27) * mm, "end": v(-47.1, -27.2) * mm});
            skLineSegment(sketch, "E1318", {"start": v(-47.1, -27.2) * mm, "end": v(-47.43, -27.4) * mm});
            skLineSegment(sketch, "E1319", {"start": v(-47.43, -27.4) * mm, "end": v(-47.76, -27.61) * mm});
            skLineSegment(sketch, "E1320", {"start": v(-47.76, -27.61) * mm, "end": v(-48.1, -27.82) * mm});
            skLineSegment(sketch, "E1321", {"start": v(-48.1, -27.82) * mm, "end": v(-48.44, -28.02) * mm});
            skLineSegment(sketch, "E1322", {"start": v(-48.44, -28.02) * mm, "end": v(-48.78, -28.23) * mm});
            skLineSegment(sketch, "E1323", {"start": v(-48.78, -28.23) * mm, "end": v(-49.12, -28.43) * mm});
            skLineSegment(sketch, "E1324", {"start": v(-49.12, -28.43) * mm, "end": v(-49.46, -28.63) * mm});
            skLineSegment(sketch, "E1325", {"start": v(-49.46, -28.63) * mm, "end": v(-49.8, -28.84) * mm});
            skLineSegment(sketch, "E1326", {"start": v(-49.8, -28.84) * mm, "end": v(-50.14, -29.04) * mm});
            skLineSegment(sketch, "E1327", {"start": v(-50.14, -29.04) * mm, "end": v(-50.5, -29.27) * mm});
            skLineSegment(sketch, "E1328", {"start": v(-50.5, -29.27) * mm, "end": v(-50.81, -29.55) * mm});
            skLineSegment(sketch, "E1329", {"start": v(-50.81, -29.55) * mm, "end": v(-51.04, -29.91) * mm});
            skLineSegment(sketch, "E1330", {"start": v(-51.04, -29.91) * mm, "end": v(-51.16, -30.31) * mm});
            skLineSegment(sketch, "E1331", {"start": v(-51.16, -30.31) * mm, "end": v(-51.18, -30.74) * mm});
            skLineSegment(sketch, "E1332", {"start": v(-51.18, -30.74) * mm, "end": v(-51.08, -31.15) * mm});
            skLineSegment(sketch, "E1333", {"start": v(-51.08, -31.15) * mm, "end": v(-50.93, -31.45) * mm});
            skLineSegment(sketch, "E1334", {"start": v(-50.93, -31.45) * mm, "end": v(-50.66, -31.78) * mm});
            skLineSegment(sketch, "E1335", {"start": v(-50.66, -31.78) * mm, "end": v(-50.3, -32.02) * mm});
            skLineSegment(sketch, "E1336", {"start": v(-50.3, -32.02) * mm, "end": v(-49.9, -32.16) * mm});
            skLineSegment(sketch, "E1337", {"start": v(-49.9, -32.16) * mm, "end": v(-49.49, -32.19) * mm});
            skLineSegment(sketch, "E1338", {"start": v(-49.49, -32.19) * mm, "end": v(-49.07, -32.1) * mm});
            skLineSegment(sketch, "E1339", {"start": v(-49.07, -32.1) * mm, "end": v(-48.7, -31.92) * mm});
            skLineSegment(sketch, "E1340", {"start": v(-48.7, -31.92) * mm, "end": v(-48.37, -31.7) * mm});
            skLineSegment(sketch, "E1341", {"start": v(-48.37, -31.7) * mm, "end": v(-48.04, -31.48) * mm});
            skLineSegment(sketch, "E1342", {"start": v(-48.04, -31.48) * mm, "end": v(-47.71, -31.25) * mm});
            skLineSegment(sketch, "E1343", {"start": v(-47.71, -31.25) * mm, "end": v(-47.39, -31.03) * mm});
            skLineSegment(sketch, "E1344", {"start": v(-47.39, -31.03) * mm, "end": v(-47.06, -30.81) * mm});
            skLineSegment(sketch, "E1345", {"start": v(-47.06, -30.81) * mm, "end": v(-46.73, -30.59) * mm});
            skLineSegment(sketch, "E1346", {"start": v(-46.73, -30.59) * mm, "end": v(-46.4, -30.36) * mm});
            skLineSegment(sketch, "E1347", {"start": v(-46.4, -30.36) * mm, "end": v(-46.08, -30.14) * mm});
            skLineSegment(sketch, "E1348", {"start": v(-46.08, -30.14) * mm, "end": v(-45.75, -29.92) * mm});
            skLineSegment(sketch, "E1349", {"start": v(-45.75, -29.92) * mm, "end": v(-45.43, -29.7) * mm});
            skLineSegment(sketch, "E1350", {"start": v(-45.43, -29.7) * mm, "end": v(-45.1, -29.47) * mm});
            skLineSegment(sketch, "E1351", {"start": v(-45.1, -29.47) * mm, "end": v(-44.77, -29.25) * mm});
            skLineSegment(sketch, "E1352", {"start": v(-44.77, -29.25) * mm, "end": v(-44.5, -29.05) * mm});
            skLineSegment(sketch, "E1353", {"start": v(-44.5, -29.05) * mm, "end": v(-44.26, -29.37) * mm});
            skLineSegment(sketch, "E1354", {"start": v(-44.26, -29.37) * mm, "end": v(-44.02, -29.69) * mm});
            skLineSegment(sketch, "E1355", {"start": v(-44.02, -29.69) * mm, "end": v(-43.78, -30) * mm});
            skLineSegment(sketch, "E1356", {"start": v(-43.78, -30) * mm, "end": v(-43.55, -30.32) * mm});
            skLineSegment(sketch, "E1357", {"start": v(-43.55, -30.32) * mm, "end": v(-43.31, -30.63) * mm});
            skLineSegment(sketch, "E1358", {"start": v(-43.31, -30.63) * mm, "end": v(-43.08, -30.95) * mm});
            skLineSegment(sketch, "E1359", {"start": v(-43.08, -30.95) * mm, "end": v(-42.84, -31.26) * mm});
            skLineSegment(sketch, "E1360", {"start": v(-42.84, -31.26) * mm, "end": v(-42.6, -31.58) * mm});
            skLineSegment(sketch, "E1361", {"start": v(-42.6, -31.58) * mm, "end": v(-42.37, -31.9) * mm});
            skLineSegment(sketch, "E1362", {"start": v(-42.37, -31.9) * mm, "end": v(-42.13, -32.2) * mm});
            skLineSegment(sketch, "E1363", {"start": v(-42.13, -32.2) * mm, "end": v(-41.9, -32.52) * mm});
            skLineSegment(sketch, "E1364", {"start": v(-41.9, -32.52) * mm, "end": v(-41.84, -32.6) * mm});
            skLineSegment(sketch, "E1365", {"start": v(-41.84, -32.6) * mm, "end": v(-42.15, -32.85) * mm});
            skLineSegment(sketch, "E1366", {"start": v(-42.15, -32.85) * mm, "end": v(-42.45, -33.1) * mm});
            skLineSegment(sketch, "E1367", {"start": v(-42.45, -33.1) * mm, "end": v(-42.76, -33.35) * mm});
            skLineSegment(sketch, "E1368", {"start": v(-42.76, -33.35) * mm, "end": v(-43.06, -33.6) * mm});
            skLineSegment(sketch, "E1369", {"start": v(-43.06, -33.6) * mm, "end": v(-43.37, -33.85) * mm});
            skLineSegment(sketch, "E1370", {"start": v(-43.37, -33.85) * mm, "end": v(-43.68, -34.1) * mm});
            skLineSegment(sketch, "E1371", {"start": v(-43.68, -34.1) * mm, "end": v(-43.98, -34.35) * mm});
            skLineSegment(sketch, "E1372", {"start": v(-43.98, -34.35) * mm, "end": v(-44.29, -34.6) * mm});
            skLineSegment(sketch, "E1373", {"start": v(-44.29, -34.6) * mm, "end": v(-44.6, -34.85) * mm});
            skLineSegment(sketch, "E1374", {"start": v(-44.6, -34.85) * mm, "end": v(-44.9, -35.1) * mm});
            skLineSegment(sketch, "E1375", {"start": v(-44.9, -35.1) * mm, "end": v(-45.2, -35.35) * mm});
            skLineSegment(sketch, "E1376", {"start": v(-45.2, -35.35) * mm, "end": v(-45.51, -35.6) * mm});
            skLineSegment(sketch, "E1377", {"start": v(-45.51, -35.6) * mm, "end": v(-45.84, -35.87) * mm});
            skLineSegment(sketch, "E1378", {"start": v(-45.84, -35.87) * mm, "end": v(-46.1, -36.2) * mm});
            skLineSegment(sketch, "E1379", {"start": v(-46.1, -36.2) * mm, "end": v(-46.28, -36.59) * mm});
            skLineSegment(sketch, "E1380", {"start": v(-46.28, -36.59) * mm, "end": v(-46.35, -37) * mm});
            skLineSegment(sketch, "E1381", {"start": v(-46.35, -37) * mm, "end": v(-46.3, -37.43) * mm});
            skLineSegment(sketch, "E1382", {"start": v(-46.3, -37.43) * mm, "end": v(-46.15, -37.82) * mm});
            skLineSegment(sketch, "E1383", {"start": v(-46.15, -37.82) * mm, "end": v(-45.96, -38.1) * mm});
            skLineSegment(sketch, "E1384", {"start": v(-45.96, -38.1) * mm, "end": v(-45.64, -38.38) * mm});
            skLineSegment(sketch, "E1385", {"start": v(-45.64, -38.38) * mm, "end": v(-45.26, -38.57) * mm});
            skLineSegment(sketch, "E1386", {"start": v(-45.26, -38.57) * mm, "end": v(-44.85, -38.65) * mm});
            skLineSegment(sketch, "E1387", {"start": v(-44.85, -38.65) * mm, "end": v(-44.42, -38.62) * mm});
            skLineSegment(sketch, "E1388", {"start": v(-44.42, -38.62) * mm, "end": v(-44.02, -38.48) * mm});
            skLineSegment(sketch, "E1389", {"start": v(-44.02, -38.48) * mm, "end": v(-43.67, -38.25) * mm});
            skLineSegment(sketch, "E1390", {"start": v(-43.67, -38.25) * mm, "end": v(-43.38, -37.98) * mm});
            skLineSegment(sketch, "E1391", {"start": v(-43.38, -37.98) * mm, "end": v(-43.1, -37.71) * mm});
            skLineSegment(sketch, "E1392", {"start": v(-43.1, -37.71) * mm, "end": v(-42.8, -37.44) * mm});
            skLineSegment(sketch, "E1393", {"start": v(-42.8, -37.44) * mm, "end": v(-42.5, -37.18) * mm});
            skLineSegment(sketch, "E1394", {"start": v(-42.5, -37.18) * mm, "end": v(-42.22, -36.91) * mm});
            skLineSegment(sketch, "E1395", {"start": v(-42.22, -36.91) * mm, "end": v(-41.92, -36.64) * mm});
            skLineSegment(sketch, "E1396", {"start": v(-41.92, -36.64) * mm, "end": v(-41.63, -36.37) * mm});
            skLineSegment(sketch, "E1397", {"start": v(-41.63, -36.37) * mm, "end": v(-41.34, -36.1) * mm});
            skLineSegment(sketch, "E1398", {"start": v(-41.34, -36.1) * mm, "end": v(-41.05, -35.84) * mm});
            skLineSegment(sketch, "E1399", {"start": v(-41.05, -35.84) * mm, "end": v(-40.76, -35.57) * mm});
            skLineSegment(sketch, "E1400", {"start": v(-40.76, -35.57) * mm, "end": v(-40.47, -35.3) * mm});
            skLineSegment(sketch, "E1401", {"start": v(-40.47, -35.3) * mm, "end": v(-40.17, -35.04) * mm});
            skLineSegment(sketch, "E1402", {"start": v(-40.17, -35.04) * mm, "end": v(-39.92, -34.8) * mm});
            skLineSegment(sketch, "E1403", {"start": v(-39.92, -34.8) * mm, "end": v(-39.65, -35.09) * mm});
            skLineSegment(sketch, "E1404", {"start": v(-39.65, -35.09) * mm, "end": v(-39.37, -35.36) * mm});
            skLineSegment(sketch, "E1405", {"start": v(-39.37, -35.36) * mm, "end": v(-39.09, -35.64) * mm});
            skLineSegment(sketch, "E1406", {"start": v(-39.09, -35.64) * mm, "end": v(-38.81, -35.92) * mm});
            skLineSegment(sketch, "E1407", {"start": v(-38.81, -35.92) * mm, "end": v(-38.53, -36.2) * mm});
            skLineSegment(sketch, "E1408", {"start": v(-38.53, -36.2) * mm, "end": v(-38.25, -36.48) * mm});
            skLineSegment(sketch, "E1409", {"start": v(-38.25, -36.48) * mm, "end": v(-37.98, -36.76) * mm});
            skLineSegment(sketch, "E1410", {"start": v(-37.98, -36.76) * mm, "end": v(-37.7, -37.04) * mm});
            skLineSegment(sketch, "E1411", {"start": v(-37.7, -37.04) * mm, "end": v(-37.42, -37.31) * mm});
            skLineSegment(sketch, "E1412", {"start": v(-37.42, -37.31) * mm, "end": v(-37.14, -37.6) * mm});
            skLineSegment(sketch, "E1413", {"start": v(-37.14, -37.6) * mm, "end": v(-36.86, -37.87) * mm});
            skLineSegment(sketch, "E1414", {"start": v(-36.86, -37.87) * mm, "end": v(-36.8, -37.94) * mm});
            skLineSegment(sketch, "E1415", {"start": v(-36.8, -37.94) * mm, "end": v(-37.06, -38.23) * mm});
            skLineSegment(sketch, "E1416", {"start": v(-37.06, -38.23) * mm, "end": v(-37.33, -38.52) * mm});
            skLineSegment(sketch, "E1417", {"start": v(-37.33, -38.52) * mm, "end": v(-37.6, -38.8) * mm});
            skLineSegment(sketch, "E1418", {"start": v(-37.6, -38.8) * mm, "end": v(-37.87, -39.1) * mm});
            skLineSegment(sketch, "E1419", {"start": v(-37.87, -39.1) * mm, "end": v(-38.13, -39.4) * mm});
            skLineSegment(sketch, "E1420", {"start": v(-38.13, -39.4) * mm, "end": v(-38.4, -39.68) * mm});
            skLineSegment(sketch, "E1421", {"start": v(-38.4, -39.68) * mm, "end": v(-38.67, -39.97) * mm});
            skLineSegment(sketch, "E1422", {"start": v(-38.67, -39.97) * mm, "end": v(-38.93, -40.26) * mm});
            skLineSegment(sketch, "E1423", {"start": v(-38.93, -40.26) * mm, "end": v(-39.2, -40.56) * mm});
            skLineSegment(sketch, "E1424", {"start": v(-39.2, -40.56) * mm, "end": v(-39.47, -40.85) * mm});
            skLineSegment(sketch, "E1425", {"start": v(-39.47, -40.85) * mm, "end": v(-39.74, -41.14) * mm});
            skLineSegment(sketch, "E1426", {"start": v(-39.74, -41.14) * mm, "end": v(-40, -41.43) * mm});
            skLineSegment(sketch, "E1427", {"start": v(-40, -41.43) * mm, "end": v(-40.29, -41.75) * mm});
            skLineSegment(sketch, "E1428", {"start": v(-40.29, -41.75) * mm, "end": v(-40.5, -42.11) * mm});
            skLineSegment(sketch, "E1429", {"start": v(-40.5, -42.11) * mm, "end": v(-40.63, -42.52) * mm});
            skLineSegment(sketch, "E1430", {"start": v(-40.63, -42.52) * mm, "end": v(-40.63, -42.94) * mm});
            skLineSegment(sketch, "E1431", {"start": v(-40.63, -42.94) * mm, "end": v(-40.53, -43.35) * mm});
            skLineSegment(sketch, "E1432", {"start": v(-40.53, -43.35) * mm, "end": v(-40.32, -43.72) * mm});
            skLineSegment(sketch, "E1433", {"start": v(-40.32, -43.72) * mm, "end": v(-40.09, -43.97) * mm});
            skLineSegment(sketch, "E1434", {"start": v(-40.09, -43.97) * mm, "end": v(-39.73, -44.2) * mm});
            skLineSegment(sketch, "E1435", {"start": v(-39.73, -44.2) * mm, "end": v(-39.33, -44.33) * mm});
            skLineSegment(sketch, "E1436", {"start": v(-39.33, -44.33) * mm, "end": v(-38.9, -44.36) * mm});
            skLineSegment(sketch, "E1437", {"start": v(-38.9, -44.36) * mm, "end": v(-38.5, -44.27) * mm});
            skLineSegment(sketch, "E1438", {"start": v(-38.5, -44.27) * mm, "end": v(-38.12, -44.07) * mm});
            skLineSegment(sketch, "E1439", {"start": v(-38.12, -44.07) * mm, "end": v(-37.8, -43.79) * mm});
            skLineSegment(sketch, "E1440", {"start": v(-37.8, -43.79) * mm, "end": v(-37.56, -43.48) * mm});
            skLineSegment(sketch, "E1441", {"start": v(-37.56, -43.48) * mm, "end": v(-37.3, -43.18) * mm});
            skLineSegment(sketch, "E1442", {"start": v(-37.3, -43.18) * mm, "end": v(-37.05, -42.87) * mm});
            skLineSegment(sketch, "E1443", {"start": v(-37.05, -42.87) * mm, "end": v(-36.8, -42.56) * mm});
            skLineSegment(sketch, "E1444", {"start": v(-36.8, -42.56) * mm, "end": v(-36.55, -42.26) * mm});
            skLineSegment(sketch, "E1445", {"start": v(-36.55, -42.26) * mm, "end": v(-36.3, -41.95) * mm});
            skLineSegment(sketch, "E1446", {"start": v(-36.3, -41.95) * mm, "end": v(-36.05, -41.65) * mm});
            skLineSegment(sketch, "E1447", {"start": v(-36.05, -41.65) * mm, "end": v(-35.8, -41.34) * mm});
            skLineSegment(sketch, "E1448", {"start": v(-35.8, -41.34) * mm, "end": v(-35.55, -41.03) * mm});
            skLineSegment(sketch, "E1449", {"start": v(-35.55, -41.03) * mm, "end": v(-35.3, -40.73) * mm});
            skLineSegment(sketch, "E1450", {"start": v(-35.3, -40.73) * mm, "end": v(-35.05, -40.42) * mm});
            skLineSegment(sketch, "E1451", {"start": v(-35.05, -40.42) * mm, "end": v(-34.8, -40.11) * mm});
            skLineSegment(sketch, "E1452", {"start": v(-34.8, -40.11) * mm, "end": v(-34.59, -39.85) * mm});
            skLineSegment(sketch, "E1453", {"start": v(-34.59, -39.85) * mm, "end": v(-34.27, -40.09) * mm});
            skLineSegment(sketch, "E1454", {"start": v(-34.27, -40.09) * mm, "end": v(-33.95, -40.32) * mm});
            skLineSegment(sketch, "E1455", {"start": v(-33.95, -40.32) * mm, "end": v(-33.64, -40.56) * mm});
            skLineSegment(sketch, "E1456", {"start": v(-33.64, -40.56) * mm, "end": v(-33.32, -40.8) * mm});
            skLineSegment(sketch, "E1457", {"start": v(-33.32, -40.8) * mm, "end": v(-33, -41.03) * mm});
            skLineSegment(sketch, "E1458", {"start": v(-33, -41.03) * mm, "end": v(-32.7, -41.27) * mm});
            skLineSegment(sketch, "E1459", {"start": v(-32.7, -41.27) * mm, "end": v(-32.38, -41.5) * mm});
            skLineSegment(sketch, "E1460", {"start": v(-32.38, -41.5) * mm, "end": v(-32.06, -41.74) * mm});
            skLineSegment(sketch, "E1461", {"start": v(-32.06, -41.74) * mm, "end": v(-31.75, -41.98) * mm});
            skLineSegment(sketch, "E1462", {"start": v(-31.75, -41.98) * mm, "end": v(-31.43, -42.21) * mm});
            skLineSegment(sketch, "E1463", {"start": v(-31.43, -42.21) * mm, "end": v(-31.12, -42.45) * mm});
            skLineSegment(sketch, "E1464", {"start": v(-31.12, -42.45) * mm, "end": v(-31.04, -42.5) * mm});
            skLineSegment(sketch, "E1465", {"start": v(-31.04, -42.5) * mm, "end": v(-31.27, -42.83) * mm});
            skLineSegment(sketch, "E1466", {"start": v(-31.27, -42.83) * mm, "end": v(-31.49, -43.15) * mm});
            skLineSegment(sketch, "E1467", {"start": v(-31.49, -43.15) * mm, "end": v(-31.71, -43.48) * mm});
            skLineSegment(sketch, "E1468", {"start": v(-31.71, -43.48) * mm, "end": v(-31.94, -43.8) * mm});
            skLineSegment(sketch, "E1469", {"start": v(-31.94, -43.8) * mm, "end": v(-32.16, -44.13) * mm});
            skLineSegment(sketch, "E1470", {"start": v(-32.16, -44.13) * mm, "end": v(-32.38, -44.46) * mm});
            skLineSegment(sketch, "E1471", {"start": v(-32.38, -44.46) * mm, "end": v(-32.6, -44.79) * mm});
            skLineSegment(sketch, "E1472", {"start": v(-32.6, -44.79) * mm, "end": v(-32.83, -45.11) * mm});
            skLineSegment(sketch, "E1473", {"start": v(-32.83, -45.11) * mm, "end": v(-33.05, -45.44) * mm});
            skLineSegment(sketch, "E1474", {"start": v(-33.05, -45.44) * mm, "end": v(-33.27, -45.77) * mm});
            skLineSegment(sketch, "E1475", {"start": v(-33.27, -45.77) * mm, "end": v(-33.5, -46.1) * mm});
            skLineSegment(sketch, "E1476", {"start": v(-33.5, -46.1) * mm, "end": v(-33.72, -46.42) * mm});
            skLineSegment(sketch, "E1477", {"start": v(-33.72, -46.42) * mm, "end": v(-33.96, -46.77) * mm});
            skLineSegment(sketch, "E1478", {"start": v(-33.96, -46.77) * mm, "end": v(-34.12, -47.16) * mm});
            skLineSegment(sketch, "E1479", {"start": v(-34.12, -47.16) * mm, "end": v(-34.18, -47.58) * mm});
            skLineSegment(sketch, "E1480", {"start": v(-34.18, -47.58) * mm, "end": v(-34.13, -48) * mm});
            skLineSegment(sketch, "E1481", {"start": v(-34.13, -48) * mm, "end": v(-33.97, -48.4) * mm});
            skLineSegment(sketch, "E1482", {"start": v(-33.97, -48.4) * mm, "end": v(-33.7, -48.73) * mm});
            skLineSegment(sketch, "E1483", {"start": v(-33.7, -48.73) * mm, "end": v(-33.44, -48.94) * mm});
            skLineSegment(sketch, "E1484", {"start": v(-33.44, -48.94) * mm, "end": v(-33.06, -49.12) * mm});
            skLineSegment(sketch, "E1485", {"start": v(-33.06, -49.12) * mm, "end": v(-32.64, -49.2) * mm});
            skLineSegment(sketch, "E1486", {"start": v(-32.64, -49.2) * mm, "end": v(-32.22, -49.16) * mm});
            skLineSegment(sketch, "E1487", {"start": v(-32.22, -49.16) * mm, "end": v(-31.82, -49.01) * mm});
            skLineSegment(sketch, "E1488", {"start": v(-31.82, -49.01) * mm, "end": v(-31.48, -48.77) * mm});
            skLineSegment(sketch, "E1489", {"start": v(-31.48, -48.77) * mm, "end": v(-31.2, -48.44) * mm});
            skLineSegment(sketch, "E1490", {"start": v(-31.2, -48.44) * mm, "end": v(-31, -48.1) * mm});
            skLineSegment(sketch, "E1491", {"start": v(-31, -48.1) * mm, "end": v(-30.8, -47.77) * mm});
            skLineSegment(sketch, "E1492", {"start": v(-30.8, -47.77) * mm, "end": v(-30.6, -47.42) * mm});
            skLineSegment(sketch, "E1493", {"start": v(-30.6, -47.42) * mm, "end": v(-30.4, -47.09) * mm});
            skLineSegment(sketch, "E1494", {"start": v(-30.4, -47.09) * mm, "end": v(-30.19, -46.75) * mm});
            skLineSegment(sketch, "E1495", {"start": v(-30.19, -46.75) * mm, "end": v(-29.98, -46.4) * mm});
            skLineSegment(sketch, "E1496", {"start": v(-29.98, -46.4) * mm, "end": v(-29.78, -46.07) * mm});
            skLineSegment(sketch, "E1497", {"start": v(-29.78, -46.07) * mm, "end": v(-29.58, -45.73) * mm});
            skLineSegment(sketch, "E1498", {"start": v(-29.58, -45.73) * mm, "end": v(-29.37, -45.4) * mm});
            skLineSegment(sketch, "E1499", {"start": v(-29.37, -45.4) * mm, "end": v(-29.17, -45.05) * mm});
            skLineSegment(sketch, "E1500", {"start": v(-29.17, -45.05) * mm, "end": v(-28.96, -44.72) * mm});
            skLineSegment(sketch, "E1501", {"start": v(-28.96, -44.72) * mm, "end": v(-28.76, -44.38) * mm});
            skLineSegment(sketch, "E1502", {"start": v(-28.76, -44.38) * mm, "end": v(-28.58, -44.08) * mm});
            skLineSegment(sketch, "E1503", {"start": v(-28.58, -44.08) * mm, "end": v(-28.24, -44.27) * mm});
            skLineSegment(sketch, "E1504", {"start": v(-28.24, -44.27) * mm, "end": v(-27.9, -44.46) * mm});
            skLineSegment(sketch, "E1505", {"start": v(-27.9, -44.46) * mm, "end": v(-27.55, -44.65) * mm});
            skLineSegment(sketch, "E1506", {"start": v(-27.55, -44.65) * mm, "end": v(-27.2, -44.84) * mm});
            skLineSegment(sketch, "E1507", {"start": v(-27.2, -44.84) * mm, "end": v(-26.85, -45.03) * mm});
            skLineSegment(sketch, "E1508", {"start": v(-26.85, -45.03) * mm, "end": v(-26.5, -45.22) * mm});
            skLineSegment(sketch, "E1509", {"start": v(-26.5, -45.22) * mm, "end": v(-26.16, -45.4) * mm});
            skLineSegment(sketch, "E1510", {"start": v(-26.16, -45.4) * mm, "end": v(-25.82, -45.6) * mm});
            skLineSegment(sketch, "E1511", {"start": v(-25.82, -45.6) * mm, "end": v(-25.47, -45.78) * mm});
            skLineSegment(sketch, "E1512", {"start": v(-25.47, -45.78) * mm, "end": v(-25.13, -45.97) * mm});
            skLineSegment(sketch, "E1513", {"start": v(-25.13, -45.97) * mm, "end": v(-24.78, -46.16) * mm});
            skLineSegment(sketch, "E1514", {"start": v(-24.78, -46.16) * mm, "end": v(-24.7, -46.2) * mm});
            skLineSegment(sketch, "E1515", {"start": v(-24.7, -46.2) * mm, "end": v(-24.87, -46.56) * mm});
            skLineSegment(sketch, "E1516", {"start": v(-24.87, -46.56) * mm, "end": v(-25.05, -46.91) * mm});
            skLineSegment(sketch, "E1517", {"start": v(-25.05, -46.91) * mm, "end": v(-25.22, -47.27) * mm});
            skLineSegment(sketch, "E1518", {"start": v(-25.22, -47.27) * mm, "end": v(-25.4, -47.62) * mm});
            skLineSegment(sketch, "E1519", {"start": v(-25.4, -47.62) * mm, "end": v(-25.57, -47.98) * mm});
            skLineSegment(sketch, "E1520", {"start": v(-25.57, -47.98) * mm, "end": v(-25.75, -48.33) * mm});
            skLineSegment(sketch, "E1521", {"start": v(-25.75, -48.33) * mm, "end": v(-25.92, -48.69) * mm});
            skLineSegment(sketch, "E1522", {"start": v(-25.92, -48.69) * mm, "end": v(-26.1, -49.04) * mm});
            skLineSegment(sketch, "E1523", {"start": v(-26.1, -49.04) * mm, "end": v(-26.27, -49.4) * mm});
            skLineSegment(sketch, "E1524", {"start": v(-26.27, -49.4) * mm, "end": v(-26.44, -49.75) * mm});
            skLineSegment(sketch, "E1525", {"start": v(-26.44, -49.75) * mm, "end": v(-26.62, -50.1) * mm});
            skLineSegment(sketch, "E1526", {"start": v(-26.62, -50.1) * mm, "end": v(-26.8, -50.46) * mm});
            skLineSegment(sketch, "E1527", {"start": v(-26.8, -50.46) * mm, "end": v(-26.98, -50.85) * mm});
            skLineSegment(sketch, "E1528", {"start": v(-26.98, -50.85) * mm, "end": v(-27.08, -51.26) * mm});
            skLineSegment(sketch, "E1529", {"start": v(-27.08, -51.26) * mm, "end": v(-27.08, -51.68) * mm});
            skLineSegment(sketch, "E1530", {"start": v(-27.08, -51.68) * mm, "end": v(-26.97, -52.09) * mm});
            skLineSegment(sketch, "E1531", {"start": v(-26.97, -52.09) * mm, "end": v(-26.75, -52.45) * mm});
            skLineSegment(sketch, "E1532", {"start": v(-26.75, -52.45) * mm, "end": v(-26.45, -52.75) * mm});
            skLineSegment(sketch, "E1533", {"start": v(-26.45, -52.75) * mm, "end": v(-26.16, -52.92) * mm});
            skLineSegment(sketch, "E1534", {"start": v(-26.16, -52.92) * mm, "end": v(-25.75, -53.04) * mm});
            skLineSegment(sketch, "E1535", {"start": v(-25.75, -53.04) * mm, "end": v(-25.33, -53.06) * mm});
            skLineSegment(sketch, "E1536", {"start": v(-25.33, -53.06) * mm, "end": v(-24.92, -52.96) * mm});
            skLineSegment(sketch, "E1537", {"start": v(-24.92, -52.96) * mm, "end": v(-24.54, -52.76) * mm});
            skLineSegment(sketch, "E1538", {"start": v(-24.54, -52.76) * mm, "end": v(-24.24, -52.47) * mm});
            skLineSegment(sketch, "E1539", {"start": v(-24.24, -52.47) * mm, "end": v(-24.02, -52.1) * mm});
            skLineSegment(sketch, "E1540", {"start": v(-24.02, -52.1) * mm, "end": v(-23.86, -51.74) * mm});
            skLineSegment(sketch, "E1541", {"start": v(-23.86, -51.74) * mm, "end": v(-23.71, -51.38) * mm});
            skLineSegment(sketch, "E1542", {"start": v(-23.71, -51.38) * mm, "end": v(-23.56, -51.01) * mm});
            skLineSegment(sketch, "E1543", {"start": v(-23.56, -51.01) * mm, "end": v(-23.4, -50.65) * mm});
            skLineSegment(sketch, "E1544", {"start": v(-23.4, -50.65) * mm, "end": v(-23.25, -50.29) * mm});
            skLineSegment(sketch, "E1545", {"start": v(-23.25, -50.29) * mm, "end": v(-23.1, -49.92) * mm});
            skLineSegment(sketch, "E1546", {"start": v(-23.1, -49.92) * mm, "end": v(-22.94, -49.56) * mm});
            skLineSegment(sketch, "E1547", {"start": v(-22.94, -49.56) * mm, "end": v(-22.79, -49.2) * mm});
            skLineSegment(sketch, "E1548", {"start": v(-22.79, -49.2) * mm, "end": v(-22.63, -48.83) * mm});
            skLineSegment(sketch, "E1549", {"start": v(-22.63, -48.83) * mm, "end": v(-22.48, -48.46) * mm});
            skLineSegment(sketch, "E1550", {"start": v(-22.48, -48.46) * mm, "end": v(-22.32, -48.1) * mm});
            skLineSegment(sketch, "E1551", {"start": v(-22.32, -48.1) * mm, "end": v(-22.17, -47.73) * mm});
            skLineSegment(sketch, "E1552", {"start": v(-22.17, -47.73) * mm, "end": v(-22.04, -47.42) * mm});
            skLineSegment(sketch, "E1553", {"start": v(-22.04, -47.42) * mm, "end": v(-21.67, -47.56) * mm});
            skLineSegment(sketch, "E1554", {"start": v(-21.67, -47.56) * mm, "end": v(-21.3, -47.7) * mm});
            skLineSegment(sketch, "E1555", {"start": v(-21.3, -47.7) * mm, "end": v(-20.93, -47.83) * mm});
            skLineSegment(sketch, "E1556", {"start": v(-20.93, -47.83) * mm, "end": v(-20.56, -47.97) * mm});
            skLineSegment(sketch, "E1557", {"start": v(-20.56, -47.97) * mm, "end": v(-20.2, -48.1) * mm});
            skLineSegment(sketch, "E1558", {"start": v(-20.2, -48.1) * mm, "end": v(-19.82, -48.25) * mm});
            skLineSegment(sketch, "E1559", {"start": v(-19.82, -48.25) * mm, "end": v(-19.45, -48.38) * mm});
            skLineSegment(sketch, "E1560", {"start": v(-19.45, -48.38) * mm, "end": v(-19.09, -48.52) * mm});
            skLineSegment(sketch, "E1561", {"start": v(-19.09, -48.52) * mm, "end": v(-18.72, -48.66) * mm});
            skLineSegment(sketch, "E1562", {"start": v(-18.72, -48.66) * mm, "end": v(-18.35, -48.8) * mm});
            skLineSegment(sketch, "E1563", {"start": v(-18.35, -48.8) * mm, "end": v(-17.98, -48.93) * mm});
            skLineSegment(sketch, "E1564", {"start": v(-17.98, -48.93) * mm, "end": v(-17.9, -48.97) * mm});
            skLineSegment(sketch, "E1565", {"start": v(-17.9, -48.97) * mm, "end": v(-18.01, -49.34) * mm});
            skLineSegment(sketch, "E1566", {"start": v(-18.01, -49.34) * mm, "end": v(-18.14, -49.72) * mm});
            skLineSegment(sketch, "E1567", {"start": v(-18.14, -49.72) * mm, "end": v(-18.26, -50.1) * mm});
            skLineSegment(sketch, "E1568", {"start": v(-18.26, -50.1) * mm, "end": v(-18.38, -50.47) * mm});
            skLineSegment(sketch, "E1569", {"start": v(-18.38, -50.47) * mm, "end": v(-18.5, -50.84) * mm});
            skLineSegment(sketch, "E1570", {"start": v(-18.5, -50.84) * mm, "end": v(-18.63, -51.22) * mm});
            skLineSegment(sketch, "E1571", {"start": v(-18.63, -51.22) * mm, "end": v(-18.75, -51.6) * mm});
            skLineSegment(sketch, "E1572", {"start": v(-18.75, -51.6) * mm, "end": v(-18.87, -51.97) * mm});
            skLineSegment(sketch, "E1573", {"start": v(-18.87, -51.97) * mm, "end": v(-19, -52.35) * mm});
            skLineSegment(sketch, "E1574", {"start": v(-19, -52.35) * mm, "end": v(-19.11, -52.73) * mm});
            skLineSegment(sketch, "E1575", {"start": v(-19.11, -52.73) * mm, "end": v(-19.24, -53.1) * mm});
            skLineSegment(sketch, "E1576", {"start": v(-19.24, -53.1) * mm, "end": v(-19.36, -53.48) * mm});
            skLineSegment(sketch, "E1577", {"start": v(-19.36, -53.48) * mm, "end": v(-19.49, -53.89) * mm});
            skLineSegment(sketch, "E1578", {"start": v(-19.49, -53.89) * mm, "end": v(-19.53, -54.3) * mm});
            skLineSegment(sketch, "E1579", {"start": v(-19.53, -54.3) * mm, "end": v(-19.47, -54.72) * mm});
            skLineSegment(sketch, "E1580", {"start": v(-19.47, -54.72) * mm, "end": v(-19.3, -55.11) * mm});
            skLineSegment(sketch, "E1581", {"start": v(-19.3, -55.11) * mm, "end": v(-19.04, -55.44) * mm});
            skLineSegment(sketch, "E1582", {"start": v(-19.04, -55.44) * mm, "end": v(-18.7, -55.7) * mm});
            skLineSegment(sketch, "E1583", {"start": v(-18.7, -55.7) * mm, "end": v(-18.38, -55.82) * mm});
            skLineSegment(sketch, "E1584", {"start": v(-18.38, -55.82) * mm, "end": v(-17.96, -55.89) * mm});
            skLineSegment(sketch, "E1585", {"start": v(-17.96, -55.89) * mm, "end": v(-17.54, -55.84) * mm});
            skLineSegment(sketch, "E1586", {"start": v(-17.54, -55.84) * mm, "end": v(-17.15, -55.68) * mm});
            skLineSegment(sketch, "E1587", {"start": v(-17.15, -55.68) * mm, "end": v(-16.8, -55.43) * mm});
            skLineSegment(sketch, "E1588", {"start": v(-16.8, -55.43) * mm, "end": v(-16.54, -55.1) * mm});
            skLineSegment(sketch, "E1589", {"start": v(-16.54, -55.1) * mm, "end": v(-16.38, -54.7) * mm});
            skLineSegment(sketch, "E1590", {"start": v(-16.38, -54.7) * mm, "end": v(-16.28, -54.33) * mm});
            skLineSegment(sketch, "E1591", {"start": v(-16.28, -54.33) * mm, "end": v(-16.18, -53.95) * mm});
            skLineSegment(sketch, "E1592", {"start": v(-16.18, -53.95) * mm, "end": v(-16.08, -53.56) * mm});
            skLineSegment(sketch, "E1593", {"start": v(-16.08, -53.56) * mm, "end": v(-15.98, -53.18) * mm});
            skLineSegment(sketch, "E1594", {"start": v(-15.98, -53.18) * mm, "end": v(-15.88, -52.8) * mm});
            skLineSegment(sketch, "E1595", {"start": v(-15.88, -52.8) * mm, "end": v(-15.77, -52.41) * mm});
            skLineSegment(sketch, "E1596", {"start": v(-15.77, -52.41) * mm, "end": v(-15.67, -52.03) * mm});
            skLineSegment(sketch, "E1597", {"start": v(-15.67, -52.03) * mm, "end": v(-15.57, -51.65) * mm});
            skLineSegment(sketch, "E1598", {"start": v(-15.57, -51.65) * mm, "end": v(-15.47, -51.27) * mm});
            skLineSegment(sketch, "E1599", {"start": v(-15.47, -51.27) * mm, "end": v(-15.37, -50.89) * mm});
            skLineSegment(sketch, "E1600", {"start": v(-15.37, -50.89) * mm, "end": v(-15.27, -50.5) * mm});
            skLineSegment(sketch, "E1601", {"start": v(-15.27, -50.5) * mm, "end": v(-15.17, -50.12) * mm});
            skLineSegment(sketch, "E1602", {"start": v(-15.17, -50.12) * mm, "end": v(-15.08, -49.8) * mm});
            skLineSegment(sketch, "E1603", {"start": v(-15.08, -49.8) * mm, "end": v(-14.7, -49.87) * mm});
            skLineSegment(sketch, "E1604", {"start": v(-14.7, -49.87) * mm, "end": v(-14.32, -49.96) * mm});
            skLineSegment(sketch, "E1605", {"start": v(-14.32, -49.96) * mm, "end": v(-13.93, -50.04) * mm});
            skLineSegment(sketch, "E1606", {"start": v(-13.93, -50.04) * mm, "end": v(-13.55, -50.13) * mm});
            skLineSegment(sketch, "E1607", {"start": v(-13.55, -50.13) * mm, "end": v(-13.16, -50.2) * mm});
            skLineSegment(sketch, "E1608", {"start": v(-13.16, -50.2) * mm, "end": v(-12.78, -50.3) * mm});
            skLineSegment(sketch, "E1609", {"start": v(-12.78, -50.3) * mm, "end": v(-12.4, -50.38) * mm});
            skLineSegment(sketch, "E1610", {"start": v(-12.4, -50.38) * mm, "end": v(-12, -50.46) * mm});
            skLineSegment(sketch, "E1611", {"start": v(-12, -50.46) * mm, "end": v(-11.62, -50.54) * mm});
            skLineSegment(sketch, "E1612", {"start": v(-11.62, -50.54) * mm, "end": v(-11.24, -50.63) * mm});
            skLineSegment(sketch, "E1613", {"start": v(-11.24, -50.63) * mm, "end": v(-10.85, -50.71) * mm});
            skLineSegment(sketch, "E1614", {"start": v(-10.85, -50.71) * mm, "end": v(-10.76, -50.73) * mm});
            skLineSegment(sketch, "E1615", {"start": v(-10.76, -50.73) * mm, "end": v(-10.83, -51.12) * mm});
            skLineSegment(sketch, "E1616", {"start": v(-10.83, -51.12) * mm, "end": v(-10.9, -51.5) * mm});
            skLineSegment(sketch, "E1617", {"start": v(-10.9, -51.5) * mm, "end": v(-10.96, -51.9) * mm});
            skLineSegment(sketch, "E1618", {"start": v(-10.96, -51.9) * mm, "end": v(-11.03, -52.29) * mm});
            skLineSegment(sketch, "E1619", {"start": v(-11.03, -52.29) * mm, "end": v(-11.1, -52.68) * mm});
            skLineSegment(sketch, "E1620", {"start": v(-11.1, -52.68) * mm, "end": v(-11.17, -53.07) * mm});
            skLineSegment(sketch, "E1621", {"start": v(-11.17, -53.07) * mm, "end": v(-11.23, -53.46) * mm});
            skLineSegment(sketch, "E1622", {"start": v(-11.23, -53.46) * mm, "end": v(-11.3, -53.85) * mm});
            skLineSegment(sketch, "E1623", {"start": v(-11.3, -53.85) * mm, "end": v(-11.37, -54.24) * mm});
            skLineSegment(sketch, "E1624", {"start": v(-11.37, -54.24) * mm, "end": v(-11.44, -54.63) * mm});
            skLineSegment(sketch, "E1625", {"start": v(-11.44, -54.63) * mm, "end": v(-11.5, -55.02) * mm});
            skLineSegment(sketch, "E1626", {"start": v(-11.5, -55.02) * mm, "end": v(-11.57, -55.4) * mm});
            skLineSegment(sketch, "E1627", {"start": v(-11.57, -55.4) * mm, "end": v(-11.64, -55.83) * mm});
            skLineSegment(sketch, "E1628", {"start": v(-11.64, -55.83) * mm, "end": v(-11.63, -56.25) * mm});
            skLineSegment(sketch, "E1629", {"start": v(-11.63, -56.25) * mm, "end": v(-11.5, -56.66) * mm});
            skLineSegment(sketch, "E1630", {"start": v(-11.5, -56.66) * mm, "end": v(-11.28, -57.01) * mm});
            skLineSegment(sketch, "E1631", {"start": v(-11.28, -57.01) * mm, "end": v(-10.97, -57.3) * mm});
            skLineSegment(sketch, "E1632", {"start": v(-10.97, -57.3) * mm, "end": v(-10.6, -57.5) * mm});
            skLineSegment(sketch, "E1633", {"start": v(-10.6, -57.5) * mm, "end": v(-10.19, -57.6) * mm});
            skLineSegment(sketch, "E1634", {"start": v(-10.19, -57.6) * mm, "end": v(-9.76, -57.58) * mm});
            skLineSegment(sketch, "E1635", {"start": v(-9.76, -57.58) * mm, "end": v(-9.36, -57.45) * mm});
            skLineSegment(sketch, "E1636", {"start": v(-9.36, -57.45) * mm, "end": v(-9, -57.22) * mm});
            skLineSegment(sketch, "E1637", {"start": v(-9, -57.22) * mm, "end": v(-8.72, -56.9) * mm});
            skLineSegment(sketch, "E1638", {"start": v(-8.72, -56.9) * mm, "end": v(-8.52, -56.53) * mm});
            skLineSegment(sketch, "E1639", {"start": v(-8.52, -56.53) * mm, "end": v(-8.45, -56.2) * mm});
            skLineSegment(sketch, "E1640", {"start": v(-8.45, -56.2) * mm, "end": v(-8.4, -55.8) * mm});
            skLineSegment(sketch, "E1641", {"start": v(-8.4, -55.8) * mm, "end": v(-8.36, -55.42) * mm});
            skLineSegment(sketch, "E1642", {"start": v(-8.36, -55.42) * mm, "end": v(-8.31, -55.02) * mm});
            skLineSegment(sketch, "E1643", {"start": v(-8.31, -55.02) * mm, "end": v(-8.27, -54.63) * mm});
            skLineSegment(sketch, "E1644", {"start": v(-8.27, -54.63) * mm, "end": v(-8.22, -54.24) * mm});
            skLineSegment(sketch, "E1645", {"start": v(-8.22, -54.24) * mm, "end": v(-8.18, -53.84) * mm});
            skLineSegment(sketch, "E1646", {"start": v(-8.18, -53.84) * mm, "end": v(-8.13, -53.45) * mm});
            skLineSegment(sketch, "E1647", {"start": v(-8.13, -53.45) * mm, "end": v(-8.09, -53.06) * mm});
            skLineSegment(sketch, "E1648", {"start": v(-8.09, -53.06) * mm, "end": v(-8.04, -52.66) * mm});
            skLineSegment(sketch, "E1649", {"start": v(-8.04, -52.66) * mm, "end": v(-8, -52.27) * mm});
            skLineSegment(sketch, "E1650", {"start": v(-8, -52.27) * mm, "end": v(-7.95, -51.88) * mm});
            skLineSegment(sketch, "E1651", {"start": v(-7.95, -51.88) * mm, "end": v(-7.9, -51.48) * mm});
            skLineSegment(sketch, "E1652", {"start": v(-7.9, -51.48) * mm, "end": v(-7.87, -51.15) * mm});
            skLineSegment(sketch, "E1653", {"start": v(-7.87, -51.15) * mm, "end": v(-7.47, -51.18) * mm});
            skLineSegment(sketch, "E1654", {"start": v(-7.47, -51.18) * mm, "end": v(-7.08, -51.2) * mm});
            skLineSegment(sketch, "E1655", {"start": v(-7.08, -51.2) * mm, "end": v(-6.69, -51.23) * mm});
            skLineSegment(sketch, "E1656", {"start": v(-6.69, -51.23) * mm, "end": v(-6.3, -51.26) * mm});
            skLineSegment(sketch, "E1657", {"start": v(-6.3, -51.26) * mm, "end": v(-5.9, -51.29) * mm});
            skLineSegment(sketch, "E1658", {"start": v(-5.9, -51.29) * mm, "end": v(-5.5, -51.32) * mm});
            skLineSegment(sketch, "E1659", {"start": v(-5.5, -51.32) * mm, "end": v(-5.12, -51.34) * mm});
            skLineSegment(sketch, "E1660", {"start": v(-5.12, -51.34) * mm, "end": v(-4.72, -51.37) * mm});
            skLineSegment(sketch, "E1661", {"start": v(-4.72, -51.37) * mm, "end": v(-4.33, -51.4) * mm});
            skLineSegment(sketch, "E1662", {"start": v(-4.33, -51.4) * mm, "end": v(-3.94, -51.43) * mm});
            skLineSegment(sketch, "E1663", {"start": v(-3.94, -51.43) * mm, "end": v(-3.55, -51.46) * mm});
            skLineSegment(sketch, "E1664", {"start": v(-3.55, -51.46) * mm, "end": v(-3.45, -51.46) * mm});
            skLineSegment(sketch, "E1665", {"start": v(-3.45, -51.46) * mm, "end": v(-3.46, -51.86) * mm});
            skLineSegment(sketch, "E1666", {"start": v(-3.46, -51.86) * mm, "end": v(-3.48, -52.25) * mm});
            skLineSegment(sketch, "E1667", {"start": v(-3.48, -52.25) * mm, "end": v(-3.49, -52.65) * mm});
            skLineSegment(sketch, "E1668", {"start": v(-3.49, -52.65) * mm, "end": v(-3.5, -53.04) * mm});
            skLineSegment(sketch, "E1669", {"start": v(-3.5, -53.04) * mm, "end": v(-3.5, -53.44) * mm});
            skLineSegment(sketch, "E1670", {"start": v(-3.5, -53.44) * mm, "end": v(-3.52, -53.84) * mm});
            skLineSegment(sketch, "E1671", {"start": v(-3.52, -53.84) * mm, "end": v(-3.53, -54.23) * mm});
            skLineSegment(sketch, "E1672", {"start": v(-3.53, -54.23) * mm, "end": v(-3.54, -54.62) * mm});
            skLineSegment(sketch, "E1673", {"start": v(-3.54, -54.62) * mm, "end": v(-3.55, -55.02) * mm});
            skLineSegment(sketch, "E1674", {"start": v(-3.55, -55.02) * mm, "end": v(-3.57, -55.42) * mm});
            skLineSegment(sketch, "E1675", {"start": v(-3.57, -55.42) * mm, "end": v(-3.58, -55.8) * mm});
            skLineSegment(sketch, "E1676", {"start": v(-3.58, -55.8) * mm, "end": v(-3.59, -56.2) * mm});
            skLineSegment(sketch, "E1677", {"start": v(-3.59, -56.2) * mm, "end": v(-3.6, -56.63) * mm});
            skLineSegment(sketch, "E1678", {"start": v(-3.6, -56.63) * mm, "end": v(-3.52, -57.05) * mm});
            skLineSegment(sketch, "E1679", {"start": v(-3.52, -57.05) * mm, "end": v(-3.35, -57.43) * mm});
            skLineSegment(sketch, "E1680", {"start": v(-3.35, -57.43) * mm, "end": v(-3.07, -57.76) * mm});
            skLineSegment(sketch, "E1681", {"start": v(-3.07, -57.76) * mm, "end": v(-2.73, -58) * mm});
            skLineSegment(sketch, "E1682", {"start": v(-2.73, -58) * mm, "end": v(-2.33, -58.14) * mm});
            skLineSegment(sketch, "E1683", {"start": v(-2.33, -58.14) * mm, "end": v(-1.9, -58.17) * mm});
            skLineSegment(sketch, "E1684", {"start": v(-1.9, -58.17) * mm, "end": v(-1.49, -58.1) * mm});
            skLineSegment(sketch, "E1685", {"start": v(-1.49, -58.1) * mm, "end": v(-1.1, -57.91) * mm});
            skLineSegment(sketch, "E1686", {"start": v(-1.1, -57.91) * mm, "end": v(-0.79, -57.64) * mm});
            skLineSegment(sketch, "E1687", {"start": v(-0.79, -57.64) * mm, "end": v(-0.55, -57.29) * mm});
            skLineSegment(sketch, "E1688", {"start": v(-0.55, -57.29) * mm, "end": v(-0.41, -56.88) * mm});
            skLineSegment(sketch, "E1689", {"start": v(-0.41, -56.88) * mm, "end": v(-0.38, -56.55) * mm});
            skLineSegment(sketch, "E1690", {"start": v(-0.38, -56.55) * mm, "end": v(-0.4, -56.15) * mm});
            skLineSegment(sketch, "E1691", {"start": v(-0.4, -56.15) * mm, "end": v(-0.4, -55.76) * mm});
            skLineSegment(sketch, "E1692", {"start": v(-0.4, -55.76) * mm, "end": v(-0.42, -55.36) * mm});
            skLineSegment(sketch, "E1693", {"start": v(-0.42, -55.36) * mm, "end": v(-0.43, -54.97) * mm});
            skLineSegment(sketch, "E1694", {"start": v(-0.43, -54.97) * mm, "end": v(-0.44, -54.57) * mm});
            skLineSegment(sketch, "E1695", {"start": v(-0.44, -54.57) * mm, "end": v(-0.45, -54.17) * mm});
            skLineSegment(sketch, "E1696", {"start": v(-0.45, -54.17) * mm, "end": v(-0.46, -53.78) * mm});
            skLineSegment(sketch, "E1697", {"start": v(-0.46, -53.78) * mm, "end": v(-0.47, -53.39) * mm});
            skLineSegment(sketch, "E1698", {"start": v(-0.47, -53.39) * mm, "end": v(-0.48, -52.99) * mm});
            skLineSegment(sketch, "E1699", {"start": v(-0.48, -52.99) * mm, "end": v(-0.5, -52.6) * mm});
            skLineSegment(sketch, "E1700", {"start": v(-0.5, -52.6) * mm, "end": v(-0.5, -52.2) * mm});
            skLineSegment(sketch, "E1701", {"start": v(-0.5, -52.2) * mm, "end": v(-0.52, -51.8) * mm});
            skLineSegment(sketch, "E1702", {"start": v(-0.52, -51.8) * mm, "end": v(-0.53, -51.46) * mm});
            skLineSegment(sketch, "E1703", {"start": v(-0.53, -51.46) * mm, "end": v(-0.13, -51.44) * mm});
            skLineSegment(sketch, "E1704", {"start": v(-0.13, -51.44) * mm, "end": v(0.26, -51.4) * mm});
            skLineSegment(sketch, "E1705", {"start": v(0.26, -51.4) * mm, "end": v(0.65, -51.38) * mm});
            skLineSegment(sketch, "E1706", {"start": v(0.65, -51.38) * mm, "end": v(1.04, -51.35) * mm});
            skLineSegment(sketch, "E1707", {"start": v(1.04, -51.35) * mm, "end": v(1.44, -51.32) * mm});
            skLineSegment(sketch, "E1708", {"start": v(1.44, -51.32) * mm, "end": v(1.83, -51.3) * mm});
            skLineSegment(sketch, "E1709", {"start": v(1.83, -51.3) * mm, "end": v(2.22, -51.27) * mm});
            skLineSegment(sketch, "E1710", {"start": v(2.22, -51.27) * mm, "end": v(2.62, -51.24) * mm});
            skLineSegment(sketch, "E1711", {"start": v(2.62, -51.24) * mm, "end": v(3, -51.21) * mm});
            skLineSegment(sketch, "E1712", {"start": v(3, -51.21) * mm, "end": v(3.4, -51.18) * mm});
            skLineSegment(sketch, "E1713", {"start": v(3.4, -51.18) * mm, "end": v(3.8, -51.15) * mm});
            skLineSegment(sketch, "E1714", {"start": v(3.8, -51.15) * mm, "end": v(3.89, -51.15) * mm});
            skLineSegment(sketch, "E1715", {"start": v(3.89, -51.15) * mm, "end": v(3.93, -51.54) * mm});
            skLineSegment(sketch, "E1716", {"start": v(3.93, -51.54) * mm, "end": v(3.98, -51.93) * mm});
            skLineSegment(sketch, "E1717", {"start": v(3.98, -51.93) * mm, "end": v(4.02, -52.33) * mm});
            skLineSegment(sketch, "E1718", {"start": v(4.02, -52.33) * mm, "end": v(4.07, -52.72) * mm});
            skLineSegment(sketch, "E1719", {"start": v(4.07, -52.72) * mm, "end": v(4.11, -53.1) * mm});
            skLineSegment(sketch, "E1720", {"start": v(4.11, -53.1) * mm, "end": v(4.16, -53.5) * mm});
            skLineSegment(sketch, "E1721", {"start": v(4.16, -53.5) * mm, "end": v(4.2, -53.9) * mm});
            skLineSegment(sketch, "E1722", {"start": v(4.2, -53.9) * mm, "end": v(4.25, -54.29) * mm});
            skLineSegment(sketch, "E1723", {"start": v(4.25, -54.29) * mm, "end": v(4.3, -54.68) * mm});
            skLineSegment(sketch, "E1724", {"start": v(4.3, -54.68) * mm, "end": v(4.34, -55.08) * mm});
            skLineSegment(sketch, "E1725", {"start": v(4.34, -55.08) * mm, "end": v(4.38, -55.47) * mm});
            skLineSegment(sketch, "E1726", {"start": v(4.38, -55.47) * mm, "end": v(4.43, -55.86) * mm});
            skLineSegment(sketch, "E1727", {"start": v(4.43, -55.86) * mm, "end": v(4.48, -56.28) * mm});
            skLineSegment(sketch, "E1728", {"start": v(4.48, -56.28) * mm, "end": v(4.6, -56.69) * mm});
            skLineSegment(sketch, "E1729", {"start": v(4.6, -56.69) * mm, "end": v(4.84, -57.04) * mm});
            skLineSegment(sketch, "E1730", {"start": v(4.84, -57.04) * mm, "end": v(5.16, -57.32) * mm});
            skLineSegment(sketch, "E1731", {"start": v(5.16, -57.32) * mm, "end": v(5.54, -57.51) * mm});
            skLineSegment(sketch, "E1732", {"start": v(5.54, -57.51) * mm, "end": v(5.95, -57.6) * mm});
            skLineSegment(sketch, "E1733", {"start": v(5.95, -57.6) * mm, "end": v(6.37, -57.57) * mm});
            skLineSegment(sketch, "E1734", {"start": v(6.37, -57.57) * mm, "end": v(6.77, -57.43) * mm});
            skLineSegment(sketch, "E1735", {"start": v(6.77, -57.43) * mm, "end": v(7.13, -57.2) * mm});
            skLineSegment(sketch, "E1736", {"start": v(7.13, -57.2) * mm, "end": v(7.4, -56.88) * mm});
            skLineSegment(sketch, "E1737", {"start": v(7.4, -56.88) * mm, "end": v(7.59, -56.5) * mm});
            skLineSegment(sketch, "E1738", {"start": v(7.59, -56.5) * mm, "end": v(7.67, -56.08) * mm});
            skLineSegment(sketch, "E1739", {"start": v(7.67, -56.08) * mm, "end": v(7.65, -55.74) * mm});
            skLineSegment(sketch, "E1740", {"start": v(7.65, -55.74) * mm, "end": v(7.58, -55.35) * mm});
            skLineSegment(sketch, "E1741", {"start": v(7.58, -55.35) * mm, "end": v(7.51, -54.97) * mm});
            skLineSegment(sketch, "E1742", {"start": v(7.51, -54.97) * mm, "end": v(7.45, -54.57) * mm});
            skLineSegment(sketch, "E1743", {"start": v(7.45, -54.57) * mm, "end": v(7.38, -54.19) * mm});
            skLineSegment(sketch, "E1744", {"start": v(7.38, -54.19) * mm, "end": v(7.31, -53.8) * mm});
            skLineSegment(sketch, "E1745", {"start": v(7.31, -53.8) * mm, "end": v(7.24, -53.4) * mm});
            skLineSegment(sketch, "E1746", {"start": v(7.24, -53.4) * mm, "end": v(7.18, -53.02) * mm});
            skLineSegment(sketch, "E1747", {"start": v(7.18, -53.02) * mm, "end": v(7.1, -52.63) * mm});
            skLineSegment(sketch, "E1748", {"start": v(7.1, -52.63) * mm, "end": v(7.04, -52.23) * mm});
            skLineSegment(sketch, "E1749", {"start": v(7.04, -52.23) * mm, "end": v(6.97, -51.85) * mm});
            skLineSegment(sketch, "E1750", {"start": v(6.97, -51.85) * mm, "end": v(6.9, -51.46) * mm});
            skLineSegment(sketch, "E1751", {"start": v(6.9, -51.46) * mm, "end": v(6.84, -51.07) * mm});
            skLineSegment(sketch, "E1752", {"start": v(6.84, -51.07) * mm, "end": v(6.78, -50.73) * mm});
            skLineSegment(sketch, "E1753", {"start": v(6.78, -50.73) * mm, "end": v(7.17, -50.65) * mm});
            skLineSegment(sketch, "E1754", {"start": v(7.17, -50.65) * mm, "end": v(7.55, -50.56) * mm});
            skLineSegment(sketch, "E1755", {"start": v(7.55, -50.56) * mm, "end": v(7.94, -50.48) * mm});
            skLineSegment(sketch, "E1756", {"start": v(7.94, -50.48) * mm, "end": v(8.32, -50.4) * mm});
            skLineSegment(sketch, "E1757", {"start": v(8.32, -50.4) * mm, "end": v(8.7, -50.31) * mm});
            skLineSegment(sketch, "E1758", {"start": v(8.7, -50.31) * mm, "end": v(9.1, -50.23) * mm});
            skLineSegment(sketch, "E1759", {"start": v(9.1, -50.23) * mm, "end": v(9.48, -50.15) * mm});
            skLineSegment(sketch, "E1760", {"start": v(9.48, -50.15) * mm, "end": v(9.86, -50.06) * mm});
            skLineSegment(sketch, "E1761", {"start": v(9.86, -50.06) * mm, "end": v(10.25, -49.98) * mm});
            skLineSegment(sketch, "E1762", {"start": v(10.25, -49.98) * mm, "end": v(10.63, -49.9) * mm});
            skLineSegment(sketch, "E1763", {"start": v(10.63, -49.9) * mm, "end": v(11.01, -49.81) * mm});
            skLineSegment(sketch, "E1764", {"start": v(11.01, -49.81) * mm, "end": v(11.1, -49.8) * mm});
            skLineSegment(sketch, "E1765", {"start": v(11.1, -49.8) * mm, "end": v(11.2, -50.17) * mm});
            skLineSegment(sketch, "E1766", {"start": v(11.2, -50.17) * mm, "end": v(11.3, -50.55) * mm});
            skLineSegment(sketch, "E1767", {"start": v(11.3, -50.55) * mm, "end": v(11.4, -50.94) * mm});
            skLineSegment(sketch, "E1768", {"start": v(11.4, -50.94) * mm, "end": v(11.5, -51.32) * mm});
            skLineSegment(sketch, "E1769", {"start": v(11.5, -51.32) * mm, "end": v(11.6, -51.7) * mm});
            skLineSegment(sketch, "E1770", {"start": v(11.6, -51.7) * mm, "end": v(11.7, -52.09) * mm});
            skLineSegment(sketch, "E1771", {"start": v(11.7, -52.09) * mm, "end": v(11.8, -52.47) * mm});
            skLineSegment(sketch, "E1772", {"start": v(11.8, -52.47) * mm, "end": v(11.9, -52.85) * mm});
            skLineSegment(sketch, "E1773", {"start": v(11.9, -52.85) * mm, "end": v(12, -53.23) * mm});
            skLineSegment(sketch, "E1774", {"start": v(12, -53.23) * mm, "end": v(12.11, -53.61) * mm});
            skLineSegment(sketch, "E1775", {"start": v(12.11, -53.61) * mm, "end": v(12.21, -54) * mm});
            skLineSegment(sketch, "E1776", {"start": v(12.21, -54) * mm, "end": v(12.31, -54.38) * mm});
            skLineSegment(sketch, "E1777", {"start": v(12.31, -54.38) * mm, "end": v(12.42, -54.8) * mm});
            skLineSegment(sketch, "E1778", {"start": v(12.42, -54.8) * mm, "end": v(12.6, -55.17) * mm});
            skLineSegment(sketch, "E1779", {"start": v(12.6, -55.17) * mm, "end": v(12.89, -55.49) * mm});
            skLineSegment(sketch, "E1780", {"start": v(12.89, -55.49) * mm, "end": v(13.24, -55.72) * mm});
            skLineSegment(sketch, "E1781", {"start": v(13.24, -55.72) * mm, "end": v(13.64, -55.86) * mm});
            skLineSegment(sketch, "E1782", {"start": v(13.64, -55.86) * mm, "end": v(14.07, -55.88) * mm});
            skLineSegment(sketch, "E1783", {"start": v(14.07, -55.88) * mm, "end": v(14.48, -55.8) * mm});
            skLineSegment(sketch, "E1784", {"start": v(14.48, -55.8) * mm, "end": v(14.86, -55.6) * mm});
            skLineSegment(sketch, "E1785", {"start": v(14.86, -55.6) * mm, "end": v(15.17, -55.32) * mm});
            skLineSegment(sketch, "E1786", {"start": v(15.17, -55.32) * mm, "end": v(15.4, -54.96) * mm});
            skLineSegment(sketch, "E1787", {"start": v(15.4, -54.96) * mm, "end": v(15.53, -54.56) * mm});
            skLineSegment(sketch, "E1788", {"start": v(15.53, -54.56) * mm, "end": v(15.55, -54.14) * mm});
            skLineSegment(sketch, "E1789", {"start": v(15.55, -54.14) * mm, "end": v(15.48, -53.8) * mm});
            skLineSegment(sketch, "E1790", {"start": v(15.48, -53.8) * mm, "end": v(15.36, -53.43) * mm});
            skLineSegment(sketch, "E1791", {"start": v(15.36, -53.43) * mm, "end": v(15.24, -53.05) * mm});
            skLineSegment(sketch, "E1792", {"start": v(15.24, -53.05) * mm, "end": v(15.12, -52.67) * mm});
            skLineSegment(sketch, "E1793", {"start": v(15.12, -52.67) * mm, "end": v(15, -52.3) * mm});
            skLineSegment(sketch, "E1794", {"start": v(15, -52.3) * mm, "end": v(14.87, -51.93) * mm});
            skLineSegment(sketch, "E1795", {"start": v(14.87, -51.93) * mm, "end": v(14.75, -51.55) * mm});
            skLineSegment(sketch, "E1796", {"start": v(14.75, -51.55) * mm, "end": v(14.63, -51.17) * mm});
            skLineSegment(sketch, "E1797", {"start": v(14.63, -51.17) * mm, "end": v(14.5, -50.8) * mm});
            skLineSegment(sketch, "E1798", {"start": v(14.5, -50.8) * mm, "end": v(14.38, -50.42) * mm});
            skLineSegment(sketch, "E1799", {"start": v(14.38, -50.42) * mm, "end": v(14.26, -50.04) * mm});
            skLineSegment(sketch, "E1800", {"start": v(14.26, -50.04) * mm, "end": v(14.14, -49.67) * mm});
            skLineSegment(sketch, "E1801", {"start": v(14.14, -49.67) * mm, "end": v(14.02, -49.29) * mm});
            skLineSegment(sketch, "E1802", {"start": v(14.02, -49.29) * mm, "end": v(13.91, -48.97) * mm});
            skLineSegment(sketch, "E1803", {"start": v(13.91, -48.97) * mm, "end": v(14.28, -48.83) * mm});
            skLineSegment(sketch, "E1804", {"start": v(14.28, -48.83) * mm, "end": v(14.65, -48.7) * mm});
            skLineSegment(sketch, "E1805", {"start": v(14.65, -48.7) * mm, "end": v(15.02, -48.55) * mm});
            skLineSegment(sketch, "E1806", {"start": v(15.02, -48.55) * mm, "end": v(15.39, -48.42) * mm});
            skLineSegment(sketch, "E1807", {"start": v(15.39, -48.42) * mm, "end": v(15.76, -48.28) * mm});
            skLineSegment(sketch, "E1808", {"start": v(15.76, -48.28) * mm, "end": v(16.13, -48.14) * mm});
            skLineSegment(sketch, "E1809", {"start": v(16.13, -48.14) * mm, "end": v(16.5, -48) * mm});
            skLineSegment(sketch, "E1810", {"start": v(16.5, -48) * mm, "end": v(16.86, -47.87) * mm});
            skLineSegment(sketch, "E1811", {"start": v(16.86, -47.87) * mm, "end": v(17.23, -47.73) * mm});
            skLineSegment(sketch, "E1812", {"start": v(17.23, -47.73) * mm, "end": v(17.6, -47.6) * mm});
            skLineSegment(sketch, "E1813", {"start": v(17.6, -47.6) * mm, "end": v(17.97, -47.45) * mm});
            skLineSegment(sketch, "E1814", {"start": v(17.97, -47.45) * mm, "end": v(18.06, -47.42) * mm});
            skLineSegment(sketch, "E1815", {"start": v(18.06, -47.42) * mm, "end": v(18.21, -47.78) * mm});
            skLineSegment(sketch, "E1816", {"start": v(18.21, -47.78) * mm, "end": v(18.36, -48.15) * mm});
            skLineSegment(sketch, "E1817", {"start": v(18.36, -48.15) * mm, "end": v(18.52, -48.51) * mm});
            skLineSegment(sketch, "E1818", {"start": v(18.52, -48.51) * mm, "end": v(18.67, -48.88) * mm});
            skLineSegment(sketch, "E1819", {"start": v(18.67, -48.88) * mm, "end": v(18.83, -49.24) * mm});
            skLineSegment(sketch, "E1820", {"start": v(18.83, -49.24) * mm, "end": v(18.98, -49.6) * mm});
            skLineSegment(sketch, "E1821", {"start": v(18.98, -49.6) * mm, "end": v(19.13, -49.97) * mm});
            skLineSegment(sketch, "E1822", {"start": v(19.13, -49.97) * mm, "end": v(19.29, -50.33) * mm});
            skLineSegment(sketch, "E1823", {"start": v(19.29, -50.33) * mm, "end": v(19.44, -50.7) * mm});
            skLineSegment(sketch, "E1824", {"start": v(19.44, -50.7) * mm, "end": v(19.6, -51.06) * mm});
            skLineSegment(sketch, "E1825", {"start": v(19.6, -51.06) * mm, "end": v(19.75, -51.42) * mm});
            skLineSegment(sketch, "E1826", {"start": v(19.75, -51.42) * mm, "end": v(19.9, -51.8) * mm});
            skLineSegment(sketch, "E1827", {"start": v(19.9, -51.8) * mm, "end": v(20.07, -52.18) * mm});
            skLineSegment(sketch, "E1828", {"start": v(20.07, -52.18) * mm, "end": v(20.31, -52.53) * mm});
            skLineSegment(sketch, "E1829", {"start": v(20.31, -52.53) * mm, "end": v(20.63, -52.8) * mm});
            skLineSegment(sketch, "E1830", {"start": v(20.63, -52.8) * mm, "end": v(21.02, -52.99) * mm});
            skLineSegment(sketch, "E1831", {"start": v(21.02, -52.99) * mm, "end": v(21.43, -53.06) * mm});
            skLineSegment(sketch, "E1832", {"start": v(21.43, -53.06) * mm, "end": v(21.86, -53.03) * mm});
            skLineSegment(sketch, "E1833", {"start": v(21.86, -53.03) * mm, "end": v(22.18, -52.92) * mm});
            skLineSegment(sketch, "E1834", {"start": v(22.18, -52.92) * mm, "end": v(22.54, -52.7) * mm});
            skLineSegment(sketch, "E1835", {"start": v(22.54, -52.7) * mm, "end": v(22.82, -52.38) * mm});
            skLineSegment(sketch, "E1836", {"start": v(22.82, -52.38) * mm, "end": v(23.02, -52) * mm});
            skLineSegment(sketch, "E1837", {"start": v(23.02, -52) * mm, "end": v(23.11, -51.6) * mm});
            skLineSegment(sketch, "E1838", {"start": v(23.11, -51.6) * mm, "end": v(23.1, -51.17) * mm});
            skLineSegment(sketch, "E1839", {"start": v(23.1, -51.17) * mm, "end": v(22.96, -50.77) * mm});
            skLineSegment(sketch, "E1840", {"start": v(22.96, -50.77) * mm, "end": v(22.79, -50.42) * mm});
            skLineSegment(sketch, "E1841", {"start": v(22.79, -50.42) * mm, "end": v(22.61, -50.06) * mm});
            skLineSegment(sketch, "E1842", {"start": v(22.61, -50.06) * mm, "end": v(22.44, -49.7) * mm});
            skLineSegment(sketch, "E1843", {"start": v(22.44, -49.7) * mm, "end": v(22.26, -49.35) * mm});
            skLineSegment(sketch, "E1844", {"start": v(22.26, -49.35) * mm, "end": v(22.1, -49) * mm});
            skLineSegment(sketch, "E1845", {"start": v(22.1, -49) * mm, "end": v(21.92, -48.64) * mm});
            skLineSegment(sketch, "E1846", {"start": v(21.92, -48.64) * mm, "end": v(21.74, -48.29) * mm});
            skLineSegment(sketch, "E1847", {"start": v(21.74, -48.29) * mm, "end": v(21.57, -47.93) * mm});
            skLineSegment(sketch, "E1848", {"start": v(21.57, -47.93) * mm, "end": v(21.4, -47.57) * mm});
            skLineSegment(sketch, "E1849", {"start": v(21.4, -47.57) * mm, "end": v(21.22, -47.22) * mm});
            skLineSegment(sketch, "E1850", {"start": v(21.22, -47.22) * mm, "end": v(21.04, -46.87) * mm});
            skLineSegment(sketch, "E1851", {"start": v(21.04, -46.87) * mm, "end": v(20.87, -46.5) * mm});
            skLineSegment(sketch, "E1852", {"start": v(20.87, -46.5) * mm, "end": v(20.72, -46.2) * mm});
            skLineSegment(sketch, "E1853", {"start": v(20.72, -46.2) * mm, "end": v(21.06, -46.02) * mm});
            skLineSegment(sketch, "E1854", {"start": v(21.06, -46.02) * mm, "end": v(21.41, -45.83) * mm});
            skLineSegment(sketch, "E1855", {"start": v(21.41, -45.83) * mm, "end": v(21.76, -45.64) * mm});
            skLineSegment(sketch, "E1856", {"start": v(21.76, -45.64) * mm, "end": v(22.1, -45.45) * mm});
            skLineSegment(sketch, "E1857", {"start": v(22.1, -45.45) * mm, "end": v(22.45, -45.26) * mm});
            skLineSegment(sketch, "E1858", {"start": v(22.45, -45.26) * mm, "end": v(22.8, -45.07) * mm});
            skLineSegment(sketch, "E1859", {"start": v(22.8, -45.07) * mm, "end": v(23.14, -44.88) * mm});
            skLineSegment(sketch, "E1860", {"start": v(23.14, -44.88) * mm, "end": v(23.48, -44.7) * mm});
            skLineSegment(sketch, "E1861", {"start": v(23.48, -44.7) * mm, "end": v(23.83, -44.5) * mm});
            skLineSegment(sketch, "E1862", {"start": v(23.83, -44.5) * mm, "end": v(24.18, -44.32) * mm});
            skLineSegment(sketch, "E1863", {"start": v(24.18, -44.32) * mm, "end": v(24.52, -44.13) * mm});
            skLineSegment(sketch, "E1864", {"start": v(24.52, -44.13) * mm, "end": v(24.6, -44.08) * mm});
            skLineSegment(sketch, "E1865", {"start": v(24.6, -44.08) * mm, "end": v(24.8, -44.42) * mm});
            skLineSegment(sketch, "E1866", {"start": v(24.8, -44.42) * mm, "end": v(25, -44.76) * mm});
            skLineSegment(sketch, "E1867", {"start": v(25, -44.76) * mm, "end": v(25.21, -45.1) * mm});
            skLineSegment(sketch, "E1868", {"start": v(25.21, -45.1) * mm, "end": v(25.42, -45.44) * mm});
            skLineSegment(sketch, "E1869", {"start": v(25.42, -45.44) * mm, "end": v(25.62, -45.78) * mm});
            skLineSegment(sketch, "E1870", {"start": v(25.62, -45.78) * mm, "end": v(25.83, -46.12) * mm});
            skLineSegment(sketch, "E1871", {"start": v(25.83, -46.12) * mm, "end": v(26.03, -46.45) * mm});
            skLineSegment(sketch, "E1872", {"start": v(26.03, -46.45) * mm, "end": v(26.23, -46.8) * mm});
            skLineSegment(sketch, "E1873", {"start": v(26.23, -46.8) * mm, "end": v(26.44, -47.13) * mm});
            skLineSegment(sketch, "E1874", {"start": v(26.44, -47.13) * mm, "end": v(26.64, -47.47) * mm});
            skLineSegment(sketch, "E1875", {"start": v(26.64, -47.47) * mm, "end": v(26.85, -47.8) * mm});
            skLineSegment(sketch, "E1876", {"start": v(26.85, -47.8) * mm, "end": v(27.05, -48.15) * mm});
            skLineSegment(sketch, "E1877", {"start": v(27.05, -48.15) * mm, "end": v(27.28, -48.51) * mm});
            skLineSegment(sketch, "E1878", {"start": v(27.28, -48.51) * mm, "end": v(27.56, -48.82) * mm});
            skLineSegment(sketch, "E1879", {"start": v(27.56, -48.82) * mm, "end": v(27.92, -49.05) * mm});
            skLineSegment(sketch, "E1880", {"start": v(27.92, -49.05) * mm, "end": v(28.32, -49.17) * mm});
            skLineSegment(sketch, "E1881", {"start": v(28.32, -49.17) * mm, "end": v(28.75, -49.19) * mm});
            skLineSegment(sketch, "E1882", {"start": v(28.75, -49.19) * mm, "end": v(29.16, -49.1) * mm});
            skLineSegment(sketch, "E1883", {"start": v(29.16, -49.1) * mm, "end": v(29.46, -48.94) * mm});
            skLineSegment(sketch, "E1884", {"start": v(29.46, -48.94) * mm, "end": v(29.78, -48.67) * mm});
            skLineSegment(sketch, "E1885", {"start": v(29.78, -48.67) * mm, "end": v(30.03, -48.32) * mm});
            skLineSegment(sketch, "E1886", {"start": v(30.03, -48.32) * mm, "end": v(30.17, -47.92) * mm});
            skLineSegment(sketch, "E1887", {"start": v(30.17, -47.92) * mm, "end": v(30.2, -47.5) * mm});
            skLineSegment(sketch, "E1888", {"start": v(30.2, -47.5) * mm, "end": v(30.12, -47.08) * mm});
            skLineSegment(sketch, "E1889", {"start": v(30.12, -47.08) * mm, "end": v(29.93, -46.7) * mm});
            skLineSegment(sketch, "E1890", {"start": v(29.93, -46.7) * mm, "end": v(29.71, -46.38) * mm});
            skLineSegment(sketch, "E1891", {"start": v(29.71, -46.38) * mm, "end": v(29.49, -46.05) * mm});
            skLineSegment(sketch, "E1892", {"start": v(29.49, -46.05) * mm, "end": v(29.26, -45.72) * mm});
            skLineSegment(sketch, "E1893", {"start": v(29.26, -45.72) * mm, "end": v(29.04, -45.4) * mm});
            skLineSegment(sketch, "E1894", {"start": v(29.04, -45.4) * mm, "end": v(28.82, -45.07) * mm});
            skLineSegment(sketch, "E1895", {"start": v(28.82, -45.07) * mm, "end": v(28.6, -44.74) * mm});
            skLineSegment(sketch, "E1896", {"start": v(28.6, -44.74) * mm, "end": v(28.37, -44.42) * mm});
            skLineSegment(sketch, "E1897", {"start": v(28.37, -44.42) * mm, "end": v(28.15, -44.1) * mm});
            skLineSegment(sketch, "E1898", {"start": v(28.15, -44.1) * mm, "end": v(27.92, -43.76) * mm});
            skLineSegment(sketch, "E1899", {"start": v(27.92, -43.76) * mm, "end": v(27.7, -43.44) * mm});
            skLineSegment(sketch, "E1900", {"start": v(27.7, -43.44) * mm, "end": v(27.48, -43.11) * mm});
            skLineSegment(sketch, "E1901", {"start": v(27.48, -43.11) * mm, "end": v(27.25, -42.78) * mm});
            skLineSegment(sketch, "E1902", {"start": v(27.25, -42.78) * mm, "end": v(27.06, -42.5) * mm});
            skLineSegment(sketch, "E1903", {"start": v(27.06, -42.5) * mm, "end": v(27.38, -42.27) * mm});
            skLineSegment(sketch, "E1904", {"start": v(27.38, -42.27) * mm, "end": v(27.7, -42.03) * mm});
            skLineSegment(sketch, "E1905", {"start": v(27.7, -42.03) * mm, "end": v(28, -41.8) * mm});
            skLineSegment(sketch, "E1906", {"start": v(28, -41.8) * mm, "end": v(28.32, -41.56) * mm});
            skLineSegment(sketch, "E1907", {"start": v(28.32, -41.56) * mm, "end": v(28.64, -41.32) * mm});
            skLineSegment(sketch, "E1908", {"start": v(28.64, -41.32) * mm, "end": v(28.95, -41.09) * mm});
            skLineSegment(sketch, "E1909", {"start": v(28.95, -41.09) * mm, "end": v(29.27, -40.85) * mm});
            skLineSegment(sketch, "E1910", {"start": v(29.27, -40.85) * mm, "end": v(29.59, -40.61) * mm});
            skLineSegment(sketch, "E1911", {"start": v(29.59, -40.61) * mm, "end": v(29.9, -40.38) * mm});
            skLineSegment(sketch, "E1912", {"start": v(29.9, -40.38) * mm, "end": v(30.22, -40.14) * mm});
            skLineSegment(sketch, "E1913", {"start": v(30.22, -40.14) * mm, "end": v(30.53, -39.9) * mm});
            skLineSegment(sketch, "E1914", {"start": v(30.53, -39.9) * mm, "end": v(30.6, -39.85) * mm});
            skLineSegment(sketch, "E1915", {"start": v(30.6, -39.85) * mm, "end": v(30.85, -40.16) * mm});
            skLineSegment(sketch, "E1916", {"start": v(30.85, -40.16) * mm, "end": v(31.1, -40.46) * mm});
            skLineSegment(sketch, "E1917", {"start": v(31.1, -40.46) * mm, "end": v(31.36, -40.77) * mm});
            skLineSegment(sketch, "E1918", {"start": v(31.36, -40.77) * mm, "end": v(31.6, -41.08) * mm});
            skLineSegment(sketch, "E1919", {"start": v(31.6, -41.08) * mm, "end": v(31.85, -41.38) * mm});
            skLineSegment(sketch, "E1920", {"start": v(31.85, -41.38) * mm, "end": v(32.1, -41.69) * mm});
            skLineSegment(sketch, "E1921", {"start": v(32.1, -41.69) * mm, "end": v(32.36, -42) * mm});
            skLineSegment(sketch, "E1922", {"start": v(32.36, -42) * mm, "end": v(32.6, -42.3) * mm});
            skLineSegment(sketch, "E1923", {"start": v(32.6, -42.3) * mm, "end": v(32.86, -42.6) * mm});
            skLineSegment(sketch, "E1924", {"start": v(32.86, -42.6) * mm, "end": v(33.1, -42.91) * mm});
            skLineSegment(sketch, "E1925", {"start": v(33.1, -42.91) * mm, "end": v(33.36, -43.22) * mm});
            skLineSegment(sketch, "E1926", {"start": v(33.36, -43.22) * mm, "end": v(33.6, -43.53) * mm});
            skLineSegment(sketch, "E1927", {"start": v(33.6, -43.53) * mm, "end": v(33.88, -43.85) * mm});
            skLineSegment(sketch, "E1928", {"start": v(33.88, -43.85) * mm, "end": v(34.2, -44.12) * mm});
            skLineSegment(sketch, "E1929", {"start": v(34.2, -44.12) * mm, "end": v(34.6, -44.3) * mm});
            skLineSegment(sketch, "E1930", {"start": v(34.6, -44.3) * mm, "end": v(35.01, -44.36) * mm});
            skLineSegment(sketch, "E1931", {"start": v(35.01, -44.36) * mm, "end": v(35.43, -44.31) * mm});
            skLineSegment(sketch, "E1932", {"start": v(35.43, -44.31) * mm, "end": v(35.83, -44.16) * mm});
            skLineSegment(sketch, "E1933", {"start": v(35.83, -44.16) * mm, "end": v(36.1, -43.97) * mm});
            skLineSegment(sketch, "E1934", {"start": v(36.1, -43.97) * mm, "end": v(36.39, -43.65) * mm});
            skLineSegment(sketch, "E1935", {"start": v(36.39, -43.65) * mm, "end": v(36.58, -43.27) * mm});
            skLineSegment(sketch, "E1936", {"start": v(36.58, -43.27) * mm, "end": v(36.66, -42.86) * mm});
            skLineSegment(sketch, "E1937", {"start": v(36.66, -42.86) * mm, "end": v(36.63, -42.43) * mm});
            skLineSegment(sketch, "E1938", {"start": v(36.63, -42.43) * mm, "end": v(36.5, -42.03) * mm});
            skLineSegment(sketch, "E1939", {"start": v(36.5, -42.03) * mm, "end": v(36.25, -41.68) * mm});
            skLineSegment(sketch, "E1940", {"start": v(36.25, -41.68) * mm, "end": v(35.99, -41.4) * mm});
            skLineSegment(sketch, "E1941", {"start": v(35.99, -41.4) * mm, "end": v(35.72, -41.1) * mm});
            skLineSegment(sketch, "E1942", {"start": v(35.72, -41.1) * mm, "end": v(35.45, -40.8) * mm});
            skLineSegment(sketch, "E1943", {"start": v(35.45, -40.8) * mm, "end": v(35.19, -40.52) * mm});
            skLineSegment(sketch, "E1944", {"start": v(35.19, -40.52) * mm, "end": v(34.92, -40.23) * mm});
            skLineSegment(sketch, "E1945", {"start": v(34.92, -40.23) * mm, "end": v(34.65, -39.93) * mm});
            skLineSegment(sketch, "E1946", {"start": v(34.65, -39.93) * mm, "end": v(34.38, -39.64) * mm});
            skLineSegment(sketch, "E1947", {"start": v(34.38, -39.64) * mm, "end": v(34.12, -39.35) * mm});
            skLineSegment(sketch, "E1948", {"start": v(34.12, -39.35) * mm, "end": v(33.85, -39.06) * mm});
            skLineSegment(sketch, "E1949", {"start": v(33.85, -39.06) * mm, "end": v(33.58, -38.77) * mm});
            skLineSegment(sketch, "E1950", {"start": v(33.58, -38.77) * mm, "end": v(33.32, -38.48) * mm});
            skLineSegment(sketch, "E1951", {"start": v(33.32, -38.48) * mm, "end": v(33.05, -38.19) * mm});
            skLineSegment(sketch, "E1952", {"start": v(33.05, -38.19) * mm, "end": v(32.82, -37.94) * mm});
            skLineSegment(sketch, "E1953", {"start": v(32.82, -37.94) * mm, "end": v(33.1, -37.66) * mm});
            skLineSegment(sketch, "E1954", {"start": v(33.1, -37.66) * mm, "end": v(33.37, -37.38) * mm});
            skLineSegment(sketch, "E1955", {"start": v(33.37, -37.38) * mm, "end": v(33.65, -37.1) * mm});
            skLineSegment(sketch, "E1956", {"start": v(33.65, -37.1) * mm, "end": v(33.93, -36.82) * mm});
            skLineSegment(sketch, "E1957", {"start": v(33.93, -36.82) * mm, "end": v(34.2, -36.54) * mm});
            skLineSegment(sketch, "E1958", {"start": v(34.2, -36.54) * mm, "end": v(34.49, -36.26) * mm});
            skLineSegment(sketch, "E1959", {"start": v(34.49, -36.26) * mm, "end": v(34.77, -35.99) * mm});
            skLineSegment(sketch, "E1960", {"start": v(34.77, -35.99) * mm, "end": v(35.04, -35.7) * mm});
            skLineSegment(sketch, "E1961", {"start": v(35.04, -35.7) * mm, "end": v(35.32, -35.43) * mm});
            skLineSegment(sketch, "E1962", {"start": v(35.32, -35.43) * mm, "end": v(35.6, -35.15) * mm});
            skLineSegment(sketch, "E1963", {"start": v(35.6, -35.15) * mm, "end": v(35.88, -34.87) * mm});
            skLineSegment(sketch, "E1964", {"start": v(35.88, -34.87) * mm, "end": v(35.94, -34.8) * mm});
            skLineSegment(sketch, "E1965", {"start": v(35.94, -34.8) * mm, "end": v(36.23, -35.07) * mm});
            skLineSegment(sketch, "E1966", {"start": v(36.23, -35.07) * mm, "end": v(36.52, -35.34) * mm});
            skLineSegment(sketch, "E1967", {"start": v(36.52, -35.34) * mm, "end": v(36.82, -35.6) * mm});
            skLineSegment(sketch, "E1968", {"start": v(36.82, -35.6) * mm, "end": v(37.1, -35.88) * mm});
            skLineSegment(sketch, "E1969", {"start": v(37.1, -35.88) * mm, "end": v(37.4, -36.14) * mm});
            skLineSegment(sketch, "E1970", {"start": v(37.4, -36.14) * mm, "end": v(37.7, -36.41) * mm});
            skLineSegment(sketch, "E1971", {"start": v(37.7, -36.41) * mm, "end": v(37.98, -36.68) * mm});
            skLineSegment(sketch, "E1972", {"start": v(37.98, -36.68) * mm, "end": v(38.27, -36.94) * mm});
            skLineSegment(sketch, "E1973", {"start": v(38.27, -36.94) * mm, "end": v(38.57, -37.21) * mm});
            skLineSegment(sketch, "E1974", {"start": v(38.57, -37.21) * mm, "end": v(38.86, -37.48) * mm});
            skLineSegment(sketch, "E1975", {"start": v(38.86, -37.48) * mm, "end": v(39.15, -37.75) * mm});
            skLineSegment(sketch, "E1976", {"start": v(39.15, -37.75) * mm, "end": v(39.44, -38.02) * mm});
            skLineSegment(sketch, "E1977", {"start": v(39.44, -38.02) * mm, "end": v(39.76, -38.3) * mm});
            skLineSegment(sketch, "E1978", {"start": v(39.76, -38.3) * mm, "end": v(40.12, -38.52) * mm});
            skLineSegment(sketch, "E1979", {"start": v(40.12, -38.52) * mm, "end": v(40.53, -38.64) * mm});
            skLineSegment(sketch, "E1980", {"start": v(40.53, -38.64) * mm, "end": v(40.95, -38.64) * mm});
            skLineSegment(sketch, "E1981", {"start": v(40.95, -38.64) * mm, "end": v(41.36, -38.54) * mm});
            skLineSegment(sketch, "E1982", {"start": v(41.36, -38.54) * mm, "end": v(41.73, -38.33) * mm});
            skLineSegment(sketch, "E1983", {"start": v(41.73, -38.33) * mm, "end": v(41.98, -38.1) * mm});
            skLineSegment(sketch, "E1984", {"start": v(41.98, -38.1) * mm, "end": v(42.2, -37.74) * mm});
            skLineSegment(sketch, "E1985", {"start": v(42.2, -37.74) * mm, "end": v(42.34, -37.34) * mm});
            skLineSegment(sketch, "E1986", {"start": v(42.34, -37.34) * mm, "end": v(42.36, -36.92) * mm});
            skLineSegment(sketch, "E1987", {"start": v(42.36, -36.92) * mm, "end": v(42.28, -36.5) * mm});
            skLineSegment(sketch, "E1988", {"start": v(42.28, -36.5) * mm, "end": v(42.08, -36.13) * mm});
            skLineSegment(sketch, "E1989", {"start": v(42.08, -36.13) * mm, "end": v(41.8, -35.82) * mm});
            skLineSegment(sketch, "E1990", {"start": v(41.8, -35.82) * mm, "end": v(41.5, -35.57) * mm});
            skLineSegment(sketch, "E1991", {"start": v(41.5, -35.57) * mm, "end": v(41.19, -35.32) * mm});
            skLineSegment(sketch, "E1992", {"start": v(41.19, -35.32) * mm, "end": v(40.88, -35.06) * mm});
            skLineSegment(sketch, "E1993", {"start": v(40.88, -35.06) * mm, "end": v(40.57, -34.82) * mm});
            skLineSegment(sketch, "E1994", {"start": v(40.57, -34.82) * mm, "end": v(40.27, -34.57) * mm});
            skLineSegment(sketch, "E1995", {"start": v(40.27, -34.57) * mm, "end": v(39.96, -34.31) * mm});
            skLineSegment(sketch, "E1996", {"start": v(39.96, -34.31) * mm, "end": v(39.66, -34.06) * mm});
            skLineSegment(sketch, "E1997", {"start": v(39.66, -34.06) * mm, "end": v(39.35, -33.81) * mm});
            skLineSegment(sketch, "E1998", {"start": v(39.35, -33.81) * mm, "end": v(39.04, -33.56) * mm});
            skLineSegment(sketch, "E1999", {"start": v(39.04, -33.56) * mm, "end": v(38.74, -33.31) * mm});
            skLineSegment(sketch, "E2000", {"start": v(38.74, -33.31) * mm, "end": v(38.43, -33.06) * mm});
            skLineSegment(sketch, "E2001", {"start": v(38.43, -33.06) * mm, "end": v(38.12, -32.81) * mm});
            skLineSegment(sketch, "E2002", {"start": v(38.12, -32.81) * mm, "end": v(37.86, -32.6) * mm});
            skLineSegment(sketch, "E2003", {"start": v(37.86, -32.6) * mm, "end": v(38.1, -32.28) * mm});
            skLineSegment(sketch, "E2004", {"start": v(38.1, -32.28) * mm, "end": v(38.33, -31.97) * mm});
            skLineSegment(sketch, "E2005", {"start": v(38.33, -31.97) * mm, "end": v(38.57, -31.65) * mm});
            skLineSegment(sketch, "E2006", {"start": v(38.57, -31.65) * mm, "end": v(38.8, -31.33) * mm});
            skLineSegment(sketch, "E2007", {"start": v(38.8, -31.33) * mm, "end": v(39.04, -31.02) * mm});
            skLineSegment(sketch, "E2008", {"start": v(39.04, -31.02) * mm, "end": v(39.28, -30.7) * mm});
            skLineSegment(sketch, "E2009", {"start": v(39.28, -30.7) * mm, "end": v(39.51, -30.39) * mm});
            skLineSegment(sketch, "E2010", {"start": v(39.51, -30.39) * mm, "end": v(39.75, -30.07) * mm});
            skLineSegment(sketch, "E2011", {"start": v(39.75, -30.07) * mm, "end": v(39.98, -29.76) * mm});
            skLineSegment(sketch, "E2012", {"start": v(39.98, -29.76) * mm, "end": v(40.22, -29.44) * mm});
            skLineSegment(sketch, "E2013", {"start": v(40.22, -29.44) * mm, "end": v(40.46, -29.13) * mm});
            skLineSegment(sketch, "E2014", {"start": v(40.46, -29.13) * mm, "end": v(40.51, -29.05) * mm});
            skLineSegment(sketch, "E2015", {"start": v(40.51, -29.05) * mm, "end": v(40.84, -29.28) * mm});
            skLineSegment(sketch, "E2016", {"start": v(40.84, -29.28) * mm, "end": v(41.16, -29.5) * mm});
            skLineSegment(sketch, "E2017", {"start": v(41.16, -29.5) * mm, "end": v(41.5, -29.72) * mm});
            skLineSegment(sketch, "E2018", {"start": v(41.5, -29.72) * mm, "end": v(41.82, -29.95) * mm});
            skLineSegment(sketch, "E2019", {"start": v(41.82, -29.95) * mm, "end": v(42.14, -30.17) * mm});
            skLineSegment(sketch, "E2020", {"start": v(42.14, -30.17) * mm, "end": v(42.47, -30.4) * mm});
            skLineSegment(sketch, "E2021", {"start": v(42.47, -30.4) * mm, "end": v(42.8, -30.62) * mm});
            skLineSegment(sketch, "E2022", {"start": v(42.8, -30.62) * mm, "end": v(43.12, -30.84) * mm});
            skLineSegment(sketch, "E2023", {"start": v(43.12, -30.84) * mm, "end": v(43.45, -31.06) * mm});
            skLineSegment(sketch, "E2024", {"start": v(43.45, -31.06) * mm, "end": v(43.78, -31.29) * mm});
            skLineSegment(sketch, "E2025", {"start": v(43.78, -31.29) * mm, "end": v(44.1, -31.5) * mm});
            skLineSegment(sketch, "E2026", {"start": v(44.1, -31.5) * mm, "end": v(44.43, -31.73) * mm});
            skLineSegment(sketch, "E2027", {"start": v(44.43, -31.73) * mm, "end": v(44.78, -31.97) * mm});
            skLineSegment(sketch, "E2028", {"start": v(44.78, -31.97) * mm, "end": v(45.17, -32.13) * mm});
            skLineSegment(sketch, "E2029", {"start": v(45.17, -32.13) * mm, "end": v(45.6, -32.2) * mm});
            skLineSegment(sketch, "E2030", {"start": v(45.6, -32.2) * mm, "end": v(46.01, -32.14) * mm});
            skLineSegment(sketch, "E2031", {"start": v(46.01, -32.14) * mm, "end": v(46.4, -31.98) * mm});
            skLineSegment(sketch, "E2032", {"start": v(46.4, -31.98) * mm, "end": v(46.74, -31.72) * mm});
            skLineSegment(sketch, "E2033", {"start": v(46.74, -31.72) * mm, "end": v(46.95, -31.45) * mm});
            skLineSegment(sketch, "E2034", {"start": v(46.95, -31.45) * mm, "end": v(47.13, -31.07) * mm});
            skLineSegment(sketch, "E2035", {"start": v(47.13, -31.07) * mm, "end": v(47.2, -30.65) * mm});
            skLineSegment(sketch, "E2036", {"start": v(47.2, -30.65) * mm, "end": v(47.17, -30.23) * mm});
            skLineSegment(sketch, "E2037", {"start": v(47.17, -30.23) * mm, "end": v(47.02, -29.83) * mm});
            skLineSegment(sketch, "E2038", {"start": v(47.02, -29.83) * mm, "end": v(46.78, -29.49) * mm});
            skLineSegment(sketch, "E2039", {"start": v(46.78, -29.49) * mm, "end": v(46.45, -29.22) * mm});
            skLineSegment(sketch, "E2040", {"start": v(46.45, -29.22) * mm, "end": v(46.11, -29.02) * mm});
            skLineSegment(sketch, "E2041", {"start": v(46.11, -29.02) * mm, "end": v(45.77, -28.81) * mm});
            skLineSegment(sketch, "E2042", {"start": v(45.77, -28.81) * mm, "end": v(45.43, -28.6) * mm});
            skLineSegment(sketch, "E2043", {"start": v(45.43, -28.6) * mm, "end": v(45.1, -28.4) * mm});
            skLineSegment(sketch, "E2044", {"start": v(45.1, -28.4) * mm, "end": v(44.76, -28.2) * mm});
            skLineSegment(sketch, "E2045", {"start": v(44.76, -28.2) * mm, "end": v(44.42, -28) * mm});
            skLineSegment(sketch, "E2046", {"start": v(44.42, -28) * mm, "end": v(44.08, -27.8) * mm});
            skLineSegment(sketch, "E2047", {"start": v(44.08, -27.8) * mm, "end": v(43.74, -27.59) * mm});
            skLineSegment(sketch, "E2048", {"start": v(43.74, -27.59) * mm, "end": v(43.4, -27.38) * mm});
            skLineSegment(sketch, "E2049", {"start": v(43.4, -27.38) * mm, "end": v(43.06, -27.18) * mm});
            skLineSegment(sketch, "E2050", {"start": v(43.06, -27.18) * mm, "end": v(42.73, -26.97) * mm});
            skLineSegment(sketch, "E2051", {"start": v(42.73, -26.97) * mm, "end": v(42.38, -26.77) * mm});
            skLineSegment(sketch, "E2052", {"start": v(42.38, -26.77) * mm, "end": v(42.1, -26.6) * mm});
            skLineSegment(sketch, "E2053", {"start": v(42.1, -26.6) * mm, "end": v(42.28, -26.25) * mm});
            skLineSegment(sketch, "E2054", {"start": v(42.28, -26.25) * mm, "end": v(42.47, -25.9) * mm});
            skLineSegment(sketch, "E2055", {"start": v(42.47, -25.9) * mm, "end": v(42.66, -25.56) * mm});
            skLineSegment(sketch, "E2056", {"start": v(42.66, -25.56) * mm, "end": v(42.85, -25.21) * mm});
            skLineSegment(sketch, "E2057", {"start": v(42.85, -25.21) * mm, "end": v(43.04, -24.86) * mm});
            skLineSegment(sketch, "E2058", {"start": v(43.04, -24.86) * mm, "end": v(43.23, -24.52) * mm});
            skLineSegment(sketch, "E2059", {"start": v(43.23, -24.52) * mm, "end": v(43.41, -24.17) * mm});
            skLineSegment(sketch, "E2060", {"start": v(43.41, -24.17) * mm, "end": v(43.6, -23.83) * mm});
            skLineSegment(sketch, "E2061", {"start": v(43.6, -23.83) * mm, "end": v(43.8, -23.48) * mm});
            skLineSegment(sketch, "E2062", {"start": v(43.8, -23.48) * mm, "end": v(43.98, -23.14) * mm});
            skLineSegment(sketch, "E2063", {"start": v(43.98, -23.14) * mm, "end": v(44.17, -22.8) * mm});
            skLineSegment(sketch, "E2064", {"start": v(44.17, -22.8) * mm, "end": v(44.21, -22.71) * mm});
            skLineSegment(sketch, "E2065", {"start": v(44.21, -22.71) * mm, "end": v(44.57, -22.88) * mm});
            skLineSegment(sketch, "E2066", {"start": v(44.57, -22.88) * mm, "end": v(44.92, -23.06) * mm});
            skLineSegment(sketch, "E2067", {"start": v(44.92, -23.06) * mm, "end": v(45.28, -23.23) * mm});
            skLineSegment(sketch, "E2068", {"start": v(45.28, -23.23) * mm, "end": v(45.63, -23.4) * mm});
            skLineSegment(sketch, "E2069", {"start": v(45.63, -23.4) * mm, "end": v(45.99, -23.58) * mm});
            skLineSegment(sketch, "E2070", {"start": v(45.99, -23.58) * mm, "end": v(46.34, -23.76) * mm});
            skLineSegment(sketch, "E2071", {"start": v(46.34, -23.76) * mm, "end": v(46.7, -23.93) * mm});
            skLineSegment(sketch, "E2072", {"start": v(46.7, -23.93) * mm, "end": v(47.05, -24.1) * mm});
            skLineSegment(sketch, "E2073", {"start": v(47.05, -24.1) * mm, "end": v(47.4, -24.28) * mm});
            skLineSegment(sketch, "E2074", {"start": v(47.4, -24.28) * mm, "end": v(47.76, -24.45) * mm});
            skLineSegment(sketch, "E2075", {"start": v(47.76, -24.45) * mm, "end": v(48.12, -24.63) * mm});
            skLineSegment(sketch, "E2076", {"start": v(48.12, -24.63) * mm, "end": v(48.47, -24.8) * mm});
            skLineSegment(sketch, "E2077", {"start": v(48.47, -24.8) * mm, "end": v(48.86, -24.99) * mm});
            skLineSegment(sketch, "E2078", {"start": v(48.86, -24.99) * mm, "end": v(49.26, -25.1) * mm});
            skLineSegment(sketch, "E2079", {"start": v(49.26, -25.1) * mm, "end": v(49.69, -25.1) * mm});
            skLineSegment(sketch, "E2080", {"start": v(49.69, -25.1) * mm, "end": v(50.1, -24.98) * mm});
            skLineSegment(sketch, "E2081", {"start": v(50.1, -24.98) * mm, "end": v(50.46, -24.76) * mm});
            skLineSegment(sketch, "E2082", {"start": v(50.46, -24.76) * mm, "end": v(50.76, -24.46) * mm});
            skLineSegment(sketch, "E2083", {"start": v(50.76, -24.46) * mm, "end": v(50.93, -24.17) * mm});
            skLineSegment(sketch, "E2084", {"start": v(50.93, -24.17) * mm, "end": v(51.05, -23.76) * mm});
            skLineSegment(sketch, "E2085", {"start": v(51.05, -23.76) * mm, "end": v(51.07, -23.34) * mm});
            skLineSegment(sketch, "E2086", {"start": v(51.07, -23.34) * mm, "end": v(50.97, -22.93) * mm});
            skLineSegment(sketch, "E2087", {"start": v(50.97, -22.93) * mm, "end": v(50.77, -22.56) * mm});
            skLineSegment(sketch, "E2088", {"start": v(50.77, -22.56) * mm, "end": v(50.48, -22.25) * mm});
            skLineSegment(sketch, "E2089", {"start": v(50.48, -22.25) * mm, "end": v(50.11, -22.03) * mm});
            skLineSegment(sketch, "E2090", {"start": v(50.11, -22.03) * mm, "end": v(49.75, -21.88) * mm});
            skLineSegment(sketch, "E2091", {"start": v(49.75, -21.88) * mm, "end": v(49.39, -21.72) * mm});
            skLineSegment(sketch, "E2092", {"start": v(49.39, -21.72) * mm, "end": v(49.02, -21.57) * mm});
            skLineSegment(sketch, "E2093", {"start": v(49.02, -21.57) * mm, "end": v(48.66, -21.41) * mm});
            skLineSegment(sketch, "E2094", {"start": v(48.66, -21.41) * mm, "end": v(48.3, -21.26) * mm});
            skLineSegment(sketch, "E2095", {"start": v(48.3, -21.26) * mm, "end": v(47.93, -21.1) * mm});
            skLineSegment(sketch, "E2096", {"start": v(47.93, -21.1) * mm, "end": v(47.56, -20.95) * mm});
            skLineSegment(sketch, "E2097", {"start": v(47.56, -20.95) * mm, "end": v(47.2, -20.8) * mm});
            skLineSegment(sketch, "E2098", {"start": v(47.2, -20.8) * mm, "end": v(46.83, -20.64) * mm});
            skLineSegment(sketch, "E2099", {"start": v(46.83, -20.64) * mm, "end": v(46.47, -20.49) * mm});
            skLineSegment(sketch, "E2100", {"start": v(46.47, -20.49) * mm, "end": v(46.1, -20.34) * mm});
            skLineSegment(sketch, "E2101", {"start": v(46.1, -20.34) * mm, "end": v(45.74, -20.18) * mm});
            skLineSegment(sketch, "E2102", {"start": v(45.74, -20.18) * mm, "end": v(45.43, -20.05) * mm});
            skLineSegment(sketch, "E2103", {"start": v(45.43, -20.05) * mm, "end": v(45.57, -19.68) * mm});
            skLineSegment(sketch, "E2104", {"start": v(45.57, -19.68) * mm, "end": v(45.7, -19.31) * mm});
            skLineSegment(sketch, "E2105", {"start": v(45.7, -19.31) * mm, "end": v(45.84, -18.94) * mm});
            skLineSegment(sketch, "E2106", {"start": v(45.84, -18.94) * mm, "end": v(45.98, -18.57) * mm});
            skLineSegment(sketch, "E2107", {"start": v(45.98, -18.57) * mm, "end": v(46.12, -18.2) * mm});
            skLineSegment(sketch, "E2108", {"start": v(46.12, -18.2) * mm, "end": v(46.26, -17.83) * mm});
            skLineSegment(sketch, "E2109", {"start": v(46.26, -17.83) * mm, "end": v(46.4, -17.47) * mm});
            skLineSegment(sketch, "E2110", {"start": v(46.4, -17.47) * mm, "end": v(46.53, -17.1) * mm});
            skLineSegment(sketch, "E2111", {"start": v(46.53, -17.1) * mm, "end": v(46.67, -16.73) * mm});
            skLineSegment(sketch, "E2112", {"start": v(46.67, -16.73) * mm, "end": v(46.8, -16.36) * mm});
            skLineSegment(sketch, "E2113", {"start": v(46.8, -16.36) * mm, "end": v(46.94, -15.99) * mm});
            skLineSegment(sketch, "E2114", {"start": v(46.94, -15.99) * mm, "end": v(46.98, -15.9) * mm});
            skLineSegment(sketch, "E2115", {"start": v(46.98, -15.9) * mm, "end": v(47.35, -16.03) * mm});
            skLineSegment(sketch, "E2116", {"start": v(47.35, -16.03) * mm, "end": v(47.72, -16.15) * mm});
            skLineSegment(sketch, "E2117", {"start": v(47.72, -16.15) * mm, "end": v(48.1, -16.27) * mm});
            skLineSegment(sketch, "E2118", {"start": v(48.1, -16.27) * mm, "end": v(48.48, -16.4) * mm});
            skLineSegment(sketch, "E2119", {"start": v(48.48, -16.4) * mm, "end": v(48.85, -16.51) * mm});
            skLineSegment(sketch, "E2120", {"start": v(48.85, -16.51) * mm, "end": v(49.23, -16.64) * mm});
            skLineSegment(sketch, "E2121", {"start": v(49.23, -16.64) * mm, "end": v(49.6, -16.76) * mm});
            skLineSegment(sketch, "E2122", {"start": v(49.6, -16.76) * mm, "end": v(49.98, -16.88) * mm});
            skLineSegment(sketch, "E2123", {"start": v(49.98, -16.88) * mm, "end": v(50.36, -17) * mm});
            skLineSegment(sketch, "E2124", {"start": v(50.36, -17) * mm, "end": v(50.74, -17.12) * mm});
            skLineSegment(sketch, "E2125", {"start": v(50.74, -17.12) * mm, "end": v(51.11, -17.25) * mm});
            skLineSegment(sketch, "E2126", {"start": v(51.11, -17.25) * mm, "end": v(51.49, -17.37) * mm});
            skLineSegment(sketch, "E2127", {"start": v(51.49, -17.37) * mm, "end": v(51.9, -17.5) * mm});
            skLineSegment(sketch, "E2128", {"start": v(51.9, -17.5) * mm, "end": v(52.31, -17.55) * mm});
            skLineSegment(sketch, "E2129", {"start": v(52.31, -17.55) * mm, "end": v(52.73, -17.48) * mm});
            skLineSegment(sketch, "E2130", {"start": v(52.73, -17.48) * mm, "end": v(53.12, -17.31) * mm});
            skLineSegment(sketch, "E2131", {"start": v(53.12, -17.31) * mm, "end": v(53.45, -17.05) * mm});
            skLineSegment(sketch, "E2132", {"start": v(53.45, -17.05) * mm, "end": v(53.7, -16.7) * mm});
            skLineSegment(sketch, "E2133", {"start": v(53.7, -16.7) * mm, "end": v(53.83, -16.4) * mm});
            skLineSegment(sketch, "E2134", {"start": v(53.83, -16.4) * mm, "end": v(53.9, -15.97) * mm});
            skLineSegment(sketch, "E2135", {"start": v(53.9, -15.97) * mm, "end": v(53.85, -15.55) * mm});
            skLineSegment(sketch, "E2136", {"start": v(53.85, -15.55) * mm, "end": v(53.7, -15.16) * mm});
            skLineSegment(sketch, "E2137", {"start": v(53.7, -15.16) * mm, "end": v(53.44, -14.82) * mm});
            skLineSegment(sketch, "E2138", {"start": v(53.44, -14.82) * mm, "end": v(53.1, -14.56) * mm});
            skLineSegment(sketch, "E2139", {"start": v(53.1, -14.56) * mm, "end": v(52.72, -14.39) * mm});
            skLineSegment(sketch, "E2140", {"start": v(52.72, -14.39) * mm, "end": v(52.34, -14.29) * mm});
            skLineSegment(sketch, "E2141", {"start": v(52.34, -14.29) * mm, "end": v(51.96, -14.19) * mm});
            skLineSegment(sketch, "E2142", {"start": v(51.96, -14.19) * mm, "end": v(51.57, -14.09) * mm});
            skLineSegment(sketch, "E2143", {"start": v(51.57, -14.09) * mm, "end": v(51.19, -13.99) * mm});
            skLineSegment(sketch, "E2144", {"start": v(51.19, -13.99) * mm, "end": v(50.8, -13.89) * mm});
            skLineSegment(sketch, "E2145", {"start": v(50.8, -13.89) * mm, "end": v(50.42, -13.79) * mm});
            skLineSegment(sketch, "E2146", {"start": v(50.42, -13.79) * mm, "end": v(50.04, -13.69) * mm});
            skLineSegment(sketch, "E2147", {"start": v(50.04, -13.69) * mm, "end": v(49.66, -13.59) * mm});
            skLineSegment(sketch, "E2148", {"start": v(49.66, -13.59) * mm, "end": v(49.28, -13.48) * mm});
            skLineSegment(sketch, "E2149", {"start": v(49.28, -13.48) * mm, "end": v(48.9, -13.38) * mm});
            skLineSegment(sketch, "E2150", {"start": v(48.9, -13.38) * mm, "end": v(48.51, -13.28) * mm});
            skLineSegment(sketch, "E2151", {"start": v(48.51, -13.28) * mm, "end": v(48.13, -13.18) * mm});
            skLineSegment(sketch, "E2152", {"start": v(48.13, -13.18) * mm, "end": v(47.8, -13.1) * mm});
            skLineSegment(sketch, "E2153", {"start": v(47.8, -13.1) * mm, "end": v(47.88, -12.71) * mm});
            skLineSegment(sketch, "E2154", {"start": v(47.88, -12.71) * mm, "end": v(47.97, -12.33) * mm});
            skLineSegment(sketch, "E2155", {"start": v(47.97, -12.33) * mm, "end": v(48.05, -11.94) * mm});
            skLineSegment(sketch, "E2156", {"start": v(48.05, -11.94) * mm, "end": v(48.13, -11.56) * mm});
            skLineSegment(sketch, "E2157", {"start": v(48.13, -11.56) * mm, "end": v(48.22, -11.17) * mm});
            skLineSegment(sketch, "E2158", {"start": v(48.22, -11.17) * mm, "end": v(48.3, -10.79) * mm});
            skLineSegment(sketch, "E2159", {"start": v(48.3, -10.79) * mm, "end": v(48.39, -10.4) * mm});
            skLineSegment(sketch, "E2160", {"start": v(48.39, -10.4) * mm, "end": v(48.47, -10.02) * mm});
            skLineSegment(sketch, "E2161", {"start": v(48.47, -10.02) * mm, "end": v(48.55, -9.63) * mm});
            skLineSegment(sketch, "E2162", {"start": v(48.55, -9.63) * mm, "end": v(48.64, -9.25) * mm});
            skLineSegment(sketch, "E2163", {"start": v(48.64, -9.25) * mm, "end": v(48.72, -8.86) * mm});
            skLineSegment(sketch, "E2164", {"start": v(48.72, -8.86) * mm, "end": v(48.74, -8.77) * mm});
            skLineSegment(sketch, "E2165", {"start": v(48.74, -8.77) * mm, "end": v(49.13, -8.84) * mm});
            skLineSegment(sketch, "E2166", {"start": v(49.13, -8.84) * mm, "end": v(49.52, -8.9) * mm});
            skLineSegment(sketch, "E2167", {"start": v(49.52, -8.9) * mm, "end": v(49.9, -8.98) * mm});
            skLineSegment(sketch, "E2168", {"start": v(49.9, -8.98) * mm, "end": v(50.3, -9.04) * mm});
            skLineSegment(sketch, "E2169", {"start": v(50.3, -9.04) * mm, "end": v(50.69, -9.1) * mm});
            skLineSegment(sketch, "E2170", {"start": v(50.69, -9.1) * mm, "end": v(51.08, -9.18) * mm});
            skLineSegment(sketch, "E2171", {"start": v(51.08, -9.18) * mm, "end": v(51.47, -9.24) * mm});
            skLineSegment(sketch, "E2172", {"start": v(51.47, -9.24) * mm, "end": v(51.85, -9.31) * mm});
            skLineSegment(sketch, "E2173", {"start": v(51.85, -9.31) * mm, "end": v(52.25, -9.38) * mm});
            skLineSegment(sketch, "E2174", {"start": v(52.25, -9.38) * mm, "end": v(52.64, -9.45) * mm});
            skLineSegment(sketch, "E2175", {"start": v(52.64, -9.45) * mm, "end": v(53.02, -9.51) * mm});
            skLineSegment(sketch, "E2176", {"start": v(53.02, -9.51) * mm, "end": v(53.42, -9.58) * mm});
            skLineSegment(sketch, "E2177", {"start": v(53.42, -9.58) * mm, "end": v(53.84, -9.65) * mm});
            skLineSegment(sketch, "E2178", {"start": v(53.84, -9.65) * mm, "end": v(54.26, -9.64) * mm});
            skLineSegment(sketch, "E2179", {"start": v(54.26, -9.64) * mm, "end": v(54.66, -9.52) * mm});
            skLineSegment(sketch, "E2180", {"start": v(54.66, -9.52) * mm, "end": v(55.02, -9.3) * mm});
            skLineSegment(sketch, "E2181", {"start": v(55.02, -9.3) * mm, "end": v(55.31, -8.98) * mm});
            skLineSegment(sketch, "E2182", {"start": v(55.31, -8.98) * mm, "end": v(55.5, -8.6) * mm});
            skLineSegment(sketch, "E2183", {"start": v(55.5, -8.6) * mm, "end": v(55.6, -8.28) * mm});
            skLineSegment(sketch, "E2184", {"start": v(55.6, -8.28) * mm, "end": v(55.6, -7.86) * mm});
            skLineSegment(sketch, "E2185", {"start": v(55.6, -7.86) * mm, "end": v(55.5, -7.45) * mm});
            skLineSegment(sketch, "E2186", {"start": v(55.5, -7.45) * mm, "end": v(55.28, -7.08) * mm});
            skLineSegment(sketch, "E2187", {"start": v(55.28, -7.08) * mm, "end": v(54.98, -6.78) * mm});
            skLineSegment(sketch, "E2188", {"start": v(54.98, -6.78) * mm, "end": v(54.62, -6.57) * mm});
            skLineSegment(sketch, "E2189", {"start": v(54.62, -6.57) * mm, "end": v(54.2, -6.46) * mm});
            skLineSegment(sketch, "E2190", {"start": v(54.2, -6.46) * mm, "end": v(53.82, -6.41) * mm});
            skLineSegment(sketch, "E2191", {"start": v(53.82, -6.41) * mm, "end": v(53.43, -6.37) * mm});
            skLineSegment(sketch, "E2192", {"start": v(53.43, -6.37) * mm, "end": v(53.03, -6.32) * mm});
            skLineSegment(sketch, "E2193", {"start": v(53.03, -6.32) * mm, "end": v(52.64, -6.28) * mm});
            skLineSegment(sketch, "E2194", {"start": v(52.64, -6.28) * mm, "end": v(52.25, -6.23) * mm});
            skLineSegment(sketch, "E2195", {"start": v(52.25, -6.23) * mm, "end": v(51.85, -6.19) * mm});
            skLineSegment(sketch, "E2196", {"start": v(51.85, -6.19) * mm, "end": v(51.46, -6.14) * mm});
            skLineSegment(sketch, "E2197", {"start": v(51.46, -6.14) * mm, "end": v(51.07, -6.1) * mm});
            skLineSegment(sketch, "E2198", {"start": v(51.07, -6.1) * mm, "end": v(50.67, -6.05) * mm});
            skLineSegment(sketch, "E2199", {"start": v(50.67, -6.05) * mm, "end": v(50.28, -6) * mm});
            skLineSegment(sketch, "E2200", {"start": v(50.28, -6) * mm, "end": v(49.89, -5.96) * mm});
            skLineSegment(sketch, "E2201", {"start": v(49.89, -5.96) * mm, "end": v(49.5, -5.92) * mm});
            skLineSegment(sketch, "E2202", {"start": v(49.5, -5.92) * mm, "end": v(49.16, -5.88) * mm});
            skLineSegment(sketch, "E2203", {"start": v(49.16, -5.88) * mm, "end": v(49.18, -5.48) * mm});
            skLineSegment(sketch, "E2204", {"start": v(49.18, -5.48) * mm, "end": v(49.21, -5.1) * mm});
            skLineSegment(sketch, "E2205", {"start": v(49.21, -5.1) * mm, "end": v(49.24, -4.7) * mm});
            skLineSegment(sketch, "E2206", {"start": v(49.24, -4.7) * mm, "end": v(49.27, -4.3) * mm});
            skLineSegment(sketch, "E2207", {"start": v(49.27, -4.3) * mm, "end": v(49.3, -3.91) * mm});
            skLineSegment(sketch, "E2208", {"start": v(49.3, -3.91) * mm, "end": v(49.32, -3.52) * mm});
            skLineSegment(sketch, "E2209", {"start": v(49.32, -3.52) * mm, "end": v(49.35, -3.13) * mm});
            skLineSegment(sketch, "E2210", {"start": v(49.35, -3.13) * mm, "end": v(49.38, -2.73) * mm});
            skLineSegment(sketch, "E2211", {"start": v(49.38, -2.73) * mm, "end": v(49.4, -2.34) * mm});
            skLineSegment(sketch, "E2212", {"start": v(49.4, -2.34) * mm, "end": v(49.44, -1.95) * mm});
            skLineSegment(sketch, "E2213", {"start": v(49.44, -1.95) * mm, "end": v(49.47, -1.56) * mm});
            skLineSegment(sketch, "E2214", {"start": v(49.47, -1.56) * mm, "end": v(49.47, -1.46) * mm});
            skLineSegment(sketch, "E2215", {"start": v(-10.31, 2.7) * mm, "end": v(-10.12, 3.22) * mm});
            skLineSegment(sketch, "E2216", {"start": v(-10.12, 3.22) * mm, "end": v(-9.9, 3.72) * mm});
            skLineSegment(sketch, "E2217", {"start": v(-9.9, 3.72) * mm, "end": v(-9.66, 4.21) * mm});
            skLineSegment(sketch, "E2218", {"start": v(-9.66, 4.21) * mm, "end": v(-9.38, 4.69) * mm});
            skLineSegment(sketch, "E2219", {"start": v(-9.38, 4.69) * mm, "end": v(-9.07, 5.14) * mm});
            skLineSegment(sketch, "E2220", {"start": v(-9.07, 5.14) * mm, "end": v(-8.73, 5.58) * mm});
            skLineSegment(sketch, "E2221", {"start": v(-8.73, 5.58) * mm, "end": v(-8.37, 5.99) * mm});
            skLineSegment(sketch, "E2222", {"start": v(-8.37, 5.99) * mm, "end": v(-7.98, 6.38) * mm});
            skLineSegment(sketch, "E2223", {"start": v(-7.98, 6.38) * mm, "end": v(-7.57, 6.74) * mm});
            skLineSegment(sketch, "E2224", {"start": v(-7.57, 6.74) * mm, "end": v(-7.13, 7.08) * mm});
            skLineSegment(sketch, "E2225", {"start": v(-7.13, 7.08) * mm, "end": v(-6.68, 7.39) * mm});
            skLineSegment(sketch, "E2226", {"start": v(-6.68, 7.39) * mm, "end": v(-6.2, 7.67) * mm});
            skLineSegment(sketch, "E2227", {"start": v(-6.2, 7.67) * mm, "end": v(-5.72, 7.91) * mm});
            skLineSegment(sketch, "E2228", {"start": v(-5.72, 7.91) * mm, "end": v(-5.21, 8.13) * mm});
            skLineSegment(sketch, "E2229", {"start": v(-5.21, 8.13) * mm, "end": v(-4.7, 8.32) * mm});
            skLineSegment(sketch, "E2230", {"start": v(-4.7, 8.32) * mm, "end": v(-4.59, 8.35) * mm});
            skLineSegment(sketch, "E2231", {"start": v(-4.59, 8.35) * mm, "end": v(-4.7, 46.25) * mm});
            skLineSegment(sketch, "E2232", {"start": v(-4.7, 46.25) * mm, "end": v(-4.9, 46.24) * mm});
            skLineSegment(sketch, "E2233", {"start": v(-4.9, 46.24) * mm, "end": v(-7.8, 45.97) * mm});
            skLineSegment(sketch, "E2234", {"start": v(-7.8, 45.97) * mm, "end": v(-10.67, 45.51) * mm});
            skLineSegment(sketch, "E2235", {"start": v(-10.67, 45.51) * mm, "end": v(-13.51, 44.88) * mm});
            skLineSegment(sketch, "E2236", {"start": v(-13.51, 44.88) * mm, "end": v(-16.3, 44.06) * mm});
            skLineSegment(sketch, "E2237", {"start": v(-16.3, 44.06) * mm, "end": v(-19.05, 43.08) * mm});
            skLineSegment(sketch, "E2238", {"start": v(-19.05, 43.08) * mm, "end": v(-21.72, 41.92) * mm});
            skLineSegment(sketch, "E2239", {"start": v(-21.72, 41.92) * mm, "end": v(-24.31, 40.6) * mm});
            skLineSegment(sketch, "E2240", {"start": v(-24.31, 40.6) * mm, "end": v(-26.82, 39.12) * mm});
            skLineSegment(sketch, "E2241", {"start": v(-26.82, 39.12) * mm, "end": v(-29.22, 37.48) * mm});
            skLineSegment(sketch, "E2242", {"start": v(-29.22, 37.48) * mm, "end": v(-31.52, 35.7) * mm});
            skLineSegment(sketch, "E2243", {"start": v(-31.52, 35.7) * mm, "end": v(-33.7, 33.77) * mm});
            skLineSegment(sketch, "E2244", {"start": v(-33.7, 33.77) * mm, "end": v(-35.76, 31.72) * mm});
            skLineSegment(sketch, "E2245", {"start": v(-35.76, 31.72) * mm, "end": v(-37.69, 29.53) * mm});
            skLineSegment(sketch, "E2246", {"start": v(-37.69, 29.53) * mm, "end": v(-39.47, 27.23) * mm});
            skLineSegment(sketch, "E2247", {"start": v(-39.47, 27.23) * mm, "end": v(-41.1, 24.82) * mm});
            skLineSegment(sketch, "E2248", {"start": v(-41.1, 24.82) * mm, "end": v(-42.6, 22.32) * mm});
            skLineSegment(sketch, "E2249", {"start": v(-42.6, 22.32) * mm, "end": v(-43.91, 19.73) * mm});
            skLineSegment(sketch, "E2250", {"start": v(-43.91, 19.73) * mm, "end": v(-45.07, 17.06) * mm});
            skLineSegment(sketch, "E2251", {"start": v(-45.07, 17.06) * mm, "end": v(-46.05, 14.32) * mm});
            skLineSegment(sketch, "E2252", {"start": v(-46.05, 14.32) * mm, "end": v(-46.87, 11.52) * mm});
            skLineSegment(sketch, "E2253", {"start": v(-46.87, 11.52) * mm, "end": v(-47.5, 8.68) * mm});
            skLineSegment(sketch, "E2254", {"start": v(-47.5, 8.68) * mm, "end": v(-47.96, 5.8) * mm});
            skLineSegment(sketch, "E2255", {"start": v(-47.96, 5.8) * mm, "end": v(-48.23, 2.9) * mm});
            skLineSegment(sketch, "E2256", {"start": v(-48.23, 2.9) * mm, "end": v(-48.24, 2.7) * mm});
            skLineSegment(sketch, "E2257", {"start": v(-48.24, 2.7) * mm, "end": v(-10.34, 2.6) * mm});
            skLineSegment(sketch, "E2258", {"start": v(-10.34, 2.6) * mm, "end": v(-10.31, 2.7) * mm});
            skLineSegment(sketch, "E2259", {"start": v(44.26, 2.7) * mm, "end": v(44.25, 2.9) * mm});
            skLineSegment(sketch, "E2260", {"start": v(44.25, 2.9) * mm, "end": v(43.98, 5.8) * mm});
            skLineSegment(sketch, "E2261", {"start": v(43.98, 5.8) * mm, "end": v(43.52, 8.68) * mm});
            skLineSegment(sketch, "E2262", {"start": v(43.52, 8.68) * mm, "end": v(42.89, 11.52) * mm});
            skLineSegment(sketch, "E2263", {"start": v(42.89, 11.52) * mm, "end": v(42.07, 14.32) * mm});
            skLineSegment(sketch, "E2264", {"start": v(42.07, 14.32) * mm, "end": v(41.09, 17.06) * mm});
            skLineSegment(sketch, "E2265", {"start": v(41.09, 17.06) * mm, "end": v(39.93, 19.73) * mm});
            skLineSegment(sketch, "E2266", {"start": v(39.93, 19.73) * mm, "end": v(38.61, 22.32) * mm});
            skLineSegment(sketch, "E2267", {"start": v(38.61, 22.32) * mm, "end": v(37.13, 24.82) * mm});
            skLineSegment(sketch, "E2268", {"start": v(37.13, 24.82) * mm, "end": v(35.5, 27.23) * mm});
            skLineSegment(sketch, "E2269", {"start": v(35.5, 27.23) * mm, "end": v(33.7, 29.53) * mm});
            skLineSegment(sketch, "E2270", {"start": v(33.7, 29.53) * mm, "end": v(31.78, 31.72) * mm});
            skLineSegment(sketch, "E2271", {"start": v(31.78, 31.72) * mm, "end": v(29.73, 33.77) * mm});
            skLineSegment(sketch, "E2272", {"start": v(29.73, 33.77) * mm, "end": v(27.54, 35.7) * mm});
            skLineSegment(sketch, "E2273", {"start": v(27.54, 35.7) * mm, "end": v(25.24, 37.48) * mm});
            skLineSegment(sketch, "E2274", {"start": v(25.24, 37.48) * mm, "end": v(22.84, 39.12) * mm});
            skLineSegment(sketch, "E2275", {"start": v(22.84, 39.12) * mm, "end": v(20.33, 40.6) * mm});
            skLineSegment(sketch, "E2276", {"start": v(20.33, 40.6) * mm, "end": v(17.74, 41.92) * mm});
            skLineSegment(sketch, "E2277", {"start": v(17.74, 41.92) * mm, "end": v(15.07, 43.08) * mm});
            skLineSegment(sketch, "E2278", {"start": v(15.07, 43.08) * mm, "end": v(12.33, 44.06) * mm});
            skLineSegment(sketch, "E2279", {"start": v(12.33, 44.06) * mm, "end": v(9.53, 44.88) * mm});
            skLineSegment(sketch, "E2280", {"start": v(9.53, 44.88) * mm, "end": v(6.7, 45.51) * mm});
            skLineSegment(sketch, "E2281", {"start": v(6.7, 45.51) * mm, "end": v(3.82, 45.97) * mm});
            skLineSegment(sketch, "E2282", {"start": v(3.82, 45.97) * mm, "end": v(0.92, 46.24) * mm});
            skLineSegment(sketch, "E2283", {"start": v(0.92, 46.24) * mm, "end": v(0.72, 46.25) * mm});
            skLineSegment(sketch, "E2284", {"start": v(0.72, 46.25) * mm, "end": v(0.6, 8.35) * mm});
            skLineSegment(sketch, "E2285", {"start": v(0.6, 8.35) * mm, "end": v(0.71, 8.32) * mm});
            skLineSegment(sketch, "E2286", {"start": v(0.71, 8.32) * mm, "end": v(1.23, 8.13) * mm});
            skLineSegment(sketch, "E2287", {"start": v(1.23, 8.13) * mm, "end": v(1.73, 7.91) * mm});
            skLineSegment(sketch, "E2288", {"start": v(1.73, 7.91) * mm, "end": v(2.22, 7.67) * mm});
            skLineSegment(sketch, "E2289", {"start": v(2.22, 7.67) * mm, "end": v(2.7, 7.39) * mm});
            skLineSegment(sketch, "E2290", {"start": v(2.7, 7.39) * mm, "end": v(3.15, 7.08) * mm});
            skLineSegment(sketch, "E2291", {"start": v(3.15, 7.08) * mm, "end": v(3.59, 6.74) * mm});
            skLineSegment(sketch, "E2292", {"start": v(3.59, 6.74) * mm, "end": v(4, 6.38) * mm});
            skLineSegment(sketch, "E2293", {"start": v(4, 6.38) * mm, "end": v(4.39, 5.99) * mm});
            skLineSegment(sketch, "E2294", {"start": v(4.39, 5.99) * mm, "end": v(4.75, 5.58) * mm});
            skLineSegment(sketch, "E2295", {"start": v(4.75, 5.58) * mm, "end": v(5.09, 5.14) * mm});
            skLineSegment(sketch, "E2296", {"start": v(5.09, 5.14) * mm, "end": v(5.4, 4.69) * mm});
            skLineSegment(sketch, "E2297", {"start": v(5.4, 4.69) * mm, "end": v(5.68, 4.21) * mm});
            skLineSegment(sketch, "E2298", {"start": v(5.68, 4.21) * mm, "end": v(5.93, 3.72) * mm});
            skLineSegment(sketch, "E2299", {"start": v(5.93, 3.72) * mm, "end": v(6.14, 3.22) * mm});
            skLineSegment(sketch, "E2300", {"start": v(6.14, 3.22) * mm, "end": v(6.33, 2.7) * mm});
            skLineSegment(sketch, "E2301", {"start": v(6.33, 2.7) * mm, "end": v(6.36, 2.6) * mm});
            skLineSegment(sketch, "E2302", {"start": v(6.36, 2.6) * mm, "end": v(44.26, 2.7) * mm});
            skLineSegment(sketch, "E2303", {"start": v(0.92, -46.24) * mm, "end": v(3.82, -45.97) * mm});
            skLineSegment(sketch, "E2304", {"start": v(3.82, -45.97) * mm, "end": v(6.7, -45.51) * mm});
            skLineSegment(sketch, "E2305", {"start": v(6.7, -45.51) * mm, "end": v(9.53, -44.88) * mm});
            skLineSegment(sketch, "E2306", {"start": v(9.53, -44.88) * mm, "end": v(12.33, -44.07) * mm});
            skLineSegment(sketch, "E2307", {"start": v(12.33, -44.07) * mm, "end": v(15.07, -43.08) * mm});
            skLineSegment(sketch, "E2308", {"start": v(15.07, -43.08) * mm, "end": v(17.74, -41.92) * mm});
            skLineSegment(sketch, "E2309", {"start": v(17.74, -41.92) * mm, "end": v(20.33, -40.6) * mm});
            skLineSegment(sketch, "E2310", {"start": v(20.33, -40.6) * mm, "end": v(22.84, -39.12) * mm});
            skLineSegment(sketch, "E2311", {"start": v(22.84, -39.12) * mm, "end": v(25.24, -37.48) * mm});
            skLineSegment(sketch, "E2312", {"start": v(25.24, -37.48) * mm, "end": v(27.54, -35.7) * mm});
            skLineSegment(sketch, "E2313", {"start": v(27.54, -35.7) * mm, "end": v(29.73, -33.78) * mm});
            skLineSegment(sketch, "E2314", {"start": v(29.73, -33.78) * mm, "end": v(31.78, -31.72) * mm});
            skLineSegment(sketch, "E2315", {"start": v(31.78, -31.72) * mm, "end": v(33.7, -29.53) * mm});
            skLineSegment(sketch, "E2316", {"start": v(33.7, -29.53) * mm, "end": v(35.5, -27.23) * mm});
            skLineSegment(sketch, "E2317", {"start": v(35.5, -27.23) * mm, "end": v(37.13, -24.83) * mm});
            skLineSegment(sketch, "E2318", {"start": v(37.13, -24.83) * mm, "end": v(38.61, -22.32) * mm});
            skLineSegment(sketch, "E2319", {"start": v(38.61, -22.32) * mm, "end": v(39.93, -19.73) * mm});
            skLineSegment(sketch, "E2320", {"start": v(39.93, -19.73) * mm, "end": v(41.09, -17.06) * mm});
            skLineSegment(sketch, "E2321", {"start": v(41.09, -17.06) * mm, "end": v(42.07, -14.32) * mm});
            skLineSegment(sketch, "E2322", {"start": v(42.07, -14.32) * mm, "end": v(42.89, -11.52) * mm});
            skLineSegment(sketch, "E2323", {"start": v(42.89, -11.52) * mm, "end": v(43.52, -8.68) * mm});
            skLineSegment(sketch, "E2324", {"start": v(43.52, -8.68) * mm, "end": v(43.98, -5.8) * mm});
            skLineSegment(sketch, "E2325", {"start": v(43.98, -5.8) * mm, "end": v(44.25, -2.91) * mm});
            skLineSegment(sketch, "E2326", {"start": v(44.25, -2.91) * mm, "end": v(44.26, -2.7) * mm});
            skLineSegment(sketch, "E2327", {"start": v(44.26, -2.7) * mm, "end": v(6.36, -2.6) * mm});
            skLineSegment(sketch, "E2328", {"start": v(6.36, -2.6) * mm, "end": v(6.33, -2.7) * mm});
            skLineSegment(sketch, "E2329", {"start": v(6.33, -2.7) * mm, "end": v(6.14, -3.22) * mm});
            skLineSegment(sketch, "E2330", {"start": v(6.14, -3.22) * mm, "end": v(5.93, -3.73) * mm});
            skLineSegment(sketch, "E2331", {"start": v(5.93, -3.73) * mm, "end": v(5.68, -4.22) * mm});
            skLineSegment(sketch, "E2332", {"start": v(5.68, -4.22) * mm, "end": v(5.4, -4.69) * mm});
            skLineSegment(sketch, "E2333", {"start": v(5.4, -4.69) * mm, "end": v(5.09, -5.14) * mm});
            skLineSegment(sketch, "E2334", {"start": v(5.09, -5.14) * mm, "end": v(4.75, -5.58) * mm});
            skLineSegment(sketch, "E2335", {"start": v(4.75, -5.58) * mm, "end": v(4.39, -5.99) * mm});
            skLineSegment(sketch, "E2336", {"start": v(4.39, -5.99) * mm, "end": v(4, -6.38) * mm});
            skLineSegment(sketch, "E2337", {"start": v(4, -6.38) * mm, "end": v(3.59, -6.74) * mm});
            skLineSegment(sketch, "E2338", {"start": v(3.59, -6.74) * mm, "end": v(3.15, -7.08) * mm});
            skLineSegment(sketch, "E2339", {"start": v(3.15, -7.08) * mm, "end": v(2.7, -7.39) * mm});
            skLineSegment(sketch, "E2340", {"start": v(2.7, -7.39) * mm, "end": v(2.22, -7.67) * mm});
            skLineSegment(sketch, "E2341", {"start": v(2.22, -7.67) * mm, "end": v(1.73, -7.92) * mm});
            skLineSegment(sketch, "E2342", {"start": v(1.73, -7.92) * mm, "end": v(1.23, -8.14) * mm});
            skLineSegment(sketch, "E2343", {"start": v(1.23, -8.14) * mm, "end": v(0.71, -8.32) * mm});
            skLineSegment(sketch, "E2344", {"start": v(0.71, -8.32) * mm, "end": v(0.6, -8.35) * mm});
            skLineSegment(sketch, "E2345", {"start": v(0.6, -8.35) * mm, "end": v(0.72, -46.25) * mm});
            skLineSegment(sketch, "E2346", {"start": v(0.72, -46.25) * mm, "end": v(0.92, -46.24) * mm});
            skLineSegment(sketch, "E2347", {"start": v(-4.59, -8.35) * mm, "end": v(-4.7, -8.32) * mm});
            skLineSegment(sketch, "E2348", {"start": v(-4.7, -8.32) * mm, "end": v(-5.21, -8.14) * mm});
            skLineSegment(sketch, "E2349", {"start": v(-5.21, -8.14) * mm, "end": v(-5.72, -7.92) * mm});
            skLineSegment(sketch, "E2350", {"start": v(-5.72, -7.92) * mm, "end": v(-6.2, -7.67) * mm});
            skLineSegment(sketch, "E2351", {"start": v(-6.2, -7.67) * mm, "end": v(-6.68, -7.39) * mm});
            skLineSegment(sketch, "E2352", {"start": v(-6.68, -7.39) * mm, "end": v(-7.13, -7.08) * mm});
            skLineSegment(sketch, "E2353", {"start": v(-7.13, -7.08) * mm, "end": v(-7.57, -6.74) * mm});
            skLineSegment(sketch, "E2354", {"start": v(-7.57, -6.74) * mm, "end": v(-7.98, -6.38) * mm});
            skLineSegment(sketch, "E2355", {"start": v(-7.98, -6.38) * mm, "end": v(-8.37, -5.99) * mm});
            skLineSegment(sketch, "E2356", {"start": v(-8.37, -5.99) * mm, "end": v(-8.73, -5.58) * mm});
            skLineSegment(sketch, "E2357", {"start": v(-8.73, -5.58) * mm, "end": v(-9.07, -5.14) * mm});
            skLineSegment(sketch, "E2358", {"start": v(-9.07, -5.14) * mm, "end": v(-9.38, -4.69) * mm});
            skLineSegment(sketch, "E2359", {"start": v(-9.38, -4.69) * mm, "end": v(-9.66, -4.22) * mm});
            skLineSegment(sketch, "E2360", {"start": v(-9.66, -4.22) * mm, "end": v(-9.9, -3.73) * mm});
            skLineSegment(sketch, "E2361", {"start": v(-9.9, -3.73) * mm, "end": v(-10.12, -3.22) * mm});
            skLineSegment(sketch, "E2362", {"start": v(-10.12, -3.22) * mm, "end": v(-10.31, -2.7) * mm});
            skLineSegment(sketch, "E2363", {"start": v(-10.31, -2.7) * mm, "end": v(-10.34, -2.6) * mm});
            skLineSegment(sketch, "E2364", {"start": v(-10.34, -2.6) * mm, "end": v(-48.24, -2.7) * mm});
            skLineSegment(sketch, "E2365", {"start": v(-48.24, -2.7) * mm, "end": v(-48.23, -2.91) * mm});
            skLineSegment(sketch, "E2366", {"start": v(-48.23, -2.91) * mm, "end": v(-47.96, -5.8) * mm});
            skLineSegment(sketch, "E2367", {"start": v(-47.96, -5.8) * mm, "end": v(-47.5, -8.68) * mm});
            skLineSegment(sketch, "E2368", {"start": v(-47.5, -8.68) * mm, "end": v(-46.87, -11.52) * mm});
            skLineSegment(sketch, "E2369", {"start": v(-46.87, -11.52) * mm, "end": v(-46.05, -14.32) * mm});
            skLineSegment(sketch, "E2370", {"start": v(-46.05, -14.32) * mm, "end": v(-45.07, -17.06) * mm});
            skLineSegment(sketch, "E2371", {"start": v(-45.07, -17.06) * mm, "end": v(-43.91, -19.73) * mm});
            skLineSegment(sketch, "E2372", {"start": v(-43.91, -19.73) * mm, "end": v(-42.6, -22.32) * mm});
            skLineSegment(sketch, "E2373", {"start": v(-42.6, -22.32) * mm, "end": v(-41.1, -24.83) * mm});
            skLineSegment(sketch, "E2374", {"start": v(-41.1, -24.83) * mm, "end": v(-39.47, -27.23) * mm});
            skLineSegment(sketch, "E2375", {"start": v(-39.47, -27.23) * mm, "end": v(-37.69, -29.53) * mm});
            skLineSegment(sketch, "E2376", {"start": v(-37.69, -29.53) * mm, "end": v(-35.76, -31.72) * mm});
            skLineSegment(sketch, "E2377", {"start": v(-35.76, -31.72) * mm, "end": v(-33.7, -33.78) * mm});
            skLineSegment(sketch, "E2378", {"start": v(-33.7, -33.78) * mm, "end": v(-31.52, -35.7) * mm});
            skLineSegment(sketch, "E2379", {"start": v(-31.52, -35.7) * mm, "end": v(-29.22, -37.48) * mm});
            skLineSegment(sketch, "E2380", {"start": v(-29.22, -37.48) * mm, "end": v(-26.82, -39.12) * mm});
            skLineSegment(sketch, "E2381", {"start": v(-26.82, -39.12) * mm, "end": v(-24.31, -40.6) * mm});
            skLineSegment(sketch, "E2382", {"start": v(-24.31, -40.6) * mm, "end": v(-21.72, -41.92) * mm});
            skLineSegment(sketch, "E2383", {"start": v(-21.72, -41.92) * mm, "end": v(-19.05, -43.08) * mm});
            skLineSegment(sketch, "E2384", {"start": v(-19.05, -43.08) * mm, "end": v(-16.3, -44.07) * mm});
            skLineSegment(sketch, "E2385", {"start": v(-16.3, -44.07) * mm, "end": v(-13.51, -44.88) * mm});
            skLineSegment(sketch, "E2386", {"start": v(-13.51, -44.88) * mm, "end": v(-10.67, -45.51) * mm});
            skLineSegment(sketch, "E2387", {"start": v(-10.67, -45.51) * mm, "end": v(-7.8, -45.97) * mm});
            skLineSegment(sketch, "E2388", {"start": v(-7.8, -45.97) * mm, "end": v(-4.9, -46.24) * mm});
            skLineSegment(sketch, "E2389", {"start": v(-4.9, -46.24) * mm, "end": v(-4.7, -46.25) * mm});
            skLineSegment(sketch, "E2390", {"start": v(-4.7, -46.25) * mm, "end": v(-4.59, -8.35) * mm});
            skCircle(sketch, "E2391", {"center": v(-2, 0) * mm, "radius": 2.65 * mm});
            skCircle(sketch, "E2392", {"center": v(-2, 0) * mm, "radius": 22.1 * mm});
            skCircle(sketch, "E2393", {"center": v(-2, 0) * mm, "radius": 10.7 * mm});
            skCircle(sketch, "E2394", {"center": v(-2, 0) * mm, "radius": 4.5 * mm, "construction": true});
            skLineSegment(sketch, "E2395", {"start": v(-4.59, -8.35) * mm, "end": v(-4.59, -3.68) * mm});
            skLineSegment(sketch, "E2396", {"start": v(0.6, -8.35) * mm, "end": v(0.6, -3.68) * mm});
            skLineSegment(sketch, "E2397", {"start": v(-10.34, -2.6) * mm, "end": v(-5.67, -2.59) * mm});
            skLineSegment(sketch, "E2398", {"start": v(-10.34, 2.6) * mm, "end": v(-5.67, 2.58) * mm});
            skLineSegment(sketch, "E2399", {"start": v(6.36, -2.6) * mm, "end": v(1.7, -2.59) * mm});
            skLineSegment(sketch, "E2400", {"start": v(6.36, 2.6) * mm, "end": v(1.7, 2.58) * mm});
            skLineSegment(sketch, "E2401", {"start": v(-4.59, 8.35) * mm, "end": v(-4.57, 3.68) * mm});
            skLineSegment(sketch, "E2402", {"start": v(0.6, 8.35) * mm, "end": v(0.6, 3.67) * mm});
            skCircle(sketch, "E2403", {"center": v(-2, 0) * mm, "radius": 6 * mm});
            skSolve(sketch);
        }
        {
            var Q0;
            Q0=makeQuery(id+"F0.imprint","IMPRINT",FACE,{"disambiguationData":[TD([[makeQuery(id+"F0.imprint","IMPRINT",EDGE,{"derivedFrom":sQuery(id+"F0.wireOp",EDGE,"E0")}),1.0]])]});
            var Q1;
            Q1=makeQuery(id+"F0.imprint","IMPRINT",FACE,{"disambiguationData":[TD([[makeQuery(id+"F0.imprint","IMPRINT",EDGE,{"derivedFrom":sQuery(id+"F0.wireOp",EDGE,"E2391")}),-1.0]])]});
            var Q2;
            Q2=makeQuery(id+"F0.imprint","IMPRINT",FACE,{"disambiguationData":[TD([[makeQuery(id+"F0.imprint","IMPRINT",EDGE,{"derivedFrom":sQuery(id+"F0.wireOp",EDGE,"E0")}),1.0]])]});
            var Q3;
            {var subQ0=sQuery(id+"F0.wireOp",EDGE,"E2393");var subQ1=sQuery(id+"F0.wireOp",EDGE,"E2231");var subQ2=makeQuery(id+"F0.imprint","INTERSECT",VERTEX,{"derivedFrom":[subQ1,subQ0]});Q3=makeQuery(id+"F0.imprint","IMPRINT",FACE,{"disambiguationData":[TD([[makeQuery(id+"F0.imprint","IMPRINT",EDGE,{"disambiguationData":[TD([[subQ2,-1.0]])],"derivedFrom":subQ1}),-1.0]])]});}
            var Q4;
            {var subQ0=sQuery(id+"F0.wireOp",EDGE,"E2392");var subQ1=sQuery(id+"F0.wireOp",EDGE,"E2257");var subQ2=makeQuery(id+"F0.imprint","INTERSECT",VERTEX,{"derivedFrom":[subQ1,subQ0]});Q4=makeQuery(id+"F0.imprint","IMPRINT",FACE,{"disambiguationData":[TD([[makeQuery(id+"F0.imprint","IMPRINT",EDGE,{"disambiguationData":[TD([[subQ2,-1.0]])],"derivedFrom":subQ1}),-1.0]])]});}
            var Q5;
            {var subQ0=sQuery(id+"F0.wireOp",EDGE,"E2393");var subQ1=sQuery(id+"F0.wireOp",EDGE,"E2345");var subQ2=makeQuery(id+"F0.imprint","INTERSECT",VERTEX,{"derivedFrom":[subQ1,subQ0]});Q5=makeQuery(id+"F0.imprint","IMPRINT",FACE,{"disambiguationData":[TD([[makeQuery(id+"F0.imprint","IMPRINT",EDGE,{"disambiguationData":[TD([[subQ2,-1.0]])],"derivedFrom":subQ1}),-1.0]])]});}
            var Q6;
            {var subQ0=sQuery(id+"F0.wireOp",EDGE,"E2393");var subQ1=sQuery(id+"F0.wireOp",EDGE,"E2302");var subQ2=makeQuery(id+"F0.imprint","INTERSECT",VERTEX,{"derivedFrom":[subQ1,subQ0]});Q6=makeQuery(id+"F0.imprint","IMPRINT",FACE,{"disambiguationData":[TD([[makeQuery(id+"F0.imprint","IMPRINT",EDGE,{"disambiguationData":[TD([[subQ2,-1.0]])],"derivedFrom":subQ1}),-1.0]])]});}
            var Q7;
            {var subQ0=sQuery(id+"F0.wireOp",EDGE,"E2393");var subQ1=sQuery(id+"F0.wireOp",EDGE,"E2231");var subQ2=makeQuery(id+"F0.imprint","INTERSECT",VERTEX,{"derivedFrom":[subQ1,subQ0]});Q7=makeQuery(id+"F0.imprint","IMPRINT",FACE,{"disambiguationData":[TD([[makeQuery(id+"F0.imprint","IMPRINT",EDGE,{"disambiguationData":[TD([[subQ2,-1.0]])],"derivedFrom":subQ1}),1.0]])]});}
            var Q8;
            {var subQ0=sQuery(id+"F0.wireOp",EDGE,"E2392");var subQ1=sQuery(id+"F0.wireOp",EDGE,"E2284");var subQ2=makeQuery(id+"F0.imprint","INTERSECT",VERTEX,{"derivedFrom":[subQ1,subQ0]});Q8=makeQuery(id+"F0.imprint","IMPRINT",FACE,{"disambiguationData":[TD([[makeQuery(id+"F0.imprint","IMPRINT",EDGE,{"disambiguationData":[TD([[subQ2,-1.0]])],"derivedFrom":subQ1}),1.0]])]});}
            var Q9;
            {var subQ0=sQuery(id+"F0.wireOp",EDGE,"E2392");var subQ1=sQuery(id+"F0.wireOp",EDGE,"E2327");var subQ2=makeQuery(id+"F0.imprint","INTERSECT",VERTEX,{"derivedFrom":[subQ1,subQ0]});Q9=makeQuery(id+"F0.imprint","IMPRINT",FACE,{"disambiguationData":[TD([[makeQuery(id+"F0.imprint","IMPRINT",EDGE,{"disambiguationData":[TD([[subQ2,-1.0]])],"derivedFrom":subQ1}),1.0]])]});}
            var Q10;
            {var subQ0=sQuery(id+"F0.wireOp",EDGE,"E2393");var subQ1=sQuery(id+"F0.wireOp",EDGE,"E2364");var subQ2=makeQuery(id+"F0.imprint","INTERSECT",VERTEX,{"derivedFrom":[subQ1,subQ0]});Q10=makeQuery(id+"F0.imprint","IMPRINT",FACE,{"disambiguationData":[TD([[makeQuery(id+"F0.imprint","IMPRINT",EDGE,{"disambiguationData":[TD([[subQ2,-1.0]])],"derivedFrom":subQ1}),1.0]])]});}
            var Q11;
            {var subQ0=sQuery(id+"F0.wireOp",EDGE,"E2395");Q11=makeQuery(id+"F0.imprint","IMPRINT",FACE,{"disambiguationData":[TD([[makeQuery(id+"F0.imprint","IMPRINT",EDGE,{"derivedFrom":subQ0}),-1.0]])]});}
            var Q12;
            {var subQ0=sQuery(id+"F0.wireOp",EDGE,"E2397");Q12=makeQuery(id+"F0.imprint","IMPRINT",FACE,{"disambiguationData":[TD([[makeQuery(id+"F0.imprint","IMPRINT",EDGE,{"derivedFrom":subQ0}),1.0]])]});}
            var Q13;
            {var subQ0=sQuery(id+"F0.wireOp",EDGE,"E2401");Q13=makeQuery(id+"F0.imprint","IMPRINT",FACE,{"disambiguationData":[TD([[makeQuery(id+"F0.imprint","IMPRINT",EDGE,{"derivedFrom":subQ0}),1.0]])]});}
            var Q14;
            {var subQ0=sQuery(id+"F0.wireOp",EDGE,"E2399");Q14=makeQuery(id+"F0.imprint","IMPRINT",FACE,{"disambiguationData":[TD([[makeQuery(id+"F0.imprint","IMPRINT",EDGE,{"derivedFrom":subQ0}),-1.0]])]});}
            extrude(context, id + "F1", {"entities" : qUnion([Q0, Q1, Q2, Q3, Q4, Q5, Q6, Q7, Q8, Q9, Q10, Q11, Q12, Q13, Q14]), "depth" : 5 * mm});
        }
    });
